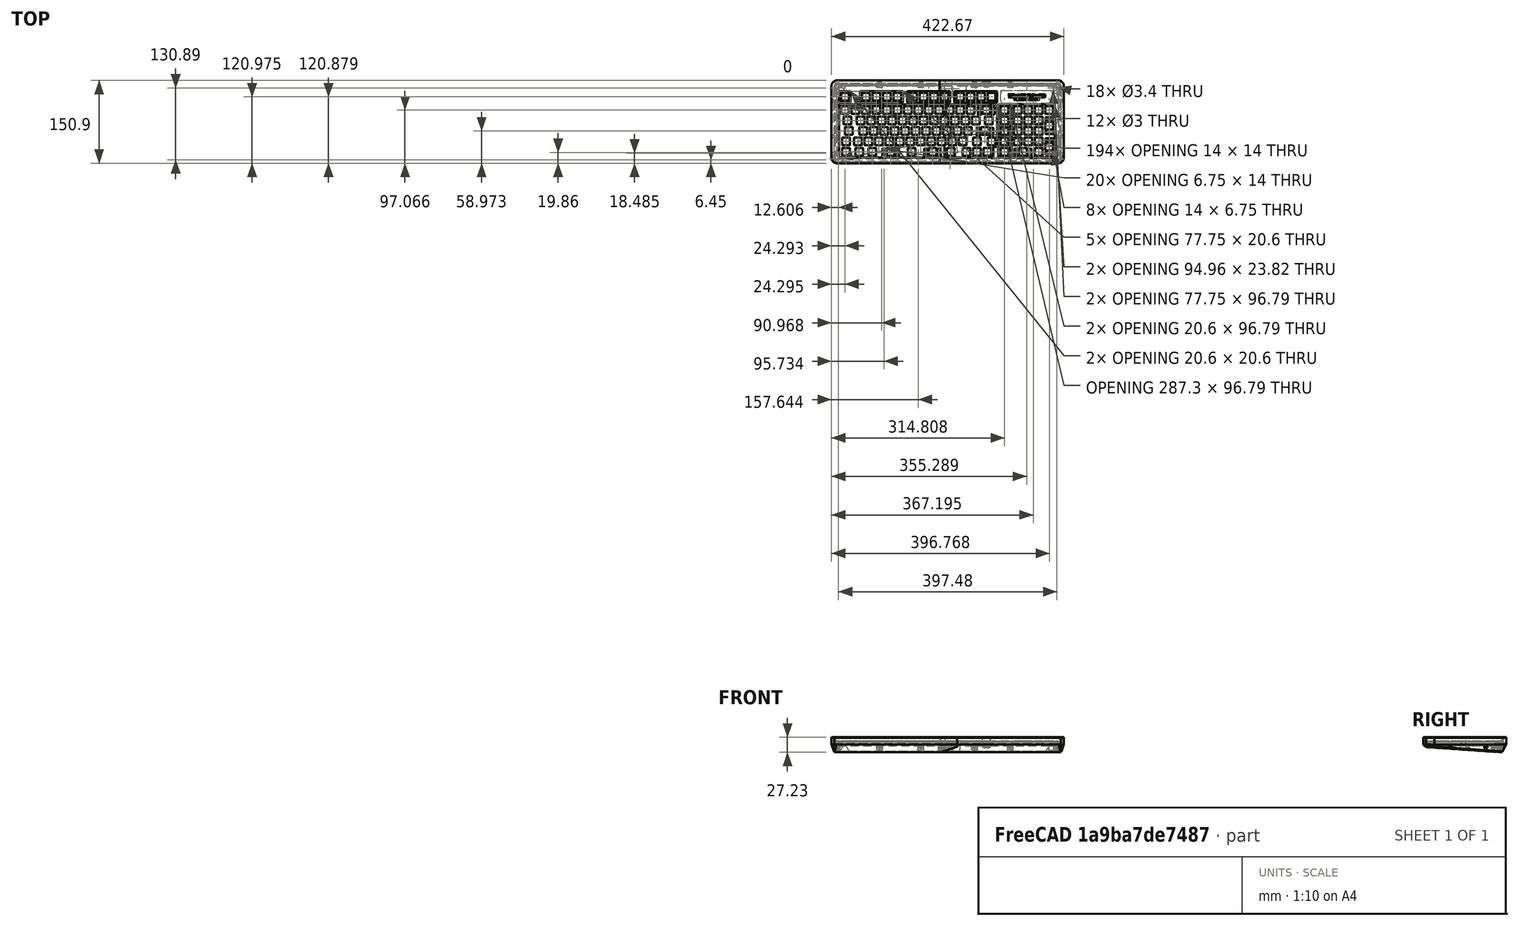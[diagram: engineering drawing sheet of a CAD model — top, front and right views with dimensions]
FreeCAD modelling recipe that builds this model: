
FCSTD DOCUMENT  (FreeCAD 0.21R33694 (Git))
Label: case
License: All rights reserved
LicenseURL: http://en.wikipedia.org/wiki/All_rights_reserved
objects: Sketcher::SketchObject×36, PartDesign::Pocket×20, PartDesign::SubShapeBinder×13, Part::FeaturePython×12, PartDesign::Pad×10, PartDesign::Plane×10, PartDesign::Body×6, Part::Part2DObjectPython×6, App::DocumentObjectGroup×4, PartDesign::AdditiveLoft×3, PartDesign::Chamfer×3, PartDesign::SubtractiveLoft×1, PartDesign::Fillet×1
note: 159 computed .brp shape members not serialized (recipe doc carries the construction recipe); baked Part::Feature solids carry a one-line shape summary decoded from their .brp

FEATURE [Sketcher::SketchObject] Sketch
  FullyConstrained = true
  sketch-geometry (922):
    g0: LineSegment StartX=400.028 StartY=-77.6274 StartZ=0 EndX=400.028 EndY=-71.8786 EndZ=0
    g1: LineSegment StartX=400.528 StartY=-71.3786 StartZ=0 EndX=413.528 EndY=-71.3774 EndZ=0
    g2: LineSegment StartX=414.028 StartY=-77.6274 StartZ=0 EndX=414.028 EndY=-71.8773 EndZ=0
    g3: LineSegment StartX=400.528 StartY=-95.1899 StartZ=0 EndX=413.528 EndY=-95.1899 EndZ=0
    g4: LineSegment StartX=400.028 StartY=-101.44 StartZ=0 EndX=400.028 EndY=-95.6899 EndZ=0
    g5: LineSegment StartX=400.528 StartY=-78.1274 StartZ=0 EndX=413.528 EndY=-78.1273 EndZ=0
    g6: LineSegment StartX=414.028 StartY=-101.44 StartZ=0 EndX=414.028 EndY=-95.6899 EndZ=0
    g7: LineSegment StartX=400.528 StartY=-101.94 StartZ=0 EndX=413.528 EndY=-101.94 EndZ=0
    g8: ArcOfCircle CenterX=413.528 CenterY=-71.8774 CenterZ=0 NormalX=0 NormalY=0 NormalZ=1 AngleXU=0 Radius=0.50005 StartAngle=9.99999e-05 EndAngle=1.57079
    g9: ArcOfCircle CenterX=413.528 CenterY=-95.6899 CenterZ=0 NormalX=0 NormalY=0 NormalZ=1 AngleXU=0 Radius=0.500001 StartAngle=1.99999e-06 EndAngle=1.57079
    g10: ArcOfCircle CenterX=400.528 CenterY=-71.8786 CenterZ=0 NormalX=0 NormalY=0 NormalZ=1 AngleXU=0 Radius=0.499999 StartAngle=1.57079 EndAngle=3.14152
    g11: ArcOfCircle CenterX=400.528 CenterY=-95.6899 CenterZ=0 NormalX=0 NormalY=0 NormalZ=1 AngleXU=0 Radius=0.500001 StartAngle=1.5708 EndAngle=3.14159
    g12: ArcOfCircle CenterX=413.528 CenterY=-101.44 CenterZ=0 NormalX=0 NormalY=0 NormalZ=1 AngleXU=0 Radius=0.500001 StartAngle=4.71239 EndAngle=6.28318
    g13: ArcOfCircle CenterX=413.528 CenterY=-77.6273 CenterZ=0 NormalX=0 NormalY=0 NormalZ=1 AngleXU=0 Radius=0.500001 StartAngle=4.71239 EndAngle=6.28309
    g14: ArcOfCircle CenterX=400.528 CenterY=-77.6274 CenterZ=0 NormalX=0 NormalY=0 NormalZ=1 AngleXU=0 Radius=0.49996 StartAngle=3.14151 EndAngle=4.71247
    g15: ArcOfCircle CenterX=400.528 CenterY=-101.44 CenterZ=0 NormalX=0 NormalY=0 NormalZ=1 AngleXU=0 Radius=0.500001 StartAngle=3.14159 EndAngle=4.71239
    g16: LineSegment StartX=179.329 StartY=-128.298 StartZ=0 EndX=185.079 EndY=-128.298 EndZ=0
    g17: LineSegment StartX=202.641 StartY=-128.798 StartZ=0 EndX=202.641 EndY=-141.798 EndZ=0
    g18: LineSegment StartX=203.141 StartY=-128.298 StartZ=0 EndX=208.89 EndY=-128.298 EndZ=0
    g19: LineSegment StartX=203.141 StartY=-142.298 StartZ=0 EndX=208.891 EndY=-142.298 EndZ=0
    g20: LineSegment StartX=185.579 StartY=-128.798 StartZ=0 EndX=185.579 EndY=-141.798 EndZ=0
    g21: LineSegment StartX=179.329 StartY=-142.298 StartZ=0 EndX=185.079 EndY=-142.298 EndZ=0
    g22: LineSegment StartX=178.829 StartY=-128.798 StartZ=0 EndX=178.829 EndY=-141.798 EndZ=0
    g23: LineSegment StartX=209.39 StartY=-128.798 StartZ=0 EndX=209.391 EndY=-141.798 EndZ=0
    g24: ArcOfCircle CenterX=179.329 CenterY=-141.798 CenterZ=0 NormalX=0 NormalY=0 NormalZ=1 AngleXU=0 Radius=0.500001 StartAngle=3.14159 EndAngle=4.71239
    g25: ArcOfCircle CenterX=185.079 CenterY=-128.798 CenterZ=0 NormalX=0 NormalY=0 NormalZ=1 AngleXU=0 Radius=0.500001 StartAngle=1.99999e-06 EndAngle=1.57079
    g26: ArcOfCircle CenterX=208.89 CenterY=-128.798 CenterZ=0 NormalX=0 NormalY=0 NormalZ=1 AngleXU=0 Radius=0.500099 StartAngle=0.000197985 EndAngle=1.57072
    g27: ArcOfCircle CenterX=203.141 CenterY=-141.798 CenterZ=0 NormalX=0 NormalY=0 NormalZ=1 AngleXU=0 Radius=0.500101 StartAngle=3.1418 EndAngle=4.71229
    g28: ArcOfCircle CenterX=203.141 CenterY=-128.798 CenterZ=0 NormalX=0 NormalY=0 NormalZ=1 AngleXU=0 Radius=0.49996 StartAngle=1.57071 EndAngle=3.14168
    g29: ArcOfCircle CenterX=179.329 CenterY=-128.798 CenterZ=0 NormalX=0 NormalY=0 NormalZ=1 AngleXU=0 Radius=0.500001 StartAngle=1.5708 EndAngle=3.14159
    g30: ArcOfCircle CenterX=185.079 CenterY=-141.798 CenterZ=0 NormalX=0 NormalY=0 NormalZ=1 AngleXU=0 Radius=0.500001 StartAngle=4.71239 EndAngle=6.28318
    g31: ArcOfCircle CenterX=208.891 CenterY=-141.798 CenterZ=0 NormalX=0 NormalY=0 NormalZ=1 AngleXU=0 Radius=0.49995 StartAngle=4.71229 EndAngle=6.28318
    g32: LineSegment StartX=276.438 StartY=-52.5898 StartZ=0 EndX=276.438 EndY=-65.5898 EndZ=0
    g33: LineSegment StartX=300.75 StartY=-52.0898 StartZ=0 EndX=306.499 EndY=-52.0898 EndZ=0
    g34: LineSegment StartX=300.25 StartY=-52.5898 StartZ=0 EndX=300.25 EndY=-65.5898 EndZ=0
    g35: LineSegment StartX=300.75 StartY=-66.0898 StartZ=0 EndX=306.5 EndY=-66.0897 EndZ=0
    g36: LineSegment StartX=283.188 StartY=-52.5898 StartZ=0 EndX=283.188 EndY=-65.5898 EndZ=0
    g37: LineSegment StartX=306.999 StartY=-52.5898 StartZ=0 EndX=307 EndY=-65.5898 EndZ=0
    g38: LineSegment StartX=276.938 StartY=-52.0898 StartZ=0 EndX=282.688 EndY=-52.0898 EndZ=0
    g39: LineSegment StartX=276.938 StartY=-66.0898 StartZ=0 EndX=282.688 EndY=-66.0898 EndZ=0
    g40: ArcOfCircle CenterX=282.688 CenterY=-52.5898 CenterZ=0 NormalX=0 NormalY=0 NormalZ=1 AngleXU=0 Radius=0.500001 StartAngle=1.99999e-06 EndAngle=1.57079
    g41: ArcOfCircle CenterX=300.75 CenterY=-65.5897 CenterZ=0 NormalX=0 NormalY=0 NormalZ=1 AngleXU=0 Radius=0.500101 StartAngle=3.1418 EndAngle=4.71229
    g42: ArcOfCircle CenterX=282.688 CenterY=-65.5898 CenterZ=0 NormalX=0 NormalY=0 NormalZ=1 AngleXU=0 Radius=0.500001 StartAngle=4.71239 EndAngle=6.28318
    g43: ArcOfCircle CenterX=300.75 CenterY=-52.5898 CenterZ=0 NormalX=0 NormalY=0 NormalZ=1 AngleXU=0 Radius=0.49996 StartAngle=1.57071 EndAngle=3.14168
    g44: ArcOfCircle CenterX=306.5 CenterY=-65.5898 CenterZ=0 NormalX=0 NormalY=0 NormalZ=1 AngleXU=0 Radius=0.49995 StartAngle=4.71229 EndAngle=6.28318
    g45: ArcOfCircle CenterX=276.938 CenterY=-52.5898 CenterZ=0 NormalX=0 NormalY=0 NormalZ=1 AngleXU=0 Radius=0.500001 StartAngle=1.5708 EndAngle=3.14159
    g46: ArcOfCircle CenterX=306.499 CenterY=-52.5899 CenterZ=0 NormalX=0 NormalY=0 NormalZ=1 AngleXU=0 Radius=0.500099 StartAngle=0.000197985 EndAngle=1.57072
    g47: ArcOfCircle CenterX=276.938 CenterY=-65.5898 CenterZ=0 NormalX=0 NormalY=0 NormalZ=1 AngleXU=0 Radius=0.500001 StartAngle=3.14159 EndAngle=4.71239
    g48: LineSegment StartX=367.435 StartY=-142.284 StartZ=0 EndX=373.185 EndY=-142.284 EndZ=0
    g49: LineSegment StartX=366.935 StartY=-128.784 StartZ=0 EndX=366.935 EndY=-141.784 EndZ=0
    g50: LineSegment StartX=367.435 StartY=-128.284 StartZ=0 EndX=373.183 EndY=-128.284 EndZ=0
    g51: LineSegment StartX=373.683 StartY=-128.784 StartZ=0 EndX=373.685 EndY=-141.784 EndZ=0
    g52: LineSegment StartX=343.622 StartY=-128.284 StartZ=0 EndX=349.372 EndY=-128.284 EndZ=0
    g53: LineSegment StartX=343.122 StartY=-128.784 StartZ=0 EndX=343.122 EndY=-141.784 EndZ=0
    g54: LineSegment StartX=349.872 StartY=-128.784 StartZ=0 EndX=349.872 EndY=-141.784 EndZ=0
    g55: LineSegment StartX=343.622 StartY=-142.284 StartZ=0 EndX=349.372 EndY=-142.284 EndZ=0
    g56: ArcOfCircle CenterX=373.185 CenterY=-141.784 CenterZ=0 NormalX=0 NormalY=0 NormalZ=1 AngleXU=0 Radius=0.50005 StartAngle=4.71249 EndAngle=6.28318
    g57: ArcOfCircle CenterX=343.622 CenterY=-141.784 CenterZ=0 NormalX=0 NormalY=0 NormalZ=1 AngleXU=0 Radius=0.500001 StartAngle=3.14159 EndAngle=4.71239
    g58: ArcOfCircle CenterX=367.435 CenterY=-128.784 CenterZ=0 NormalX=0 NormalY=0 NormalZ=1 AngleXU=0 Radius=0.49996 StartAngle=1.57071 EndAngle=3.14168
    g59: ArcOfCircle CenterX=367.435 CenterY=-141.784 CenterZ=0 NormalX=0 NormalY=0 NormalZ=1 AngleXU=0 Radius=0.500001 StartAngle=3.14159 EndAngle=4.71229
    g60: ArcOfCircle CenterX=349.372 CenterY=-141.784 CenterZ=0 NormalX=0 NormalY=0 NormalZ=1 AngleXU=0 Radius=0.500001 StartAngle=4.71239 EndAngle=6.28318
    g61: ArcOfCircle CenterX=349.372 CenterY=-128.784 CenterZ=0 NormalX=0 NormalY=0 NormalZ=1 AngleXU=0 Radius=0.500001 StartAngle=1.99999e-06 EndAngle=1.57079
    g62: ArcOfCircle CenterX=343.622 CenterY=-128.784 CenterZ=0 NormalX=0 NormalY=0 NormalZ=1 AngleXU=0 Radius=0.500001 StartAngle=1.5708 EndAngle=3.14159
    g63: ArcOfCircle CenterX=373.183 CenterY=-128.784 CenterZ=0 NormalX=0 NormalY=0 NormalZ=1 AngleXU=0 Radius=0.499999 StartAngle=6.28318 EndAngle=7.8539
    g64: LineSegment StartX=103.119 StartY=-142.29 StartZ=0 EndX=108.869 EndY=-142.29 EndZ=0
    g65: LineSegment StartX=126.431 StartY=-128.79 StartZ=0 EndX=126.431 EndY=-141.79 EndZ=0
    g66: LineSegment StartX=126.931 StartY=-128.29 StartZ=0 EndX=132.68 EndY=-128.29 EndZ=0
    g67: LineSegment StartX=126.931 StartY=-142.29 StartZ=0 EndX=132.681 EndY=-142.29 EndZ=0
    g68: LineSegment StartX=102.619 StartY=-128.79 StartZ=0 EndX=102.619 EndY=-141.79 EndZ=0
    g69: LineSegment StartX=109.369 StartY=-128.79 StartZ=0 EndX=109.369 EndY=-141.79 EndZ=0
    g70: LineSegment StartX=103.119 StartY=-128.29 StartZ=0 EndX=108.869 EndY=-128.29 EndZ=0
    g71: LineSegment StartX=133.18 StartY=-128.79 StartZ=0 EndX=133.181 EndY=-141.79 EndZ=0
    g72: ArcOfCircle CenterX=132.681 CenterY=-141.79 CenterZ=0 NormalX=0 NormalY=0 NormalZ=1 AngleXU=0 Radius=0.50005 StartAngle=4.71249 EndAngle=6.28318
    g73: ArcOfCircle CenterX=108.869 CenterY=-128.79 CenterZ=0 NormalX=0 NormalY=0 NormalZ=1 AngleXU=0 Radius=0.500001 StartAngle=1.99999e-06 EndAngle=1.57079
    g74: ArcOfCircle CenterX=126.931 CenterY=-141.79 CenterZ=0 NormalX=0 NormalY=0 NormalZ=1 AngleXU=0 Radius=0.500001 StartAngle=3.14159 EndAngle=4.71229
    g75: ArcOfCircle CenterX=132.68 CenterY=-128.79 CenterZ=0 NormalX=0 NormalY=0 NormalZ=1 AngleXU=0 Radius=0.499999 StartAngle=6.28318 EndAngle=7.8539
    g76: ArcOfCircle CenterX=108.869 CenterY=-141.79 CenterZ=0 NormalX=0 NormalY=0 NormalZ=1 AngleXU=0 Radius=0.500001 StartAngle=4.71239 EndAngle=6.28318
    g77: ArcOfCircle CenterX=103.119 CenterY=-141.79 CenterZ=0 NormalX=0 NormalY=0 NormalZ=1 AngleXU=0 Radius=0.500001 StartAngle=3.14159 EndAngle=4.71239
    g78: ArcOfCircle CenterX=126.931 CenterY=-128.79 CenterZ=0 NormalX=0 NormalY=0 NormalZ=1 AngleXU=0 Radius=0.49996 StartAngle=1.57071 EndAngle=3.14168
    g79: ArcOfCircle CenterX=103.119 CenterY=-128.79 CenterZ=0 NormalX=0 NormalY=0 NormalZ=1 AngleXU=0 Radius=0.500001 StartAngle=1.5708 EndAngle=3.14159
    g80: LineSegment StartX=400.028 StartY=-115.727 StartZ=0 EndX=400.028 EndY=-109.979 EndZ=0
    g81: LineSegment StartX=400.528 StartY=-133.29 StartZ=0 EndX=413.528 EndY=-133.29 EndZ=0
    g82: LineSegment StartX=400.528 StartY=-109.479 StartZ=0 EndX=413.528 EndY=-109.477 EndZ=0
    g83: LineSegment StartX=400.028 StartY=-139.54 StartZ=0 EndX=400.028 EndY=-133.79 EndZ=0
    g84: LineSegment StartX=414.028 StartY=-115.727 StartZ=0 EndX=414.028 EndY=-109.977 EndZ=0
    g85: LineSegment StartX=414.028 StartY=-139.54 StartZ=0 EndX=414.028 EndY=-133.79 EndZ=0
    g86: LineSegment StartX=400.528 StartY=-140.04 StartZ=0 EndX=413.528 EndY=-140.04 EndZ=0
    g87: LineSegment StartX=400.528 StartY=-116.227 StartZ=0 EndX=413.528 EndY=-116.227 EndZ=0
    g88: ArcOfCircle CenterX=413.528 CenterY=-115.727 CenterZ=0 NormalX=0 NormalY=0 NormalZ=1 AngleXU=0 Radius=0.500001 StartAngle=4.71239 EndAngle=6.28309
    g89: ArcOfCircle CenterX=400.528 CenterY=-115.727 CenterZ=0 NormalX=0 NormalY=0 NormalZ=1 AngleXU=0 Radius=0.49996 StartAngle=3.14151 EndAngle=4.71247
    g90: ArcOfCircle CenterX=400.528 CenterY=-133.79 CenterZ=0 NormalX=0 NormalY=0 NormalZ=1 AngleXU=0 Radius=0.500001 StartAngle=1.5708 EndAngle=3.14159
    g91: ArcOfCircle CenterX=413.528 CenterY=-109.977 CenterZ=0 NormalX=0 NormalY=0 NormalZ=1 AngleXU=0 Radius=0.50005 StartAngle=9.99999e-05 EndAngle=1.57079
    g92: ArcOfCircle CenterX=413.528 CenterY=-133.79 CenterZ=0 NormalX=0 NormalY=0 NormalZ=1 AngleXU=0 Radius=0.500001 StartAngle=1.99999e-06 EndAngle=1.57079
    g93: ArcOfCircle CenterX=413.528 CenterY=-139.54 CenterZ=0 NormalX=0 NormalY=0 NormalZ=1 AngleXU=0 Radius=0.500001 StartAngle=4.71239 EndAngle=6.28318
    g94: ArcOfCircle CenterX=400.528 CenterY=-139.54 CenterZ=0 NormalX=0 NormalY=0 NormalZ=1 AngleXU=0 Radius=0.500001 StartAngle=3.14159 EndAngle=4.71239
    g95: ArcOfCircle CenterX=400.528 CenterY=-109.979 CenterZ=0 NormalX=0 NormalY=0 NormalZ=1 AngleXU=0 Radius=0.499999 StartAngle=1.57079 EndAngle=3.14152
    g96: LineSegment StartX=298.363 StartY=-90.1898 StartZ=0 EndX=304.111 EndY=-90.1898 EndZ=0
    g97: LineSegment StartX=297.863 StartY=-90.6898 StartZ=0 EndX=297.863 EndY=-103.69 EndZ=0
    g98: LineSegment StartX=274.55 StartY=-90.1898 StartZ=0 EndX=280.3 EndY=-90.1898 EndZ=0
    g99: LineSegment StartX=274.05 StartY=-90.6898 StartZ=0 EndX=274.05 EndY=-103.69 EndZ=0
    g100: LineSegment StartX=274.55 StartY=-104.19 StartZ=0 EndX=280.3 EndY=-104.19 EndZ=0
    g101: LineSegment StartX=304.611 StartY=-90.6898 StartZ=0 EndX=304.613 EndY=-103.69 EndZ=0
    g102: LineSegment StartX=280.8 StartY=-90.6898 StartZ=0 EndX=280.8 EndY=-103.69 EndZ=0
    g103: LineSegment StartX=298.363 StartY=-104.19 StartZ=0 EndX=304.113 EndY=-104.19 EndZ=0
    g104: ArcOfCircle CenterX=274.55 CenterY=-103.69 CenterZ=0 NormalX=0 NormalY=0 NormalZ=1 AngleXU=0 Radius=0.500001 StartAngle=3.14159 EndAngle=4.71239
    g105: ArcOfCircle CenterX=304.111 CenterY=-90.6899 CenterZ=0 NormalX=0 NormalY=0 NormalZ=1 AngleXU=0 Radius=0.500099 StartAngle=0.000197985 EndAngle=1.57072
    g106: ArcOfCircle CenterX=274.55 CenterY=-90.6898 CenterZ=0 NormalX=0 NormalY=0 NormalZ=1 AngleXU=0 Radius=0.500001 StartAngle=1.5708 EndAngle=3.14159
    g107: ArcOfCircle CenterX=280.3 CenterY=-103.69 CenterZ=0 NormalX=0 NormalY=0 NormalZ=1 AngleXU=0 Radius=0.500001 StartAngle=4.71239 EndAngle=6.28318
    g108: ArcOfCircle CenterX=280.3 CenterY=-90.6898 CenterZ=0 NormalX=0 NormalY=0 NormalZ=1 AngleXU=0 Radius=0.500001 StartAngle=1.99999e-06 EndAngle=1.57079
    g109: ArcOfCircle CenterX=304.113 CenterY=-103.69 CenterZ=0 NormalX=0 NormalY=0 NormalZ=1 AngleXU=0 Radius=0.49995 StartAngle=4.71229 EndAngle=6.28318
    g110: ArcOfCircle CenterX=298.363 CenterY=-103.69 CenterZ=0 NormalX=0 NormalY=0 NormalZ=1 AngleXU=0 Radius=0.500101 StartAngle=3.1418 EndAngle=4.71229
    g111: ArcOfCircle CenterX=298.363 CenterY=-90.6898 CenterZ=0 NormalX=0 NormalY=0 NormalZ=1 AngleXU=0 Radius=0.49996 StartAngle=1.57071 EndAngle=3.14168
    g112: LineSegment StartX=88.6784 StartY=-84.1336 StartZ=0 EndX=75.6784 EndY=-84.1336 EndZ=0
    g113: LineSegment StartX=89.1784 StartY=-70.6336 StartZ=0 EndX=89.1784 EndY=-83.6336 EndZ=0
    g114: LineSegment StartX=75.6812 StartY=-70.1347 StartZ=0 EndX=88.6784 EndY=-70.1336 EndZ=0
    g115: LineSegment StartX=75.1784 StartY=-83.6336 StartZ=0 EndX=75.1812 EndY=-70.6347 EndZ=0
    g116: ArcOfCircle CenterX=75.6812 CenterY=-70.6347 CenterZ=0 NormalX=0 NormalY=0 NormalZ=1 AngleXU=0 Radius=0.500001 StartAngle=1.5708 EndAngle=3.14159
    g117: ArcOfCircle CenterX=88.6784 CenterY=-70.6336 CenterZ=0 NormalX=0 NormalY=0 NormalZ=1 AngleXU=0 Radius=0.5 StartAngle=0 EndAngle=1.5708
    g118: ArcOfCircle CenterX=88.6784 CenterY=-83.6336 CenterZ=0 NormalX=0 NormalY=0 NormalZ=1 AngleXU=0 Radius=0.5 StartAngle=4.71239 EndAngle=6.28319
    g119: ArcOfCircle CenterX=75.6784 CenterY=-83.6336 CenterZ=0 NormalX=0 NormalY=0 NormalZ=1 AngleXU=0 Radius=0.500001 StartAngle=3.14159 EndAngle=4.71239
    g120: LineSegment StartX=74.8909 StartY=-89.6836 StartZ=0 EndX=74.8909 EndY=-102.684 EndZ=0
    g121: LineSegment StartX=74.3909 StartY=-103.184 StartZ=0 EndX=61.3909 EndY=-103.184 EndZ=0
    g122: LineSegment StartX=60.8909 StartY=-102.684 StartZ=0 EndX=60.8937 EndY=-89.6847 EndZ=0
    g123: LineSegment StartX=61.3937 StartY=-89.1847 StartZ=0 EndX=74.3909 EndY=-89.1836 EndZ=0
    g124: ArcOfCircle CenterX=61.3909 CenterY=-102.684 CenterZ=0 NormalX=0 NormalY=0 NormalZ=1 AngleXU=0 Radius=0.500001 StartAngle=3.14159 EndAngle=4.71239
    g125: ArcOfCircle CenterX=74.3909 CenterY=-89.6836 CenterZ=0 NormalX=0 NormalY=0 NormalZ=1 AngleXU=0 Radius=0.5 StartAngle=0 EndAngle=1.5708
    g126: ArcOfCircle CenterX=74.3909 CenterY=-102.684 CenterZ=0 NormalX=0 NormalY=0 NormalZ=1 AngleXU=0 Radius=0.5 StartAngle=4.71239 EndAngle=6.28319
    g127: ArcOfCircle CenterX=61.3937 CenterY=-89.6847 CenterZ=0 NormalX=0 NormalY=0 NormalZ=1 AngleXU=0 Radius=0.500001 StartAngle=1.5708 EndAngle=3.14159
    g128: LineSegment StartX=117.753 StartY=-51.5836 StartZ=0 EndX=117.753 EndY=-64.5836 EndZ=0
    g129: LineSegment StartX=117.253 StartY=-65.0836 StartZ=0 EndX=104.253 EndY=-65.0836 EndZ=0
    g130: LineSegment StartX=103.753 StartY=-64.5836 StartZ=0 EndX=103.756 EndY=-51.5847 EndZ=0
    g131: LineSegment StartX=104.256 StartY=-51.0847 StartZ=0 EndX=117.253 EndY=-51.0836 EndZ=0
    g132: ArcOfCircle CenterX=104.256 CenterY=-51.5847 CenterZ=0 NormalX=0 NormalY=0 NormalZ=1 AngleXU=0 Radius=0.500001 StartAngle=1.5708 EndAngle=3.14159
    g133: ArcOfCircle CenterX=117.253 CenterY=-64.5836 CenterZ=0 NormalX=0 NormalY=0 NormalZ=1 AngleXU=0 Radius=0.5 StartAngle=4.71239 EndAngle=6.28319
    g134: ArcOfCircle CenterX=117.253 CenterY=-51.5836 CenterZ=0 NormalX=0 NormalY=0 NormalZ=1 AngleXU=0 Radius=0.5 StartAngle=0 EndAngle=1.5708
    g135: ArcOfCircle CenterX=104.253 CenterY=-64.5836 CenterZ=0 NormalX=0 NormalY=0 NormalZ=1 AngleXU=0 Radius=0.500001 StartAngle=3.14159 EndAngle=4.71239
    g136: LineSegment StartX=184.428 StartY=-70.6336 StartZ=0 EndX=184.428 EndY=-83.6336 EndZ=0
    g137: LineSegment StartX=183.928 StartY=-84.1336 StartZ=0 EndX=170.928 EndY=-84.1336 EndZ=0
    g138: LineSegment StartX=170.931 StartY=-70.1347 StartZ=0 EndX=183.928 EndY=-70.1336 EndZ=0
    g139: LineSegment StartX=170.428 StartY=-83.6336 StartZ=0 EndX=170.431 EndY=-70.6347 EndZ=0
    g140: ArcOfCircle CenterX=183.928 CenterY=-70.6336 CenterZ=0 NormalX=0 NormalY=0 NormalZ=1 AngleXU=0 Radius=0.5 StartAngle=0 EndAngle=1.5708
    g141: ArcOfCircle CenterX=170.928 CenterY=-83.6336 CenterZ=0 NormalX=0 NormalY=0 NormalZ=1 AngleXU=0 Radius=0.500001 StartAngle=3.14159 EndAngle=4.71239
    g142: ArcOfCircle CenterX=183.928 CenterY=-83.6336 CenterZ=0 NormalX=0 NormalY=0 NormalZ=1 AngleXU=0 Radius=0.5 StartAngle=4.71239 EndAngle=6.28319
    g143: ArcOfCircle CenterX=170.931 CenterY=-70.6347 CenterZ=0 NormalX=0 NormalY=0 NormalZ=1 AngleXU=0 Radius=0.500001 StartAngle=1.5708 EndAngle=3.14159
    g144: LineSegment StartX=35.1999 StartY=-89.1847 StartZ=0 EndX=48.1972 EndY=-89.1836 EndZ=0
    g145: LineSegment StartX=34.6972 StartY=-102.684 StartZ=0 EndX=34.6999 EndY=-89.6847 EndZ=0
    g146: LineSegment StartX=48.1972 StartY=-103.184 StartZ=0 EndX=35.1972 EndY=-103.184 EndZ=0
    g147: LineSegment StartX=48.6972 StartY=-89.6836 StartZ=0 EndX=48.6972 EndY=-102.684 EndZ=0
    g148: ArcOfCircle CenterX=35.1972 CenterY=-102.684 CenterZ=0 NormalX=0 NormalY=0 NormalZ=1 AngleXU=0 Radius=0.500001 StartAngle=3.14159 EndAngle=4.71239
    g149: ArcOfCircle CenterX=35.1999 CenterY=-89.6847 CenterZ=0 NormalX=0 NormalY=0 NormalZ=1 AngleXU=0 Radius=0.500001 StartAngle=1.5708 EndAngle=3.14159
    g150: ArcOfCircle CenterX=48.1972 CenterY=-89.6836 CenterZ=0 NormalX=0 NormalY=0 NormalZ=1 AngleXU=0 Radius=0.5 StartAngle=0 EndAngle=1.5708
    g151: ArcOfCircle CenterX=48.1972 CenterY=-102.684 CenterZ=0 NormalX=0 NormalY=0 NormalZ=1 AngleXU=0 Radius=0.5 StartAngle=4.71239 EndAngle=6.28319
    g152: LineSegment StartX=379.978 StartY=-83.6336 StartZ=0 EndX=379.981 EndY=-70.6347 EndZ=0
    g153: LineSegment StartX=393.978 StartY=-70.6336 StartZ=0 EndX=393.978 EndY=-83.6336 EndZ=0
    g154: LineSegment StartX=393.478 StartY=-84.1336 StartZ=0 EndX=380.478 EndY=-84.1336 EndZ=0
    g155: LineSegment StartX=380.481 StartY=-70.1347 StartZ=0 EndX=393.478 EndY=-70.1336 EndZ=0
    g156: ArcOfCircle CenterX=380.478 CenterY=-83.6336 CenterZ=0 NormalX=0 NormalY=0 NormalZ=1 AngleXU=0 Radius=0.500001 StartAngle=3.14159 EndAngle=4.71239
    g157: ArcOfCircle CenterX=393.478 CenterY=-70.6336 CenterZ=0 NormalX=0 NormalY=0 NormalZ=1 AngleXU=0 Radius=0.5 StartAngle=0 EndAngle=1.5708
    g158: ArcOfCircle CenterX=393.478 CenterY=-83.6336 CenterZ=0 NormalX=0 NormalY=0 NormalZ=1 AngleXU=0 Radius=0.5 StartAngle=4.71239 EndAngle=6.28319
    g159: ArcOfCircle CenterX=380.481 CenterY=-70.6347 CenterZ=0 NormalX=0 NormalY=0 NormalZ=1 AngleXU=0 Radius=0.500001 StartAngle=1.5708 EndAngle=3.14159
    g160: LineSegment StartX=289.203 StartY=-27.7711 StartZ=0 EndX=289.203 EndY=-40.7711 EndZ=0
    g161: LineSegment StartX=275.706 StartY=-27.2722 StartZ=0 EndX=288.703 EndY=-27.2711 EndZ=0
    g162: LineSegment StartX=288.703 StartY=-41.2711 StartZ=0 EndX=275.703 EndY=-41.2711 EndZ=0
    g163: LineSegment StartX=275.203 StartY=-40.7711 StartZ=0 EndX=275.206 EndY=-27.7722 EndZ=0
    g164: ArcOfCircle CenterX=275.706 CenterY=-27.7722 CenterZ=0 NormalX=0 NormalY=0 NormalZ=1 AngleXU=0 Radius=0.500001 StartAngle=1.5708 EndAngle=3.14159
    g165: ArcOfCircle CenterX=288.703 CenterY=-40.7711 CenterZ=0 NormalX=0 NormalY=0 NormalZ=1 AngleXU=0 Radius=0.5 StartAngle=4.71239 EndAngle=6.28319
    g166: ArcOfCircle CenterX=288.703 CenterY=-27.7711 CenterZ=0 NormalX=0 NormalY=0 NormalZ=1 AngleXU=0 Radius=0.5 StartAngle=0 EndAngle=1.5708
    g167: ArcOfCircle CenterX=275.703 CenterY=-40.7711 CenterZ=0 NormalX=0 NormalY=0 NormalZ=1 AngleXU=0 Radius=0.500001 StartAngle=3.14159 EndAngle=4.71239
    g168: LineSegment StartX=202.978 StartY=-84.1336 StartZ=0 EndX=189.978 EndY=-84.1336 EndZ=0
    g169: LineSegment StartX=189.981 StartY=-70.1347 StartZ=0 EndX=202.978 EndY=-70.1336 EndZ=0
    g170: LineSegment StartX=189.478 StartY=-83.6336 StartZ=0 EndX=189.481 EndY=-70.6347 EndZ=0
    g171: LineSegment StartX=203.478 StartY=-70.6336 StartZ=0 EndX=203.478 EndY=-83.6336 EndZ=0
    g172: ArcOfCircle CenterX=202.978 CenterY=-83.6336 CenterZ=0 NormalX=0 NormalY=0 NormalZ=1 AngleXU=0 Radius=0.5 StartAngle=4.71239 EndAngle=6.28319
    g173: ArcOfCircle CenterX=202.978 CenterY=-70.6336 CenterZ=0 NormalX=0 NormalY=0 NormalZ=1 AngleXU=0 Radius=0.5 StartAngle=0 EndAngle=1.5708
    g174: ArcOfCircle CenterX=189.981 CenterY=-70.6347 CenterZ=0 NormalX=0 NormalY=0 NormalZ=1 AngleXU=0 Radius=0.500001 StartAngle=1.5708 EndAngle=3.14159
    g175: ArcOfCircle CenterX=189.978 CenterY=-83.6336 CenterZ=0 NormalX=0 NormalY=0 NormalZ=1 AngleXU=0 Radius=0.500001 StartAngle=3.14159 EndAngle=4.71239
    g176: LineSegment StartX=393.478 StartY=-65.0836 StartZ=0 EndX=380.478 EndY=-65.0836 EndZ=0
    g177: LineSegment StartX=379.978 StartY=-64.5836 StartZ=0 EndX=379.981 EndY=-51.5847 EndZ=0
    g178: LineSegment StartX=380.481 StartY=-51.0847 StartZ=0 EndX=393.478 EndY=-51.0836 EndZ=0
    g179: LineSegment StartX=393.978 StartY=-51.5836 StartZ=0 EndX=393.978 EndY=-64.5836 EndZ=0
    g180: ArcOfCircle CenterX=393.478 CenterY=-51.5836 CenterZ=0 NormalX=0 NormalY=0 NormalZ=1 AngleXU=0 Radius=0.5 StartAngle=0 EndAngle=1.5708
    g181: ArcOfCircle CenterX=393.478 CenterY=-64.5836 CenterZ=0 NormalX=0 NormalY=0 NormalZ=1 AngleXU=0 Radius=0.5 StartAngle=4.71239 EndAngle=6.28319
    g182: ArcOfCircle CenterX=380.481 CenterY=-51.5847 CenterZ=0 NormalX=0 NormalY=0 NormalZ=1 AngleXU=0 Radius=0.500001 StartAngle=1.5708 EndAngle=3.14159
    g183: ArcOfCircle CenterX=380.478 CenterY=-64.5836 CenterZ=0 NormalX=0 NormalY=0 NormalZ=1 AngleXU=0 Radius=0.500001 StartAngle=3.14159 EndAngle=4.71239
    g184: LineSegment StartX=251.391 StartY=-102.684 StartZ=0 EndX=251.394 EndY=-89.6847 EndZ=0
    g185: LineSegment StartX=264.891 StartY=-103.184 StartZ=0 EndX=251.891 EndY=-103.184 EndZ=0
    g186: LineSegment StartX=251.894 StartY=-89.1847 StartZ=0 EndX=264.891 EndY=-89.1836 EndZ=0
    g187: LineSegment StartX=265.391 StartY=-89.6836 StartZ=0 EndX=265.391 EndY=-102.684 EndZ=0
    g188: ArcOfCircle CenterX=251.894 CenterY=-89.6847 CenterZ=0 NormalX=0 NormalY=0 NormalZ=1 AngleXU=0 Radius=0.500001 StartAngle=1.5708 EndAngle=3.14159
    g189: ArcOfCircle CenterX=264.891 CenterY=-89.6836 CenterZ=0 NormalX=0 NormalY=0 NormalZ=1 AngleXU=0 Radius=0.5 StartAngle=0 EndAngle=1.5708
    g190: ArcOfCircle CenterX=264.891 CenterY=-102.684 CenterZ=0 NormalX=0 NormalY=0 NormalZ=1 AngleXU=0 Radius=0.5 StartAngle=4.71239 EndAngle=6.28319
    g191: ArcOfCircle CenterX=251.891 CenterY=-102.684 CenterZ=0 NormalX=0 NormalY=0 NormalZ=1 AngleXU=0 Radius=0.500001 StartAngle=3.14159 EndAngle=4.71239
    g192: LineSegment StartX=41.5534 StartY=-27.7711 StartZ=0 EndX=41.5534 EndY=-40.7711 EndZ=0
    g193: LineSegment StartX=28.0562 StartY=-27.2722 StartZ=0 EndX=41.0534 EndY=-27.2711 EndZ=0
    g194: LineSegment StartX=41.0534 StartY=-41.2711 StartZ=0 EndX=28.0534 EndY=-41.2711 EndZ=0
    g195: LineSegment StartX=27.5534 StartY=-40.7711 StartZ=0 EndX=27.5562 EndY=-27.7722 EndZ=0
    g196: ArcOfCircle CenterX=28.0534 CenterY=-40.7711 CenterZ=0 NormalX=0 NormalY=0 NormalZ=1 AngleXU=0 Radius=0.500001 StartAngle=3.14159 EndAngle=4.71239
    g197: ArcOfCircle CenterX=41.0534 CenterY=-27.7711 CenterZ=0 NormalX=0 NormalY=0 NormalZ=1 AngleXU=0 Radius=0.5 StartAngle=0 EndAngle=1.5708
    g198: ArcOfCircle CenterX=28.0562 CenterY=-27.7722 CenterZ=0 NormalX=0 NormalY=0 NormalZ=1 AngleXU=0 Radius=0.500001 StartAngle=1.5708 EndAngle=3.14159
    g199: ArcOfCircle CenterX=41.0534 CenterY=-40.7711 CenterZ=0 NormalX=0 NormalY=0 NormalZ=1 AngleXU=0 Radius=0.5 StartAngle=4.71239 EndAngle=6.28319
    g200: LineSegment StartX=241.078 StartY=-84.1336 StartZ=0 EndX=228.078 EndY=-84.1336 EndZ=0
    g201: LineSegment StartX=228.081 StartY=-70.1347 StartZ=0 EndX=241.078 EndY=-70.1336 EndZ=0
    g202: LineSegment StartX=241.578 StartY=-70.6336 StartZ=0 EndX=241.578 EndY=-83.6336 EndZ=0
    g203: LineSegment StartX=227.578 StartY=-83.6336 StartZ=0 EndX=227.581 EndY=-70.6347 EndZ=0
    g204: ArcOfCircle CenterX=228.081 CenterY=-70.6347 CenterZ=0 NormalX=0 NormalY=0 NormalZ=1 AngleXU=0 Radius=0.500001 StartAngle=1.5708 EndAngle=3.14159
    g205: ArcOfCircle CenterX=228.078 CenterY=-83.6336 CenterZ=0 NormalX=0 NormalY=0 NormalZ=1 AngleXU=0 Radius=0.500001 StartAngle=3.14159 EndAngle=4.71239
    g206: ArcOfCircle CenterX=241.078 CenterY=-70.6336 CenterZ=0 NormalX=0 NormalY=0 NormalZ=1 AngleXU=0 Radius=0.5 StartAngle=0 EndAngle=1.5708
    g207: ArcOfCircle CenterX=241.078 CenterY=-83.6336 CenterZ=0 NormalX=0 NormalY=0 NormalZ=1 AngleXU=0 Radius=0.5 StartAngle=4.71239 EndAngle=6.28319
    g208: LineSegment StartX=189.191 StartY=-89.6836 StartZ=0 EndX=189.191 EndY=-102.684 EndZ=0
    g209: LineSegment StartX=188.691 StartY=-103.184 StartZ=0 EndX=175.691 EndY=-103.184 EndZ=0
    g210: LineSegment StartX=175.191 StartY=-102.684 StartZ=0 EndX=175.194 EndY=-89.6847 EndZ=0
    g211: LineSegment StartX=175.694 StartY=-89.1847 StartZ=0 EndX=188.691 EndY=-89.1836 EndZ=0
    g212: ArcOfCircle CenterX=175.694 CenterY=-89.6847 CenterZ=0 NormalX=0 NormalY=0 NormalZ=1 AngleXU=0 Radius=0.500001 StartAngle=1.5708 EndAngle=3.14159
    g213: ArcOfCircle CenterX=175.691 CenterY=-102.684 CenterZ=0 NormalX=0 NormalY=0 NormalZ=1 AngleXU=0 Radius=0.500001 StartAngle=3.14159 EndAngle=4.71239
    g214: ArcOfCircle CenterX=188.691 CenterY=-102.684 CenterZ=0 NormalX=0 NormalY=0 NormalZ=1 AngleXU=0 Radius=0.5 StartAngle=4.71239 EndAngle=6.28319
    g215: ArcOfCircle CenterX=188.691 CenterY=-89.6836 CenterZ=0 NormalX=0 NormalY=0 NormalZ=1 AngleXU=0 Radius=0.5 StartAngle=0 EndAngle=1.5708
    g216: LineSegment StartX=184.716 StartY=-121.734 StartZ=0 EndX=184.719 EndY=-108.735 EndZ=0
    g217: LineSegment StartX=198.216 StartY=-122.234 StartZ=0 EndX=185.216 EndY=-122.234 EndZ=0
    g218: LineSegment StartX=198.716 StartY=-108.734 StartZ=0 EndX=198.716 EndY=-121.734 EndZ=0
    g219: LineSegment StartX=185.219 StartY=-108.235 StartZ=0 EndX=198.216 EndY=-108.234 EndZ=0
    g220: ArcOfCircle CenterX=198.216 CenterY=-108.734 CenterZ=0 NormalX=0 NormalY=0 NormalZ=1 AngleXU=0 Radius=0.5 StartAngle=0 EndAngle=1.5708
    g221: ArcOfCircle CenterX=198.216 CenterY=-121.734 CenterZ=0 NormalX=0 NormalY=0 NormalZ=1 AngleXU=0 Radius=0.5 StartAngle=4.71239 EndAngle=6.28319
    g222: ArcOfCircle CenterX=185.216 CenterY=-121.734 CenterZ=0 NormalX=0 NormalY=0 NormalZ=1 AngleXU=0 Radius=0.500001 StartAngle=3.14159 EndAngle=4.71239
    g223: ArcOfCircle CenterX=185.219 CenterY=-108.735 CenterZ=0 NormalX=0 NormalY=0 NormalZ=1 AngleXU=0 Radius=0.500001 StartAngle=1.5708 EndAngle=3.14159
    g224: LineSegment StartX=220.42 StartY=-140.79 StartZ=0 EndX=220.423 EndY=-127.791 EndZ=0
    g225: LineSegment StartX=220.923 StartY=-127.291 StartZ=0 EndX=233.92 EndY=-127.29 EndZ=0
    g226: LineSegment StartX=234.42 StartY=-127.79 StartZ=0 EndX=234.42 EndY=-140.79 EndZ=0
    g227: LineSegment StartX=233.92 StartY=-141.29 StartZ=0 EndX=220.92 EndY=-141.29 EndZ=0
    g228: ArcOfCircle CenterX=233.92 CenterY=-140.79 CenterZ=0 NormalX=0 NormalY=0 NormalZ=1 AngleXU=0 Radius=0.5 StartAngle=4.71239 EndAngle=6.28319
    g229: ArcOfCircle CenterX=233.92 CenterY=-127.79 CenterZ=0 NormalX=0 NormalY=0 NormalZ=1 AngleXU=0 Radius=0.5 StartAngle=0 EndAngle=1.5708
    g230: ArcOfCircle CenterX=220.923 CenterY=-127.791 CenterZ=0 NormalX=0 NormalY=0 NormalZ=1 AngleXU=0 Radius=0.500001 StartAngle=1.5708 EndAngle=3.14159
    g231: ArcOfCircle CenterX=220.92 CenterY=-140.79 CenterZ=0 NormalX=0 NormalY=0 NormalZ=1 AngleXU=0 Radius=0.500001 StartAngle=3.14159 EndAngle=4.71239
    g232: LineSegment StartX=151.091 StartY=-89.6836 StartZ=0 EndX=151.091 EndY=-102.684 EndZ=0
    g233: LineSegment StartX=150.591 StartY=-103.184 StartZ=0 EndX=137.591 EndY=-103.184 EndZ=0
    g234: LineSegment StartX=137.091 StartY=-102.684 StartZ=0 EndX=137.094 EndY=-89.6847 EndZ=0
    g235: LineSegment StartX=137.594 StartY=-89.1847 StartZ=0 EndX=150.591 EndY=-89.1836 EndZ=0
    g236: ArcOfCircle CenterX=150.591 CenterY=-89.6836 CenterZ=0 NormalX=0 NormalY=0 NormalZ=1 AngleXU=0 Radius=0.5 StartAngle=0 EndAngle=1.5708
    g237: ArcOfCircle CenterX=150.591 CenterY=-102.684 CenterZ=0 NormalX=0 NormalY=0 NormalZ=1 AngleXU=0 Radius=0.5 StartAngle=4.71239 EndAngle=6.28319
    g238: ArcOfCircle CenterX=137.594 CenterY=-89.6847 CenterZ=0 NormalX=0 NormalY=0 NormalZ=1 AngleXU=0 Radius=0.500001 StartAngle=1.5708 EndAngle=3.14159
    g239: ArcOfCircle CenterX=137.591 CenterY=-102.684 CenterZ=0 NormalX=0 NormalY=0 NormalZ=1 AngleXU=0 Radius=0.500001 StartAngle=3.14159 EndAngle=4.71239
    g240: LineSegment StartX=412.528 StartY=-93.6586 StartZ=0 EndX=399.528 EndY=-93.6586 EndZ=0
    g241: LineSegment StartX=399.531 StartY=-79.6597 StartZ=0 EndX=412.528 EndY=-79.6586 EndZ=0
    g242: LineSegment StartX=413.028 StartY=-80.1586 StartZ=0 EndX=413.028 EndY=-93.1586 EndZ=0
    g243: LineSegment StartX=399.028 StartY=-93.1586 StartZ=0 EndX=399.031 EndY=-80.1597 EndZ=0
    g244: ArcOfCircle CenterX=399.531 CenterY=-80.1597 CenterZ=0 NormalX=0 NormalY=0 NormalZ=1 AngleXU=0 Radius=0.500001 StartAngle=1.5708 EndAngle=3.14159
    g245: ArcOfCircle CenterX=412.528 CenterY=-80.1586 CenterZ=0 NormalX=0 NormalY=0 NormalZ=1 AngleXU=0 Radius=0.5 StartAngle=0 EndAngle=1.5708
    g246: ArcOfCircle CenterX=412.528 CenterY=-93.1586 CenterZ=0 NormalX=0 NormalY=0 NormalZ=1 AngleXU=0 Radius=0.5 StartAngle=4.71239 EndAngle=6.28319
    g247: ArcOfCircle CenterX=399.528 CenterY=-93.1586 CenterZ=0 NormalX=0 NormalY=0 NormalZ=1 AngleXU=0 Radius=0.500001 StartAngle=3.14159 EndAngle=4.71239
    g248: LineSegment StartX=218.053 StartY=-64.5836 StartZ=0 EndX=218.056 EndY=-51.5847 EndZ=0
    g249: LineSegment StartX=232.053 StartY=-51.5836 StartZ=0 EndX=232.053 EndY=-64.5836 EndZ=0
    g250: LineSegment StartX=231.553 StartY=-65.0836 StartZ=0 EndX=218.553 EndY=-65.0836 EndZ=0
    g251: LineSegment StartX=218.556 StartY=-51.0847 StartZ=0 EndX=231.553 EndY=-51.0836 EndZ=0
    g252: ArcOfCircle CenterX=218.556 CenterY=-51.5847 CenterZ=0 NormalX=0 NormalY=0 NormalZ=1 AngleXU=0 Radius=0.500001 StartAngle=1.5708 EndAngle=3.14159
    g253: ArcOfCircle CenterX=231.553 CenterY=-51.5836 CenterZ=0 NormalX=0 NormalY=0 NormalZ=1 AngleXU=0 Radius=0.5 StartAngle=0 EndAngle=1.5708
    g254: ArcOfCircle CenterX=231.553 CenterY=-64.5836 CenterZ=0 NormalX=0 NormalY=0 NormalZ=1 AngleXU=0 Radius=0.5 StartAngle=4.71239 EndAngle=6.28319
    g255: ArcOfCircle CenterX=218.553 CenterY=-64.5836 CenterZ=0 NormalX=0 NormalY=0 NormalZ=1 AngleXU=0 Radius=0.500001 StartAngle=3.14159 EndAngle=4.71239
    g256: LineSegment StartX=208.528 StartY=-40.7711 StartZ=0 EndX=208.531 EndY=-27.7722 EndZ=0
    g257: LineSegment StartX=222.028 StartY=-41.2711 StartZ=0 EndX=209.028 EndY=-41.2711 EndZ=0
    g258: LineSegment StartX=209.031 StartY=-27.2722 StartZ=0 EndX=222.028 EndY=-27.2711 EndZ=0
    g259: LineSegment StartX=222.528 StartY=-27.7711 StartZ=0 EndX=222.528 EndY=-40.7711 EndZ=0
    g260: ArcOfCircle CenterX=209.028 CenterY=-40.7711 CenterZ=0 NormalX=0 NormalY=0 NormalZ=1 AngleXU=0 Radius=0.500001 StartAngle=3.14159 EndAngle=4.71239
    g261: ArcOfCircle CenterX=222.028 CenterY=-27.7711 CenterZ=0 NormalX=0 NormalY=0 NormalZ=1 AngleXU=0 Radius=0.5 StartAngle=0 EndAngle=1.5708
    g262: ArcOfCircle CenterX=209.031 CenterY=-27.7722 CenterZ=0 NormalX=0 NormalY=0 NormalZ=1 AngleXU=0 Radius=0.500001 StartAngle=1.5708 EndAngle=3.14159
    g263: ArcOfCircle CenterX=222.028 CenterY=-40.7711 CenterZ=0 NormalX=0 NormalY=0 NormalZ=1 AngleXU=0 Radius=0.5 StartAngle=4.71239 EndAngle=6.28319
    g264: LineSegment StartX=302.991 StartY=-84.1336 StartZ=0 EndX=289.991 EndY=-84.1336 EndZ=0
    g265: LineSegment StartX=289.491 StartY=-83.6336 StartZ=0 EndX=289.494 EndY=-70.6347 EndZ=0
    g266: LineSegment StartX=289.994 StartY=-70.1347 StartZ=0 EndX=302.991 EndY=-70.1336 EndZ=0
    g267: LineSegment StartX=303.491 StartY=-70.6336 StartZ=0 EndX=303.491 EndY=-83.6336 EndZ=0
    g268: ArcOfCircle CenterX=302.991 CenterY=-70.6336 CenterZ=0 NormalX=0 NormalY=0 NormalZ=1 AngleXU=0 Radius=0.5 StartAngle=0 EndAngle=1.5708
    g269: ArcOfCircle CenterX=289.994 CenterY=-70.6347 CenterZ=0 NormalX=0 NormalY=0 NormalZ=1 AngleXU=0 Radius=0.500001 StartAngle=1.5708 EndAngle=3.14159
    g270: ArcOfCircle CenterX=289.991 CenterY=-83.6336 CenterZ=0 NormalX=0 NormalY=0 NormalZ=1 AngleXU=0 Radius=0.500001 StartAngle=3.14159 EndAngle=4.71239
    g271: ArcOfCircle CenterX=302.991 CenterY=-83.6336 CenterZ=0 NormalX=0 NormalY=0 NormalZ=1 AngleXU=0 Radius=0.5 StartAngle=4.71239 EndAngle=6.28319
    g272: LineSegment StartX=318.569 StartY=-89.1847 StartZ=0 EndX=331.566 EndY=-89.1836 EndZ=0
    g273: LineSegment StartX=332.066 StartY=-89.6836 StartZ=0 EndX=332.066 EndY=-102.684 EndZ=0
    g274: LineSegment StartX=318.066 StartY=-102.684 StartZ=0 EndX=318.069 EndY=-89.6847 EndZ=0
    g275: LineSegment StartX=331.566 StartY=-103.184 StartZ=0 EndX=318.566 EndY=-103.184 EndZ=0
    g276: ArcOfCircle CenterX=331.566 CenterY=-102.684 CenterZ=0 NormalX=0 NormalY=0 NormalZ=1 AngleXU=0 Radius=0.5 StartAngle=4.71239 EndAngle=6.28319
    g277: ArcOfCircle CenterX=331.566 CenterY=-89.6836 CenterZ=0 NormalX=0 NormalY=0 NormalZ=1 AngleXU=0 Radius=0.5 StartAngle=0 EndAngle=1.5708
    g278: ArcOfCircle CenterX=318.566 CenterY=-102.684 CenterZ=0 NormalX=0 NormalY=0 NormalZ=1 AngleXU=0 Radius=0.500001 StartAngle=3.14159 EndAngle=4.71239
    g279: ArcOfCircle CenterX=318.569 CenterY=-89.6847 CenterZ=0 NormalX=0 NormalY=0 NormalZ=1 AngleXU=0 Radius=0.500001 StartAngle=1.5708 EndAngle=3.14159
    g280: LineSegment StartX=282.06 StartY=-108.734 StartZ=0 EndX=282.06 EndY=-121.734 EndZ=0
    g281: LineSegment StartX=268.06 StartY=-121.734 StartZ=0 EndX=268.062 EndY=-108.735 EndZ=0
    g282: LineSegment StartX=268.562 StartY=-108.235 StartZ=0 EndX=281.56 EndY=-108.234 EndZ=0
    g283: LineSegment StartX=281.56 StartY=-122.234 StartZ=0 EndX=268.56 EndY=-122.234 EndZ=0
    g284: ArcOfCircle CenterX=281.56 CenterY=-121.734 CenterZ=0 NormalX=0 NormalY=0 NormalZ=1 AngleXU=0 Radius=0.5 StartAngle=4.71239 EndAngle=6.28319
    g285: ArcOfCircle CenterX=268.562 CenterY=-108.735 CenterZ=0 NormalX=0 NormalY=0 NormalZ=1 AngleXU=0 Radius=0.500001 StartAngle=1.5708 EndAngle=3.14159
    g286: ArcOfCircle CenterX=268.56 CenterY=-121.734 CenterZ=0 NormalX=0 NormalY=0 NormalZ=1 AngleXU=0 Radius=0.500001 StartAngle=3.14159 EndAngle=4.71239
    g287: ArcOfCircle CenterX=281.56 CenterY=-108.734 CenterZ=0 NormalX=0 NormalY=0 NormalZ=1 AngleXU=0 Radius=0.5 StartAngle=0 EndAngle=1.5708
    g288: LineSegment StartX=393.978 StartY=-127.784 StartZ=0 EndX=393.978 EndY=-140.784 EndZ=0
    g289: LineSegment StartX=393.478 StartY=-141.284 StartZ=0 EndX=380.478 EndY=-141.284 EndZ=0
    g290: LineSegment StartX=380.481 StartY=-127.285 StartZ=0 EndX=393.478 EndY=-127.284 EndZ=0
    g291: LineSegment StartX=379.978 StartY=-140.784 StartZ=0 EndX=379.981 EndY=-127.785 EndZ=0
    g292: ArcOfCircle CenterX=380.478 CenterY=-140.784 CenterZ=0 NormalX=0 NormalY=0 NormalZ=1 AngleXU=0 Radius=0.500001 StartAngle=3.14159 EndAngle=4.71239
    g293: ArcOfCircle CenterX=393.478 CenterY=-140.784 CenterZ=0 NormalX=0 NormalY=0 NormalZ=1 AngleXU=0 Radius=0.5 StartAngle=4.71239 EndAngle=6.28319
    g294: ArcOfCircle CenterX=393.478 CenterY=-127.784 CenterZ=0 NormalX=0 NormalY=0 NormalZ=1 AngleXU=0 Radius=0.5 StartAngle=0 EndAngle=1.5708
    g295: ArcOfCircle CenterX=380.481 CenterY=-127.785 CenterZ=0 NormalX=0 NormalY=0 NormalZ=1 AngleXU=0 Radius=0.500001 StartAngle=1.5708 EndAngle=3.14159
    g296: LineSegment StartX=242.369 StartY=-108.235 StartZ=0 EndX=255.366 EndY=-108.234 EndZ=0
    g297: LineSegment StartX=255.866 StartY=-108.734 StartZ=0 EndX=255.866 EndY=-121.734 EndZ=0
    g298: LineSegment StartX=255.366 StartY=-122.234 StartZ=0 EndX=242.366 EndY=-122.234 EndZ=0
    g299: LineSegment StartX=241.866 StartY=-121.734 StartZ=0 EndX=241.869 EndY=-108.735 EndZ=0
    g300: ArcOfCircle CenterX=255.366 CenterY=-108.734 CenterZ=0 NormalX=0 NormalY=0 NormalZ=1 AngleXU=0 Radius=0.5 StartAngle=0 EndAngle=1.5708
    g301: ArcOfCircle CenterX=242.366 CenterY=-121.734 CenterZ=0 NormalX=0 NormalY=0 NormalZ=1 AngleXU=0 Radius=0.500001 StartAngle=3.14159 EndAngle=4.71239
    g302: ArcOfCircle CenterX=255.366 CenterY=-121.734 CenterZ=0 NormalX=0 NormalY=0 NormalZ=1 AngleXU=0 Radius=0.5 StartAngle=4.71239 EndAngle=6.28319
    g303: ArcOfCircle CenterX=242.369 CenterY=-108.735 CenterZ=0 NormalX=0 NormalY=0 NormalZ=1 AngleXU=0 Radius=0.500001 StartAngle=1.5708 EndAngle=3.14159
    g304: LineSegment StartX=98.2034 StartY=-65.0836 StartZ=0 EndX=85.2034 EndY=-65.0836 EndZ=0
    g305: LineSegment StartX=84.7034 StartY=-64.5836 StartZ=0 EndX=84.7062 EndY=-51.5847 EndZ=0
    g306: LineSegment StartX=85.2062 StartY=-51.0847 StartZ=0 EndX=98.2034 EndY=-51.0836 EndZ=0
    g307: LineSegment StartX=98.7034 StartY=-51.5836 StartZ=0 EndX=98.7034 EndY=-64.5836 EndZ=0
    g308: ArcOfCircle CenterX=85.2034 CenterY=-64.5836 CenterZ=0 NormalX=0 NormalY=0 NormalZ=1 AngleXU=0 Radius=0.500001 StartAngle=3.14159 EndAngle=4.71239
    g309: ArcOfCircle CenterX=85.2062 CenterY=-51.5847 CenterZ=0 NormalX=0 NormalY=0 NormalZ=1 AngleXU=0 Radius=0.500001 StartAngle=1.5708 EndAngle=3.14159
    g310: ArcOfCircle CenterX=98.2034 CenterY=-51.5836 CenterZ=0 NormalX=0 NormalY=0 NormalZ=1 AngleXU=0 Radius=0.5 StartAngle=0 EndAngle=1.5708
    g311: ArcOfCircle CenterX=98.2034 CenterY=-64.5836 CenterZ=0 NormalX=0 NormalY=0 NormalZ=1 AngleXU=0 Radius=0.5 StartAngle=4.71239 EndAngle=6.28319
    g312: LineSegment StartX=318.066 StartY=-121.734 StartZ=0 EndX=318.069 EndY=-108.735 EndZ=0
    g313: LineSegment StartX=318.569 StartY=-108.235 StartZ=0 EndX=331.566 EndY=-108.234 EndZ=0
    g314: LineSegment StartX=331.566 StartY=-122.234 StartZ=0 EndX=318.566 EndY=-122.234 EndZ=0
    g315: LineSegment StartX=332.066 StartY=-108.734 StartZ=0 EndX=332.066 EndY=-121.734 EndZ=0
    g316: ArcOfCircle CenterX=318.566 CenterY=-121.734 CenterZ=0 NormalX=0 NormalY=0 NormalZ=1 AngleXU=0 Radius=0.500001 StartAngle=3.14159 EndAngle=4.71239
    g317: ArcOfCircle CenterX=331.566 CenterY=-108.734 CenterZ=0 NormalX=0 NormalY=0 NormalZ=1 AngleXU=0 Radius=0.5 StartAngle=0 EndAngle=1.5708
    g318: ArcOfCircle CenterX=318.569 CenterY=-108.735 CenterZ=0 NormalX=0 NormalY=0 NormalZ=1 AngleXU=0 Radius=0.500001 StartAngle=1.5708 EndAngle=3.14159
    g319: ArcOfCircle CenterX=331.566 CenterY=-121.734 CenterZ=0 NormalX=0 NormalY=0 NormalZ=1 AngleXU=0 Radius=0.5 StartAngle=4.71239 EndAngle=6.28319
    g320: LineSegment StartX=70.1284 StartY=-70.6336 StartZ=0 EndX=70.1284 EndY=-83.6336 EndZ=0
    g321: LineSegment StartX=69.6284 StartY=-84.1336 StartZ=0 EndX=56.6284 EndY=-84.1336 EndZ=0
    g322: LineSegment StartX=56.1284 StartY=-83.6336 StartZ=0 EndX=56.1312 EndY=-70.6347 EndZ=0
    g323: LineSegment StartX=56.6312 StartY=-70.1347 StartZ=0 EndX=69.6284 EndY=-70.1336 EndZ=0
    g324: ArcOfCircle CenterX=69.6284 CenterY=-83.6336 CenterZ=0 NormalX=0 NormalY=0 NormalZ=1 AngleXU=0 Radius=0.5 StartAngle=4.71239 EndAngle=6.28319
    g325: ArcOfCircle CenterX=69.6284 CenterY=-70.6336 CenterZ=0 NormalX=0 NormalY=0 NormalZ=1 AngleXU=0 Radius=0.5 StartAngle=0 EndAngle=1.5708
    g326: ArcOfCircle CenterX=56.6284 CenterY=-83.6336 CenterZ=0 NormalX=0 NormalY=0 NormalZ=1 AngleXU=0 Radius=0.500001 StartAngle=3.14159 EndAngle=4.71239
    g327: ArcOfCircle CenterX=56.6312 CenterY=-70.6347 CenterZ=0 NormalX=0 NormalY=0 NormalZ=1 AngleXU=0 Radius=0.500001 StartAngle=1.5708 EndAngle=3.14159
    g328: LineSegment StartX=300.607 StartY=-141.282 StartZ=0 EndX=287.607 EndY=-141.282 EndZ=0
    g329: LineSegment StartX=287.107 StartY=-140.782 StartZ=0 EndX=287.109 EndY=-127.783 EndZ=0
    g330: LineSegment StartX=301.107 StartY=-127.782 StartZ=0 EndX=301.107 EndY=-140.782 EndZ=0
    g331: LineSegment StartX=287.609 StartY=-127.283 StartZ=0 EndX=300.607 EndY=-127.282 EndZ=0
    g332: ArcOfCircle CenterX=300.607 CenterY=-127.782 CenterZ=0 NormalX=0 NormalY=0 NormalZ=1 AngleXU=0 Radius=0.5 StartAngle=0 EndAngle=1.5708
    g333: ArcOfCircle CenterX=287.607 CenterY=-140.782 CenterZ=0 NormalX=0 NormalY=0 NormalZ=1 AngleXU=0 Radius=0.500001 StartAngle=3.14159 EndAngle=4.71239
    g334: ArcOfCircle CenterX=287.609 CenterY=-127.783 CenterZ=0 NormalX=0 NormalY=0 NormalZ=1 AngleXU=0 Radius=0.500001 StartAngle=1.5708 EndAngle=3.14159
    g335: ArcOfCircle CenterX=300.607 CenterY=-140.782 CenterZ=0 NormalX=0 NormalY=0 NormalZ=1 AngleXU=0 Radius=0.5 StartAngle=4.71239 EndAngle=6.28319
    g336: LineSegment StartX=103.466 StartY=-108.734 StartZ=0 EndX=103.466 EndY=-121.734 EndZ=0
    g337: LineSegment StartX=89.9687 StartY=-108.235 StartZ=0 EndX=102.966 EndY=-108.234 EndZ=0
    g338: LineSegment StartX=89.4659 StartY=-121.734 StartZ=0 EndX=89.4687 EndY=-108.735 EndZ=0
    g339: LineSegment StartX=102.966 StartY=-122.234 StartZ=0 EndX=89.9659 EndY=-122.234 EndZ=0
    g340: ArcOfCircle CenterX=89.9659 CenterY=-121.734 CenterZ=0 NormalX=0 NormalY=0 NormalZ=1 AngleXU=0 Radius=0.500001 StartAngle=3.14159 EndAngle=4.71239
    g341: ArcOfCircle CenterX=89.9687 CenterY=-108.735 CenterZ=0 NormalX=0 NormalY=0 NormalZ=1 AngleXU=0 Radius=0.500001 StartAngle=1.5708 EndAngle=3.14159
    g342: ArcOfCircle CenterX=102.966 CenterY=-108.734 CenterZ=0 NormalX=0 NormalY=0 NormalZ=1 AngleXU=0 Radius=0.5 StartAngle=0 EndAngle=1.5708
    g343: ArcOfCircle CenterX=102.966 CenterY=-121.734 CenterZ=0 NormalX=0 NormalY=0 NormalZ=1 AngleXU=0 Radius=0.5 StartAngle=4.71239 EndAngle=6.28319
    g344: LineSegment StartX=179.953 StartY=-64.5836 StartZ=0 EndX=179.956 EndY=-51.5847 EndZ=0
    g345: LineSegment StartX=180.456 StartY=-51.0847 StartZ=0 EndX=193.453 EndY=-51.0836 EndZ=0
    g346: LineSegment StartX=193.953 StartY=-51.5836 StartZ=0 EndX=193.953 EndY=-64.5836 EndZ=0
    g347: LineSegment StartX=193.453 StartY=-65.0836 StartZ=0 EndX=180.453 EndY=-65.0836 EndZ=0
    g348: ArcOfCircle CenterX=193.453 CenterY=-51.5836 CenterZ=0 NormalX=0 NormalY=0 NormalZ=1 AngleXU=0 Radius=0.5 StartAngle=0 EndAngle=1.5708
    g349: ArcOfCircle CenterX=180.453 CenterY=-64.5836 CenterZ=0 NormalX=0 NormalY=0 NormalZ=1 AngleXU=0 Radius=0.500001 StartAngle=3.14159 EndAngle=4.71239
    g350: ArcOfCircle CenterX=180.456 CenterY=-51.5847 CenterZ=0 NormalX=0 NormalY=0 NormalZ=1 AngleXU=0 Radius=0.500001 StartAngle=1.5708 EndAngle=3.14159
    g351: ArcOfCircle CenterX=193.453 CenterY=-64.5836 CenterZ=0 NormalX=0 NormalY=0 NormalZ=1 AngleXU=0 Radius=0.5 StartAngle=4.71239 EndAngle=6.28319
    g352: LineSegment StartX=355.878 StartY=-108.734 StartZ=0 EndX=355.878 EndY=-121.734 EndZ=0
    g353: LineSegment StartX=341.878 StartY=-121.734 StartZ=0 EndX=341.881 EndY=-108.735 EndZ=0
    g354: LineSegment StartX=342.381 StartY=-108.235 StartZ=0 EndX=355.378 EndY=-108.234 EndZ=0
    g355: LineSegment StartX=355.378 StartY=-122.234 StartZ=0 EndX=342.378 EndY=-122.234 EndZ=0
    g356: ArcOfCircle CenterX=342.381 CenterY=-108.735 CenterZ=0 NormalX=0 NormalY=0 NormalZ=1 AngleXU=0 Radius=0.500001 StartAngle=1.5708 EndAngle=3.14159
    g357: ArcOfCircle CenterX=342.378 CenterY=-121.734 CenterZ=0 NormalX=0 NormalY=0 NormalZ=1 AngleXU=0 Radius=0.500001 StartAngle=3.14159 EndAngle=4.71239
    g358: ArcOfCircle CenterX=355.378 CenterY=-121.734 CenterZ=0 NormalX=0 NormalY=0 NormalZ=1 AngleXU=0 Radius=0.5 StartAngle=4.71239 EndAngle=6.28319
    g359: ArcOfCircle CenterX=355.378 CenterY=-108.734 CenterZ=0 NormalX=0 NormalY=0 NormalZ=1 AngleXU=0 Radius=0.5 StartAngle=0 EndAngle=1.5708
    g360: LineSegment StartX=98.2034 StartY=-41.2711 StartZ=0 EndX=85.2034 EndY=-41.2711 EndZ=0
    g361: LineSegment StartX=84.7034 StartY=-40.7711 StartZ=0 EndX=84.7062 EndY=-27.7722 EndZ=0
    g362: LineSegment StartX=98.7034 StartY=-27.7711 StartZ=0 EndX=98.7034 EndY=-40.7711 EndZ=0
    g363: LineSegment StartX=85.2062 StartY=-27.2722 StartZ=0 EndX=98.2034 EndY=-27.2711 EndZ=0
    g364: ArcOfCircle CenterX=85.2062 CenterY=-27.7722 CenterZ=0 NormalX=0 NormalY=0 NormalZ=1 AngleXU=0 Radius=0.500001 StartAngle=1.5708 EndAngle=3.14159
    g365: ArcOfCircle CenterX=98.2034 CenterY=-27.7711 CenterZ=0 NormalX=0 NormalY=0 NormalZ=1 AngleXU=0 Radius=0.5 StartAngle=0 EndAngle=1.5708
    g366: ArcOfCircle CenterX=98.2034 CenterY=-40.7711 CenterZ=0 NormalX=0 NormalY=0 NormalZ=1 AngleXU=0 Radius=0.5 StartAngle=4.71239 EndAngle=6.28319
    g367: ArcOfCircle CenterX=85.2034 CenterY=-40.7711 CenterZ=0 NormalX=0 NormalY=0 NormalZ=1 AngleXU=0 Radius=0.500001 StartAngle=3.14159 EndAngle=4.71239
    g368: LineSegment StartX=355.878 StartY=-89.6836 StartZ=0 EndX=355.878 EndY=-102.684 EndZ=0
    g369: LineSegment StartX=342.381 StartY=-89.1847 StartZ=0 EndX=355.378 EndY=-89.1836 EndZ=0
    g370: LineSegment StartX=355.378 StartY=-103.184 StartZ=0 EndX=342.378 EndY=-103.184 EndZ=0
    g371: LineSegment StartX=341.878 StartY=-102.684 StartZ=0 EndX=341.881 EndY=-89.6847 EndZ=0
    g372: ArcOfCircle CenterX=355.378 CenterY=-89.6836 CenterZ=0 NormalX=0 NormalY=0 NormalZ=1 AngleXU=0 Radius=0.5 StartAngle=0 EndAngle=1.5708
    g373: ArcOfCircle CenterX=342.378 CenterY=-102.684 CenterZ=0 NormalX=0 NormalY=0 NormalZ=1 AngleXU=0 Radius=0.500001 StartAngle=3.14159 EndAngle=4.71239
    g374: ArcOfCircle CenterX=355.378 CenterY=-102.684 CenterZ=0 NormalX=0 NormalY=0 NormalZ=1 AngleXU=0 Radius=0.5 StartAngle=4.71239 EndAngle=6.28319
    g375: ArcOfCircle CenterX=342.381 CenterY=-89.6847 CenterZ=0 NormalX=0 NormalY=0 NormalZ=1 AngleXU=0 Radius=0.500001 StartAngle=1.5708 EndAngle=3.14159
    g376: LineSegment StartX=165.378 StartY=-27.7711 StartZ=0 EndX=165.378 EndY=-40.7711 EndZ=0
    g377: LineSegment StartX=164.878 StartY=-41.2711 StartZ=0 EndX=151.878 EndY=-41.2711 EndZ=0
    g378: LineSegment StartX=151.378 StartY=-40.7711 StartZ=0 EndX=151.381 EndY=-27.7722 EndZ=0
    g379: LineSegment StartX=151.881 StartY=-27.2722 StartZ=0 EndX=164.878 EndY=-27.2711 EndZ=0
    g380: ArcOfCircle CenterX=151.878 CenterY=-40.7711 CenterZ=0 NormalX=0 NormalY=0 NormalZ=1 AngleXU=0 Radius=0.500001 StartAngle=3.14159 EndAngle=4.71239
    g381: ArcOfCircle CenterX=151.881 CenterY=-27.7722 CenterZ=0 NormalX=0 NormalY=0 NormalZ=1 AngleXU=0 Radius=0.500001 StartAngle=1.5708 EndAngle=3.14159
    g382: ArcOfCircle CenterX=164.878 CenterY=-27.7711 CenterZ=0 NormalX=0 NormalY=0 NormalZ=1 AngleXU=0 Radius=0.5 StartAngle=0 EndAngle=1.5708
    g383: ArcOfCircle CenterX=164.878 CenterY=-40.7711 CenterZ=0 NormalX=0 NormalY=0 NormalZ=1 AngleXU=0 Radius=0.5 StartAngle=4.71239 EndAngle=6.28319
    g384: LineSegment StartX=222.816 StartY=-121.734 StartZ=0 EndX=222.819 EndY=-108.735 EndZ=0
    g385: LineSegment StartX=236.816 StartY=-108.734 StartZ=0 EndX=236.816 EndY=-121.734 EndZ=0
    g386: LineSegment StartX=223.319 StartY=-108.235 StartZ=0 EndX=236.316 EndY=-108.234 EndZ=0
    g387: LineSegment StartX=236.316 StartY=-122.234 StartZ=0 EndX=223.316 EndY=-122.234 EndZ=0
    g388: ArcOfCircle CenterX=223.319 CenterY=-108.735 CenterZ=0 NormalX=0 NormalY=0 NormalZ=1 AngleXU=0 Radius=0.500001 StartAngle=1.5708 EndAngle=3.14159
    g389: ArcOfCircle CenterX=223.316 CenterY=-121.734 CenterZ=0 NormalX=0 NormalY=0 NormalZ=1 AngleXU=0 Radius=0.500001 StartAngle=3.14159 EndAngle=4.71239
    g390: ArcOfCircle CenterX=236.316 CenterY=-108.734 CenterZ=0 NormalX=0 NormalY=0 NormalZ=1 AngleXU=0 Radius=0.5 StartAngle=0 EndAngle=1.5708
    g391: ArcOfCircle CenterX=236.316 CenterY=-121.734 CenterZ=0 NormalX=0 NormalY=0 NormalZ=1 AngleXU=0 Radius=0.5 StartAngle=4.71239 EndAngle=6.28319
    g392: LineSegment StartX=194.744 StartY=-89.1847 StartZ=0 EndX=207.741 EndY=-89.1836 EndZ=0
    g393: LineSegment StartX=208.241 StartY=-89.6836 StartZ=0 EndX=208.241 EndY=-102.684 EndZ=0
    g394: LineSegment StartX=194.241 StartY=-102.684 StartZ=0 EndX=194.244 EndY=-89.6847 EndZ=0
    g395: LineSegment StartX=207.741 StartY=-103.184 StartZ=0 EndX=194.741 EndY=-103.184 EndZ=0
    g396: ArcOfCircle CenterX=194.741 CenterY=-102.684 CenterZ=0 NormalX=0 NormalY=0 NormalZ=1 AngleXU=0 Radius=0.500001 StartAngle=3.14159 EndAngle=4.71239
    g397: ArcOfCircle CenterX=207.741 CenterY=-102.684 CenterZ=0 NormalX=0 NormalY=0 NormalZ=1 AngleXU=0 Radius=0.5 StartAngle=4.71239 EndAngle=6.28319
    g398: ArcOfCircle CenterX=207.741 CenterY=-89.6836 CenterZ=0 NormalX=0 NormalY=0 NormalZ=1 AngleXU=0 Radius=0.5 StartAngle=0 EndAngle=1.5708
    g399: ArcOfCircle CenterX=194.744 CenterY=-89.6847 CenterZ=0 NormalX=0 NormalY=0 NormalZ=1 AngleXU=0 Radius=0.500001 StartAngle=1.5708 EndAngle=3.14159
    ... +522 more geometry lines
  constraints (1850):
    c: Block(g0)
    c: Block(g1)
    c: Block(g2)
    c: Block(g3)
    c: Block(g4)
    c: Block(g5)
    c: Block(g6)
    c: Block(g7)
    c: Block(g8)
    c: Block(g9)
    c: Block(g10)
    c: Block(g11)
    c: Block(g12)
    c: Block(g13)
    c: Block(g14)
    c: Block(g15)
    c: Block(g16)
    c: Block(g17)
    c: Block(g18)
    c: Block(g19)
    c: Block(g20)
    c: Block(g21)
    c: Block(g22)
    c: Block(g23)
    c: Block(g24)
    c: Block(g25)
    c: Block(g26)
    c: Block(g27)
    c: Block(g28)
    c: Block(g29)
    c: Block(g30)
    c: Block(g31)
    c: Block(g32)
    c: Block(g33)
    c: Block(g34)
    c: Block(g35)
    c: Block(g36)
    c: Block(g37)
    c: Block(g38)
    c: Block(g39)
    c: Block(g40)
    c: Block(g41)
    c: Block(g42)
    c: Block(g43)
    c: Block(g44)
    c: Block(g45)
    c: Block(g46)
    c: Block(g47)
    c: Block(g48)
    c: Block(g49)
    c: Block(g50)
    c: Block(g51)
    c: Block(g52)
    c: Block(g53)
    c: Block(g54)
    c: Block(g55)
    c: Block(g56)
    c: Block(g57)
    c: Block(g58)
    c: Block(g59)
    c: Block(g60)
    c: Block(g61)
    c: Block(g62)
    c: Block(g63)
    c: Block(g64)
    c: Block(g65)
    c: Block(g66)
    c: Block(g67)
    c: Block(g68)
    c: Block(g69)
    c: Block(g70)
    c: Block(g71)
    c: Block(g72)
    c: Block(g73)
    c: Block(g74)
    c: Block(g75)
    c: Block(g76)
    c: Block(g77)
    c: Block(g78)
    c: Block(g79)
    c: Block(g80)
    c: Block(g81)
    c: Block(g82)
    c: Block(g83)
    c: Block(g84)
    c: Block(g85)
    c: Block(g86)
    c: Block(g87)
    c: Block(g88)
    c: Block(g89)
    c: Block(g90)
    c: Block(g91)
    c: Block(g92)
    c: Block(g93)
    c: Block(g94)
    c: Block(g95)
    c: Block(g96)
    c: Block(g97)
    c: Block(g98)
    c: Block(g99)
    c: Block(g100)
    c: Block(g101)
    c: Block(g102)
    c: Block(g103)
    c: Block(g104)
    c: Block(g105)
    c: Block(g106)
    c: Block(g107)
    c: Block(g108)
    c: Block(g109)
    c: Block(g110)
    c: Block(g111)
    c: Block(g112)
    c: Block(g113)
    c: Block(g114)
    c: Block(g115)
    c: Block(g116)
    c: Block(g117)
    c: Block(g118)
    c: Block(g119)
    c: Block(g120)
    c: Block(g121)
    c: Block(g122)
    c: Block(g123)
    c: Block(g124)
    c: Block(g125)
    c: Block(g126)
    c: Block(g127)
    c: Block(g128)
    c: Block(g129)
    c: Block(g130)
    c: Block(g131)
    c: Block(g132)
    c: Block(g133)
    c: Block(g134)
    c: Block(g135)
    c: Block(g136)
    c: Block(g137)
    c: Block(g138)
    c: Block(g139)
    c: Block(g140)
    c: Block(g141)
    c: Block(g142)
    c: Block(g143)
    c: Block(g144)
    c: Block(g145)
    c: Block(g146)
    c: Block(g147)
    c: Block(g148)
    c: Block(g149)
    c: Block(g150)
    c: Block(g151)
    c: Block(g152)
    c: Block(g153)
    c: Block(g154)
    c: Block(g155)
    c: Block(g156)
    c: Block(g157)
    c: Block(g158)
    c: Block(g159)
    c: Block(g160)
    c: Block(g161)
    c: Block(g162)
    c: Block(g163)
    c: Block(g164)
    c: Block(g165)
    c: Block(g166)
    c: Block(g167)
    c: Block(g168)
    c: Block(g169)
    c: Block(g170)
    c: Block(g171)
    c: Block(g172)
    c: Block(g173)
    c: Block(g174)
    c: Block(g175)
    c: Block(g176)
    c: Block(g177)
    c: Block(g178)
    c: Block(g179)
    c: Block(g180)
    c: Block(g181)
    c: Block(g182)
    c: Block(g183)
    c: Block(g184)
    c: Block(g185)
    c: Block(g186)
    c: Block(g187)
    c: Block(g188)
    c: Block(g189)
    c: Block(g190)
    c: Block(g191)
    c: Block(g192)
    c: Block(g193)
    c: Block(g194)
    c: Block(g195)
    c: Block(g196)
    c: Block(g197)
    c: Block(g198)
    c: Block(g199)
    c: Block(g200)
    c: Block(g201)
    c: Block(g202)
    c: Block(g203)
    c: Block(g204)
    c: Block(g205)
    c: Block(g206)
    c: Block(g207)
    c: Block(g208)
    c: Block(g209)
    c: Block(g210)
    c: Block(g211)
    c: Block(g212)
    c: Block(g213)
    c: Block(g214)
    c: Block(g215)
    c: Block(g216)
    c: Block(g217)
    c: Block(g218)
    c: Block(g219)
    c: Block(g220)
    c: Block(g221)
    c: Block(g222)
    c: Block(g223)
    c: Block(g224)
    c: Block(g225)
    c: Block(g226)
    c: Block(g227)
    c: Block(g228)
    c: Block(g229)
    c: Block(g230)
    c: Block(g231)
    c: Block(g232)
    c: Block(g233)
    c: Block(g234)
    c: Block(g235)
    c: Block(g236)
    c: Block(g237)
    c: Block(g238)
    c: Block(g239)
    c: Block(g240)
    c: Block(g241)
    c: Block(g242)
    c: Block(g243)
    c: Block(g244)
    c: Block(g245)
    c: Block(g246)
    c: Block(g247)
    c: Block(g248)
    c: Block(g249)
    c: Block(g250)
    c: Block(g251)
    c: Block(g252)
    c: Block(g253)
    c: Block(g254)
    c: Block(g255)
    c: Block(g256)
    c: Block(g257)
    c: Block(g258)
    c: Block(g259)
    c: Block(g260)
    c: Block(g261)
    c: Block(g262)
    c: Block(g263)
    c: Block(g264)
    c: Block(g265)
    c: Block(g266)
    c: Block(g267)
    c: Block(g268)
    c: Block(g269)
    c: Block(g270)
    c: Block(g271)
    c: Block(g272)
    c: Block(g273)
    c: Block(g274)
    c: Block(g275)
    c: Block(g276)
    c: Block(g277)
    c: Block(g278)
    c: Block(g279)
    c: Block(g280)
    c: Block(g281)
    c: Block(g282)
    c: Block(g283)
    c: Block(g284)
    c: Block(g285)
    c: Block(g286)
    c: Block(g287)
    c: Block(g288)
    c: Block(g289)
    c: Block(g290)
    c: Block(g291)
    c: Block(g292)
    c: Block(g293)
    c: Block(g294)
    c: Block(g295)
    c: Block(g296)
    c: Block(g297)
    c: Block(g298)
    c: Block(g299)
    c: Block(g300)
    c: Block(g301)
    c: Block(g302)
    c: Block(g303)
    c: Block(g304)
    c: Block(g305)
    c: Block(g306)
    c: Block(g307)
    c: Block(g308)
    c: Block(g309)
    c: Block(g310)
    c: Block(g311)
    c: Block(g312)
    c: Block(g313)
    c: Block(g314)
    c: Block(g315)
    c: Block(g316)
    c: Block(g317)
    c: Block(g318)
    c: Block(g319)
    c: Block(g320)
    c: Block(g321)
    c: Block(g322)
    c: Block(g323)
    c: Block(g324)
    c: Block(g325)
    c: Block(g326)
    c: Block(g327)
    c: Block(g328)
    c: Block(g329)
    c: Block(g330)
    c: Block(g331)
    c: Block(g332)
    c: Block(g333)
    c: Block(g334)
    c: Block(g335)
    c: Block(g336)
    c: Block(g337)
    c: Block(g338)
    c: Block(g339)
    c: Block(g340)
    c: Block(g341)
    c: Block(g342)
    c: Block(g343)
    c: Block(g344)
    c: Block(g345)
    c: Block(g346)
    c: Block(g347)
    c: Block(g348)
    c: Block(g349)
    c: Block(g350)
    c: Block(g351)
    c: Block(g352)
    c: Block(g353)
    c: Block(g354)
    c: Block(g355)
    c: Block(g356)
    c: Block(g357)
    c: Block(g358)
    c: Block(g359)
    c: Block(g360)
    c: Block(g361)
    c: Block(g362)
    c: Block(g363)
    c: Block(g364)
    c: Block(g365)
    c: Block(g366)
    c: Block(g367)
    c: Block(g368)
    c: Block(g369)
    c: Block(g370)
    c: Block(g371)
    c: Block(g372)
    c: Block(g373)
    c: Block(g374)
    c: Block(g375)
    c: Block(g376)
    c: Block(g377)
    c: Block(g378)
    c: Block(g379)
    c: Block(g380)
    c: Block(g381)
    c: Block(g382)
    c: Block(g383)
    c: Block(g384)
    c: Block(g385)
    c: Block(g386)
    c: Block(g387)
    c: Block(g388)
    c: Block(g389)
    c: Block(g390)
    c: Block(g391)
    c: Block(g392)
    c: Block(g393)
    c: Block(g394)
    c: Block(g395)
    c: Block(g396)
    c: Block(g397)
    c: Block(g398)
    c: Block(g399)
    c: Block(g400)
    c: Block(g401)
    c: Block(g402)
    c: Block(g403)
    c: Block(g404)
    c: Block(g405)
    c: Block(g406)
    c: Block(g407)
    c: Block(g408)
    c: Block(g409)
    c: Block(g410)
    c: Block(g411)
    c: Block(g412)
    c: Block(g413)
    c: Block(g414)
    c: Block(g415)
    c: Block(g416)
    c: Block(g417)
    c: Block(g418)
    c: Block(g419)
    c: Block(g420)
    c: Block(g421)
    c: Block(g422)
    c: Block(g423)
    c: Block(g424)
    c: Block(g425)
    c: Block(g426)
    c: Block(g427)
    c: Block(g428)
    c: Block(g429)
    c: Block(g430)
    c: Block(g431)
    c: Block(g432)
    c: Block(g433)
    c: Block(g434)
    c: Block(g435)
    c: Block(g436)
    c: Block(g437)
    c: Block(g438)
    c: Block(g439)
    c: Block(g440)
    c: Block(g441)
    c: Block(g442)
    c: Block(g443)
    c: Block(g444)
    c: Block(g445)
    c: Block(g446)
    c: Block(g447)
    c: Block(g448)
    c: Block(g449)
    c: Block(g450)
    c: Block(g451)
    c: Block(g452)
    c: Block(g453)
    c: Block(g454)
    c: Block(g455)
    c: Block(g456)
    c: Block(g457)
    c: Block(g458)
    c: Block(g459)
    c: Block(g460)
    c: Block(g461)
    c: Block(g462)
    c: Block(g463)
    c: Block(g464)
    c: Block(g465)
    c: Block(g466)
    c: Block(g467)
    c: Block(g468)
    c: Block(g469)
    c: Block(g470)
    c: Block(g471)
    c: Block(g472)
    c: Block(g473)
    c: Block(g474)
    c: Block(g475)
    c: Block(g476)
    c: Block(g477)
    c: Block(g478)
    c: Block(g479)
    c: Block(g480)
    c: Block(g481)
    c: Block(g482)
    c: Block(g483)
    c: Block(g484)
    c: Block(g485)
    c: Block(g486)
    c: Block(g487)
    c: Block(g488)
    c: Block(g489)
    c: Block(g490)
    c: Block(g491)
    c: Block(g492)
    c: Block(g493)
    c: Block(g494)
    c: Block(g495)
    c: Block(g496)
    c: Block(g497)
    c: Block(g498)
    c: Block(g499)
    c: Block(g500)
    c: Block(g501)
    c: Block(g502)
    c: Block(g503)
    c: Block(g504)
    c: Block(g505)
    c: Block(g506)
    c: Block(g507)
    c: Block(g508)
    c: Block(g509)
    c: Block(g510)
    c: Block(g511)
    c: Block(g512)
    c: Block(g513)
    c: Block(g514)
    c: Block(g515)
    c: Block(g516)
    c: Block(g517)
    c: Block(g518)
    c: Block(g519)
    c: Block(g520)
    c: Block(g521)
    c: Block(g522)
    c: Block(g523)
    c: Block(g524)
    c: Block(g525)
    c: Block(g526)
    c: Block(g527)
    c: Block(g528)
    c: Block(g529)
    c: Block(g530)
    c: Block(g531)
    c: Block(g532)
    c: Block(g533)
    c: Block(g534)
    c: Block(g535)
    c: Block(g536)
    c: Block(g537)
    c: Block(g538)
    c: Block(g539)
    c: Block(g540)
    c: Block(g541)
    c: Block(g542)
    c: Block(g543)
    c: Block(g544)
    c: Block(g545)
    c: Block(g546)
    c: Block(g547)
    c: Block(g548)
    c: Block(g549)
    c: Block(g550)
    c: Block(g551)
    c: Block(g552)
    c: Block(g553)
    c: Block(g554)
    c: Block(g555)
    c: Block(g556)
    c: Block(g557)
    c: Block(g558)
    c: Block(g559)
    c: Block(g560)
    c: Block(g561)
    c: Block(g562)
    c: Block(g563)
    c: Block(g564)
    c: Block(g565)
    c: Block(g566)
    c: Block(g567)
    c: Block(g568)
    c: Block(g569)
    c: Block(g570)
    c: Block(g571)
    c: Block(g572)
    c: Block(g573)
    c: Block(g574)
    c: Block(g575)
    c: Block(g576)
    c: Block(g577)
    c: Block(g578)
    c: Block(g579)
    c: Block(g580)
    c: Block(g581)
    c: Block(g582)
    c: Block(g583)
    c: Block(g584)
    c: Block(g585)
    c: Block(g586)
    c: Block(g587)
    c: Block(g588)
    c: Block(g589)
    c: Block(g590)
    c: Block(g591)
    c: Block(g592)
    c: Block(g593)
    c: Block(g594)
    c: Block(g595)
    c: Block(g596)
    c: Block(g597)
    c: Block(g598)
    c: Block(g599)
    c: Block(g600)
    c: Block(g601)
    c: Block(g602)
    c: Block(g603)
    c: Block(g604)
    c: Block(g605)
    c: Block(g606)
    c: Block(g607)
    c: Block(g608)
    c: Block(g609)
    c: Block(g610)
    c: Block(g611)
    c: Block(g612)
    c: Block(g613)
    c: Block(g614)
    c: Block(g615)
    c: Block(g616)
    c: Block(g617)
    c: Block(g618)
    c: Block(g619)
    c: Block(g620)
    c: Block(g621)
    c: Block(g622)
    c: Block(g623)
    c: Block(g624)
    c: Block(g625)
    c: Block(g626)
    c: Block(g627)
    c: Block(g628)
    c: Block(g629)
    c: Block(g630)
    c: Block(g631)
    c: Block(g632)
    c: Block(g633)
    c: Block(g634)
    c: Block(g635)
    c: Block(g636)
    c: Block(g637)
    c: Block(g638)
    c: Block(g639)
    c: Block(g640)
    c: Block(g641)
    c: Block(g642)
    c: Block(g643)
    c: Block(g644)
    c: Block(g645)
    c: Block(g646)
    c: Block(g647)
    c: Block(g648)
    c: Block(g649)
    c: Block(g650)
    c: Block(g651)
    c: Block(g652)
    c: Block(g653)
    c: Block(g654)
    c: Block(g655)
    c: Block(g656)
    c: Block(g657)
    c: Block(g658)
    c: Block(g659)
    c: Block(g660)
    c: Block(g661)
    c: Block(g662)
    c: Block(g663)
    c: Block(g664)
    c: Block(g665)
    c: Block(g666)
    c: Block(g667)
    c: Block(g668)
    c: Block(g669)
    c: Block(g670)
    c: Block(g671)
    c: Block(g672)
    c: Block(g673)
    c: Block(g674)
    c: Block(g675)
    c: Block(g676)
    c: Block(g677)
    c: Block(g678)
    c: Block(g679)
    c: Block(g680)
    c: Block(g681)
    c: Block(g682)
    c: Block(g683)
    c: Block(g684)
    c: Block(g685)
    c: Block(g686)
    c: Block(g687)
    c: Block(g688)
    c: Block(g689)
    c: Block(g690)
    c: Block(g691)
    c: Block(g692)
    c: Block(g693)
    c: Block(g694)
    c: Block(g695)
    c: Block(g696)
    c: Block(g697)
    c: Block(g698)
    c: Block(g699)
    c: Block(g700)
    c: Block(g701)
    c: Block(g702)
    c: Block(g703)
    c: Block(g704)
    c: Block(g705)
    c: Block(g706)
    c: Block(g707)
    c: Block(g708)
    c: Block(g709)
    c: Block(g710)
    c: Block(g711)
    c: Block(g712)
    c: Block(g713)
    c: Block(g714)
    c: Block(g715)
    c: Block(g716)
    c: Block(g717)
    c: Block(g718)
    c: Block(g719)
    c: Block(g720)
    c: Block(g721)
    c: Block(g722)
    c: Block(g723)
    c: Block(g724)
    c: Block(g725)
    c: Block(g726)
    c: Block(g727)
    c: Block(g728)
    c: Block(g729)
    c: Block(g730)
    c: Block(g731)
    c: Block(g732)
    c: Block(g733)
    c: Block(g734)
    c: Block(g735)
    c: Block(g736)
    c: Block(g737)
    c: Block(g738)
    c: Block(g739)
    c: Block(g740)
    c: Block(g741)
    c: Block(g742)
    c: Block(g743)
    c: Block(g744)
    c: Block(g745)
    c: Block(g746)
    c: Block(g747)
    c: Block(g748)
    c: Block(g749)
    c: Block(g750)
    c: Block(g751)
    c: Block(g752)
    c: Block(g753)
    c: Block(g754)
    c: Block(g755)
    c: Block(g756)
    c: Block(g757)
    c: Block(g758)
    c: Block(g759)
    c: Block(g761)
    c: Block(g762)
    c: Block(g763)
    c: Block(g764)
    c: Block(g765)
    c: Block(g766)
    c: Block(g767)
    c: Block(g768)
    c: Block(g769)
    c: Block(g770)
    c: Block(g771)
    c: Block(g772)
    c: Block(g773)
    c: Block(g774)
    c: Block(g775)
    c: Block(g776)
    c: Block(g777)
    c: Block(g778)
    c: Block(g779)
    c: Block(g780)
    c: Block(g781)
    c: Block(g782)
    c: Block(g783)
    c: Block(g784)
    c: Block(g785)
    c: Block(g786)
    c: Block(g787)
    c: Block(g788)
    c: Block(g789)
    c: Block(g790)
    c: Block(g791)
    c: Block(g792)
    c: Block(g793)
    c: Block(g794)
    c: Block(g795)
    c: Block(g796)
    c: Block(g797)
    c: Block(g798)
    c: Block(g799)
    c: Block(g800)
    c: Block(g801)
    c: Block(g802)
    c: Block(g803)
    c: Block(g804)
    c: Block(g805)
    c: Block(g806)
    c: Block(g807)
    c: Block(g808)
    c: Block(g809)
    c: Block(g810)
    c: Block(g811)
    c: Block(g812)
    c: Block(g813)
    c: Block(g814)
    c: Block(g815)
    c: Block(g816)
    c: Block(g817)
    c: Block(g818)
    c: Block(g819)
    c: Block(g820)
    c: Block(g821)
    c: Block(g822)
    c: Block(g823)
    c: Block(g824)
    c: Block(g825)
    c: Block(g826)
    c: Block(g827)
    c: Block(g828)
    c: Block(g829)
    c: Block(g830)
    c: Block(g831)
    c: Block(g832)
    c: Block(g833)
    c: Block(g834)
    c: Block(g835)
    c: Block(g836)
    c: Block(g837)
    c: Block(g838)
    c: Block(g839)
    c: Block(g840)
    c: Block(g841)
    c: Block(g842)
    c: Block(g843)
    c: Block(g844)
    c: Block(g845)
    c: Block(g846)
    c: Block(g847)
    c: Block(g848)
    c: Block(g849)
    c: Block(g850)
    c: Block(g851)
    c: Block(g852)
    c: Block(g853)
    c: Block(g854)
    c: Block(g855)
    c: Block(g856)
    c: Block(g857)
    c: Block(g858)
    c: Block(g859)
    c: Block(g860)
    c: Block(g861)
    c: Block(g862)
    c: Block(g863)
    c: Block(g864)
    c: Block(g865)
    c: Block(g866)
    c: Block(g867)
    c: Block(g868)
    c: Block(g869)
    c: Block(g870)
    c: Block(g871)
    c: Block(g872)
    c: Block(g873)
    c: Block(g874)
    c: Block(g875)
    c: Block(g876)
    c: Block(g877)
    c: Block(g878)
    c: Block(g879)
    c: Block(g880)
    c: Block(g881)
    c: Block(g882)
    c: Block(g883)
    c: Block(g884)
    c: Block(g885)
    c: Block(g886)
    c: Block(g887)
    c: Block(g888)
    c: Block(g889)
    c: Block(g890)
    c: Block(g891)
    c: Block(g892)
    c: Block(g893)
    c: Block(g894)
    c: Block(g895)
    c: Block(g896)
    c: Block(g897)
    c: Block(g898)
    c: Block(g899)
    c: Block(g900)
    c: Block(g901)
    c: Block(g902)
    c: Block(g903)
    c: Block(g904)
    c: Block(g905)
    c: Block(g906)
    c: Block(g907)
    c: Block(g908)
    c: Block(g909)
    c: Block(g910)
    c: Block(g911)
    c: Coincident(g689,g693)
    c: Coincident(g195,g196)
    c: Coincident(g688,g693)
    c: Coincident(g194,g196)
    c: Coincident(g658,g662)
    c: Coincident(g674,g679)
    c: Coincident(g657,g662)
    c: Coincident(g675,g679)
    c: Coincident(g824,g829)
    c: Coincident(g827,g829)
    c: Coincident(g145,g148)
    c: Coincident(g146,g148)
    c: Coincident(g688,g694)
    c: Coincident(g690,g692)
    c: Coincident(g194,g199)
    c: Coincident(g193,g197)
    c: Coincident(g691,g694)
    c: Coincident(g691,g692)
    c: Coincident(g192,g199)
    c: Coincident(g192,g197)
    c: Coincident(g657,g660)
    c: Coincident(g656,g663)
    c: Coincident(g675,g677)
    c: Coincident(g673,g678)
    c: Coincident(g659,g660)
    c: Coincident(g659,g663)
    c: Coincident(g672,g677)
    c: Coincident(g672,g678)
    c: Coincident(g827,g828)
    c: Coincident(g825,g831)
    c: Coincident(g826,g828)
    c: Coincident(g826,g831)
    c: Coincident(g624,g630)
    c: Coincident(g626,g630)
    c: Coincident(g146,g151)
    c: Coincident(g144,g150)
    c: Coincident(g147,g151)
    c: Coincident(g147,g150)
    c: Coincident(g840,g847)
    c: Coincident(g842,g847)
    c: Coincident(g874,g878)
    c: Coincident(g873,g878)
    c: Coincident(g322,g326)
    c: Coincident(g321,g326)
    c: Coincident(g626,g629)
    c: Coincident(g627,g628)
    c: Coincident(g625,g629)
    c: Coincident(g625,g628)
    c: Coincident(g122,g124)
    c: Coincident(g121,g124)
    c: Coincident(g842,g844)
    c: Coincident(g843,g845)
    c: Coincident(g841,g844)
    c: Coincident(g841,g845)
    c: Coincident(g417,g420)
    c: Coincident(g577,g583)
    c: Coincident(g418,g420)
    c: Coincident(g578,g583)
    c: Coincident(g873,g876)
    c: Coincident(g875,g877)
    c: Coincident(g872,g876)
    c: Coincident(g872,g877)
    c: Coincident(g321,g324)
    c: Coincident(g323,g325)
    c: Coincident(g320,g324)
    c: Coincident(g320,g325)
    c: Coincident(g499,g502)
    c: Coincident(g497,g502)
    c: Coincident(g121,g126)
    c: Coincident(g123,g125)
    c: Coincident(g120,g126)
    c: Coincident(g120,g125)
    c: Coincident(g115,g119)
    c: Coincident(g112,g119)
    c: Coincident(g450,g452)
    c: Coincident(g448,g452)
    c: Coincident(g418,g423)
    c: Coincident(g416,g422)
    c: Coincident(g578,g582)
    c: Coincident(g579,g580)
    c: Coincident(g419,g423)
    c: Coincident(g419,g422)
    c: Coincident(g576,g582)
    c: Coincident(g576,g580)
    c: Coincident(g435,g438)
    c: Coincident(g434,g438)
    c: Coincident(g497,g500)
    c: Coincident(g496,g503)
    c: Coincident(g498,g500)
    c: Coincident(g498,g503)
    c: Coincident(g305,g308)
    c: Coincident(g361,g367)
    c: Coincident(g304,g308)
    c: Coincident(g360,g367)
    c: Coincident(g112,g118)
    c: Coincident(g114,g117)
    c: Coincident(g113,g118)
    c: Coincident(g113,g117)
    c: Coincident(g338,g340)
    c: Coincident(g339,g340)
    c: Coincident(g448,g454)
    c: Coincident(g449,g453)
    c: Coincident(g451,g454)
    c: Coincident(g451,g453)
    c: Coincident(g434,g436)
    c: Coincident(g432,g439)
    c: Coincident(g433,g436)
    c: Coincident(g433,g439)
    c: Coincident(g898,g902)
    c: Coincident(g899,g902)
    c: Coincident(g304,g311)
    c: Coincident(g306,g310)
    c: Coincident(g360,g366)
    c: Coincident(g363,g365)
    c: Coincident(g307,g311)
    c: Coincident(g307,g310)
    c: Coincident(g362,g366)
    c: Coincident(g362,g365)
    c: Coincident(g633,g638)
    c: Coincident(g635,g638)
    c: Coincident(g68,g77)
    c: Coincident(g68,g79)
    c: Coincident(g339,g343)
    c: Coincident(g337,g342)
    c: Coincident(g64,g77)
    c: Coincident(g70,g79)
    c: Coincident(g336,g343)
    c: Coincident(g336,g342)
    c: Coincident(g130,g135)
    c: Coincident(g680,g686)
    c: Coincident(g129,g135)
    c: Coincident(g682,g686)
    c: Coincident(g899,g903)
    c: Coincident(g896,g901)
    c: Coincident(g897,g903)
    c: Coincident(g897,g901)
    c: Coincident(g531,g533)
    c: Coincident(g64,g76)
    c: Coincident(g70,g73)
    c: Coincident(g530,g533)
    c: Coincident(g69,g76)
    c: Coincident(g69,g73)
    c: Coincident(g402,g405)
    c: Coincident(g401,g405)
    c: Coincident(g635,g639)
    c: Coincident(g632,g636)
    c: Coincident(g634,g639)
    c: Coincident(g634,g636)
    c: Coincident(g571,g574)
    c: Coincident(g568,g574)
    c: Coincident(g129,g133)
    c: Coincident(g131,g134)
    c: Coincident(g682,g685)
    c: Coincident(g683,g687)
    c: Coincident(g128,g133)
    c: Coincident(g128,g134)
    c: Coincident(g681,g685)
    c: Coincident(g681,g687)
    c: Coincident(g755,g758)
    c: Coincident(g753,g758)
    c: Coincident(g530,g534)
    c: Coincident(g528,g535)
    c: Coincident(g529,g534)
    c: Coincident(g529,g535)
    c: Coincident(g546,g548)
    c: Coincident(g849,g853)
    c: Coincident(g547,g548)
    c: Coincident(g850,g853)
    c: Coincident(g401,g407)
    c: Coincident(g400,g404)
    c: Coincident(g403,g407)
    c: Coincident(g403,g404)
    c: Coincident(g65,g74)
    c: Coincident(g65,g78)
    c: Coincident(g568,g573)
    c: Coincident(g569,g575)
    c: Coincident(g67,g74)
    c: Coincident(g66,g78)
    c: Coincident(g570,g573)
    c: Coincident(g570,g575)
    c: Coincident(g537,g543)
    c: Coincident(g538,g543)
    c: Coincident(g753,g757)
    c: Coincident(g752,g756)
    c: Coincident(g754,g757)
    c: Coincident(g754,g756)
    c: Coincident(g411,g415)
    c: Coincident(g66,g75)
    c: Coincident(g67,g72)
    c: Coincident(g408,g415)
    c: Coincident(g71,g75)
    c: Coincident(g71,g72)
    c: Coincident(g547,g549)
    c: Coincident(g545,g550)
    c: Coincident(g850,g852)
    c: Coincident(g851,g854)
    c: Coincident(g544,g549)
    c: Coincident(g544,g550)
    c: Coincident(g848,g852)
    c: Coincident(g848,g854)
    c: Coincident(g234,g239)
    c: Coincident(g233,g239)
    c: Coincident(g538,g541)
    c: Coincident(g539,g540)
    c: Coincident(g536,g541)
    c: Coincident(g536,g540)
    c: Coincident(g736,g740)
    c: Coincident(g737,g740)
    c: Coincident(g408,g413)
    c: Coincident(g410,g412)
    c: Coincident(g409,g413)
    c: Coincident(g409,g412)
    c: Coincident(g808,g815)
    c: Coincident(g809,g815)
    c: Coincident(g730,g732)
    c: Coincident(g729,g732)
    c: Coincident(g233,g237)
    c: Coincident(g235,g236)
    c: Coincident(g232,g237)
    c: Coincident(g232,g236)
    c: Coincident(g425,g429)
    c: Coincident(g378,g380)
    c: Coincident(g427,g429)
    c: Coincident(g377,g380)
    c: Coincident(g737,g742)
    c: Coincident(g738,g741)
    c: Coincident(g739,g742)
    c: Coincident(g739,g741)
    c: Coincident(g619,g621)
    c: Coincident(g617,g621)
    c: Coincident(g809,g813)
    c: Coincident(g810,g814)
    c: Coincident(g811,g813)
    c: Coincident(g811,g814)
    c: Coincident(g801,g807)
    c: Coincident(g802,g807)
    c: Coincident(g729,g735)
    c: Coincident(g731,g734)
    c: Coincident(g728,g735)
    c: Coincident(g728,g734)
    c: Coincident(g427,g431)
    c: Coincident(g424,g428)
    c: Coincident(g377,g383)
    c: Coincident(g379,g382)
    c: Coincident(g426,g431)
    c: Coincident(g426,g428)
    c: Coincident(g376,g383)
    c: Coincident(g376,g382)
    c: Coincident(g611,g615)
    c: Coincident(g609,g615)
    c: Coincident(g617,g620)
    c: Coincident(g616,g623)
    c: Coincident(g618,g620)
    c: Coincident(g618,g623)
    c: Coincident(g139,g141)
    c: Coincident(g904,g910)
    c: Coincident(g137,g141)
    c: Coincident(g907,g910)
    c: Coincident(g802,g806)
    c: Coincident(g800,g804)
    c: Coincident(g803,g806)
    c: Coincident(g803,g804)
    c: Coincident(g210,g213)
    c: Coincident(g209,g213)
    c: Coincident(g22,g24)
    c: Coincident(g22,g29)
    c: Coincident(g609,g613)
    c: Coincident(g610,g612)
    c: Coincident(g21,g24)
    c: Coincident(g16,g29)
    c: Coincident(g608,g613)
    c: Coincident(g608,g612)
    c: Coincident(g344,g349)
    c: Coincident(g347,g349)
    c: Coincident(g137,g142)
    c: Coincident(g138,g140)
    c: Coincident(g907,g911)
    c: Coincident(g905,g908)
    c: Coincident(g136,g142)
    c: Coincident(g136,g140)
    c: Coincident(g906,g911)
    c: Coincident(g906,g908)
    c: Coincident(g216,g222)
    c: Coincident(g21,g30)
    c: Coincident(g16,g25)
    c: Coincident(g217,g222)
    c: Coincident(g20,g30)
    c: Coincident(g20,g25)
    c: Coincident(g650,g652)
    c: Coincident(g649,g652)
    c: Coincident(g209,g214)
    c: Coincident(g211,g215)
    c: Coincident(g208,g214)
    c: Coincident(g208,g215)
    c: Coincident(g170,g175)
    c: Coincident(g522,g525)
    c: Coincident(g168,g175)
    c: Coincident(g521,g525)
    c: Coincident(g347,g351)
    c: Coincident(g345,g348)
    c: Coincident(g346,g351)
    c: Coincident(g346,g348)
    c: Coincident(g394,g396)
    c: Coincident(g395,g396)
    c: Coincident(g217,g221)
    c: Coincident(g219,g220)
    c: Coincident(g218,g221)
    c: Coincident(g218,g220)
    c: Coincident(g442,g447)
    c: Coincident(g440,g447)
    c: Coincident(g649,g654)
    c: Coincident(g651,g653)
    c: Coincident(g648,g654)
    c: Coincident(g648,g653)
    c: Coincident(g17,g28)
    c: Coincident(g168,g172)
    c: Coincident(g169,g173)
    c: Coincident(g521,g526)
    c: Coincident(g523,g527)
    c: Coincident(g18,g28)
    c: Coincident(g171,g172)
    c: Coincident(g171,g173)
    c: Coincident(g520,g526)
    c: Coincident(g520,g527)
    c: Coincident(g715,g718)
    c: Coincident(g713,g718)
    c: Coincident(g395,g397)
    c: Coincident(g392,g398)
    c: Coincident(g393,g397)
    c: Coincident(g393,g398)
    c: Coincident(g457,g463)
    c: Coincident(g256,g260)
    c: Coincident(g18,g26)
    c: Coincident(g19,g31)
    c: Coincident(g459,g463)
    c: Coincident(g257,g260)
    c: Coincident(g23,g26)
    c: Coincident(g23,g31)
    c: Coincident(g440,g445)
    c: Coincident(g441,g446)
    c: Coincident(g443,g445)
    c: Coincident(g443,g446)
    c: Coincident(g777,g780)
    c: Coincident(g779,g780)
    c: Coincident(g713,g719)
    c: Coincident(g712,g716)
    c: Coincident(g714,g719)
    c: Coincident(g714,g716)
    c: Coincident(g248,g255)
    c: Coincident(g250,g255)
    c: Coincident(g224,g231)
    c: Coincident(g227,g231)
    c: Coincident(g459,g461)
    c: Coincident(g458,g460)
    c: Coincident(g257,g263)
    c: Coincident(g258,g261)
    c: Coincident(g456,g461)
    c: Coincident(g456,g460)
    c: Coincident(g259,g263)
    c: Coincident(g259,g261)
    c: Coincident(g384,g389)
    c: Coincident(g387,g389)
    c: Coincident(g779,g781)
    c: Coincident(g776,g782)
    c: Coincident(g778,g781)
    c: Coincident(g778,g782)
    c: Coincident(g203,g205)
    c: Coincident(g200,g205)
    c: Coincident(g250,g254)
    c: Coincident(g251,g253)
    c: Coincident(g249,g254)
    c: Coincident(g249,g253)
    c: Coincident(g792,g799)
    c: Coincident(g795,g799)
    c: Coincident(g227,g228)
    c: Coincident(g225,g229)
    c: Coincident(g226,g228)
    c: Coincident(g226,g229)
    c: Coincident(g387,g391)
    c: Coincident(g386,g390)
    c: Coincident(g385,g391)
    c: Coincident(g385,g390)
    c: Coincident(g512,g517)
    c: Coincident(g464,g469)
    c: Coincident(g514,g517)
    c: Coincident(g465,g469)
    c: Coincident(g200,g207)
    c: Coincident(g201,g206)
    c: Coincident(g202,g207)
    c: Coincident(g202,g206)
    c: Coincident(g299,g301)
    c: Coincident(g298,g301)
    c: Coincident(g795,g798)
    c: Coincident(g794,g797)
    c: Coincident(g793,g798)
    c: Coincident(g793,g797)
    c: Coincident(g858,g862)
    c: Coincident(g856,g862)
    c: Coincident(g819,g821)
    c: Coincident(g816,g821)
    c: Coincident(g514,g519)
    c: Coincident(g515,g516)
    c: Coincident(g465,g470)
    c: Coincident(g466,g468)
    c: Coincident(g513,g519)
    c: Coincident(g513,g516)
    c: Coincident(g467,g470)
    c: Coincident(g467,g468)
    c: Coincident(g184,g191)
    c: Coincident(g185,g191)
    c: Coincident(g298,g302)
    c: Coincident(g296,g300)
    c: Coincident(g297,g302)
    c: Coincident(g297,g300)
    c: Coincident(g704,g710)
    c: Coincident(g697,g703)
    c: Coincident(g706,g710)
    c: Coincident(g699,g703)
    c: Coincident(g856,g863)
    c: Coincident(g859,g861)
    c: Coincident(g857,g863)
    c: Coincident(g857,g861)
    c: Coincident(g816,g823)
    c: Coincident(g818,g820)
    c: Coincident(g817,g823)
    c: Coincident(g817,g820)
    c: Coincident(g185,g190)
    c: Coincident(g186,g189)
    c: Coincident(g187,g190)
    c: Coincident(g187,g189)
    c: Coincident(g835,g839)
    c: Coincident(g834,g839)
    c: Coincident(g491,g495)
    c: Coincident(g281,g286)
    c: Coincident(g488,g495)
    c: Coincident(g283,g286)
    c: Coincident(g706,g711)
    c: Coincident(g705,g708)
    c: Coincident(g699,g700)
    c: Coincident(g698,g701)
    c: Coincident(g707,g711)
    c: Coincident(g707,g708)
    c: Coincident(g696,g700)
    c: Coincident(g696,g701)
    c: Coincident(g99,g104)
    c: Coincident(g99,g106)
    c: Coincident(g100,g104)
    c: Coincident(g98,g106)
    c: Coincident(g163,g167)
    c: Coincident(g162,g167)
    c: Coincident(g32,g47)
    c: Coincident(g32,g45)
    c: Coincident(g39,g47)
    c: Coincident(g38,g45)
    c: Coincident(g834,g837)
    c: Coincident(g833,g836)
    c: Coincident(g832,g837)
    c: Coincident(g832,g836)
    c: Coincident(g100,g107)
    c: Coincident(g98,g108)
    c: Coincident(g102,g107)
    c: Coincident(g102,g108)
    c: Coincident(g488,g492)
    c: Coincident(g490,g493)
    c: Coincident(g283,g284)
    c: Coincident(g282,g287)
    c: Coincident(g489,g492)
    c: Coincident(g489,g493)
    c: Coincident(g280,g284)
    c: Coincident(g280,g287)
    c: Coincident(g666,g669)
    c: Coincident(g39,g42)
    c: Coincident(g38,g40)
    c: Coincident(g664,g669)
    c: Coincident(g36,g42)
    c: Coincident(g36,g40)
    c: Coincident(g889,g893)
    c: Coincident(g891,g893)
    c: Coincident(g329,g333)
    c: Coincident(g328,g333)
    c: Coincident(g162,g165)
    c: Coincident(g161,g166)
    c: Coincident(g160,g165)
    c: Coincident(g160,g166)
    c: Coincident(g265,g270)
    c: Coincident(g264,g270)
    c: Coincident(g586,g591)
    c: Coincident(g762,g765)
    c: Coincident(g587,g591)
    c: Coincident(g763,g765)
    c: Coincident(g664,g668)
    c: Coincident(g665,g671)
    c: Coincident(g667,g668)
    c: Coincident(g667,g671)
    c: Coincident(g97,g111)
    c: Coincident(g891,g894)
    c: Coincident(g888,g892)
    c: Coincident(g96,g111)
    c: Coincident(g890,g894)
    c: Coincident(g890,g892)
    c: Coincident(g34,g43)
    c: Coincident(g328,g335)
    c: Coincident(g331,g332)
    c: Coincident(g35,g41)
    c: Coincident(g33,g43)
    c: Coincident(g330,g335)
    c: Coincident(g330,g332)
    c: Coincident(g264,g271)
    c: Coincident(g266,g268)
    c: Coincident(g267,g271)
    c: Coincident(g267,g268)
    c: Coincident(g96,g105)
    c: Coincident(g103,g109)
    c: Coincident(g101,g105)
    c: Coincident(g101,g109)
    c: Coincident(g33,g46)
    c: Coincident(g35,g44)
    c: Coincident(g37,g46)
    c: Coincident(g37,g44)
    c: Coincident(g587,g588)
    c: Coincident(g585,g589)
    c: Coincident(g763,g766)
    c: Coincident(g761,g767)
    c: Coincident(g584,g588)
    c: Coincident(g584,g589)
    c: Coincident(g760,g766)
    c: Coincident(g760,g767)
    c: Coincident(g480,g487)
    c: Coincident(g312,g316)
    c: Coincident(g274,g278)
    c: Coincident(g867,g868)
    c: Coincident(g475,g477)
    c: Coincident(g482,g487)
    c: Coincident(g314,g316)
    c: Coincident(g275,g278)
    c: Coincident(g866,g868)
    c: Coincident(g474,g477)
    c: Coincident(g482,g486)
    c: Coincident(g483,g485)
    c: Coincident(g314,g319)
    c: Coincident(g313,g317)
    c: Coincident(g275,g276)
    c: Coincident(g272,g277)
    c: Coincident(g866,g871)
    c: Coincident(g864,g869)
    c: Coincident(g474,g478)
    c: Coincident(g472,g479)
    c: Coincident(g481,g486)
    c: Coincident(g481,g485)
    c: Coincident(g315,g319)
    c: Coincident(g315,g317)
    c: Coincident(g273,g276)
    c: Coincident(g273,g277)
    c: Coincident(g865,g871)
    c: Coincident(g865,g869)
    c: Coincident(g473,g478)
    c: Coincident(g473,g479)
    c: Coincident(g353,g357)
    c: Coincident(g371,g373)
    c: Coincident(g880,g886)
    c: Coincident(g506,g509)
    c: Coincident(g355,g357)
    c: Coincident(g370,g373)
    c: Coincident(g883,g886)
    c: Coincident(g505,g509)
    c: Coincident(g53,g57)
    c: Coincident(g53,g62)
    c: Coincident(g55,g57)
    c: Coincident(g52,g62)
    c: Coincident(g55,g60)
    c: Coincident(g52,g61)
    c: Coincident(g54,g60)
    c: Coincident(g54,g61)
    c: Coincident(g553,g559)
    c: Coincident(g552,g559)
    c: Coincident(g355,g358)
    c: Coincident(g354,g359)
    c: Coincident(g370,g374)
    c: Coincident(g369,g372)
    c: Coincident(g883,g885)
    c: Coincident(g882,g884)
    c: Coincident(g505,g511)
    c: Coincident(g507,g508)
    c: Coincident(g352,g358)
    c: Coincident(g352,g359)
    c: Coincident(g368,g374)
    c: Coincident(g368,g372)
    c: Coincident(g881,g885)
    c: Coincident(g881,g884)
    c: Coincident(g504,g511)
    c: Coincident(g504,g508)
    c: Coincident(g595,g599)
    c: Coincident(g722,g727)
    c: Coincident(g561,g565)
    c: Coincident(g640,g647)
    c: Coincident(g592,g599)
    c: Coincident(g723,g727)
    c: Coincident(g563,g565)
    c: Coincident(g641,g647)
    c: Coincident(g552,g558)
    c: Coincident(g554,g557)
    c: Coincident(g555,g558)
    c: Coincident(g555,g557)
    c: Coincident(g49,g59)
    c: Coincident(g49,g58)
    c: Coincident(g48,g59)
    c: Coincident(g50,g58)
    c: Coincident(g50,g63)
    c: Coincident(g48,g56)
    c: Coincident(g51,g63)
    c: Coincident(g51,g56)
    c: Coincident(g592,g596)
    c: Coincident(g594,g597)
    c: Coincident(g723,g725)
    c: Coincident(g720,g726)
    c: Coincident(g563,g566)
    c: Coincident(g560,g567)
    c: Coincident(g641,g645)
    c: Coincident(g642,g644)
    c: Coincident(g593,g596)
    c: Coincident(g593,g597)
    c: Coincident(g721,g725)
    c: Coincident(g721,g726)
    c: Coincident(g562,g566)
    c: Coincident(g562,g567)
    c: Coincident(g643,g645)
    c: Coincident(g643,g644)
    c: Coincident(g291,g292)
    c: Coincident(g601,g604)
    c: Coincident(g770,g774)
    c: Coincident(g152,g156)
    c: Coincident(g177,g183)
    c: Coincident(g289,g292)
    c: Coincident(g600,g604)
    c: Coincident(g771,g774)
    c: Coincident(g154,g156)
    c: Coincident(g176,g183)
    c: Coincident(g289,g293)
    c: Coincident(g290,g294)
    c: Coincident(g600,g605)
    c: Coincident(g603,g606)
    c: Coincident(g771,g772)
    c: Coincident(g769,g773)
    c: Coincident(g154,g158)
    c: Coincident(g155,g157)
    c: Coincident(g176,g181)
    c: Coincident(g178,g180)
    c: Coincident(g288,g293)
    c: Coincident(g288,g294)
    c: Coincident(g602,g605)
    c: Coincident(g602,g606)
    c: Coincident(g768,g772)
    c: Coincident(g768,g773)
    c: Coincident(g153,g158)
    c: Coincident(g153,g157)
    c: Coincident(g179,g181)
    c: Coincident(g179,g180)
    c: Coincident(g744,g749)
    c: Coincident(g243,g247)
    c: Coincident(g785,g791)
    c: Coincident(g747,g749)
    c: Coincident(g240,g247)
    c: Coincident(g786,g791)
    c: Coincident(g83,g94)
    c: Coincident(g83,g90)
    c: Coincident(g80,g89)
    c: Coincident(g80,g95)
    c: Coincident(g4,g15)
    c: Coincident(g4,g11)
    c: Coincident(g0,g14)
    c: Coincident(g0,g10)
    c: Coincident(g86,g94)
    c: Coincident(g81,g90)
    c: Coincident(g87,g89)
    c: Coincident(g82,g95)
    c: Coincident(g7,g15)
    c: Coincident(g3,g11)
    c: Coincident(g5,g14)
    c: Coincident(g1,g10)
    c: Coincident(g747,g751)
    c: Coincident(g746,g750)
    c: Coincident(g240,g246)
    c: Coincident(g241,g245)
    c: Coincident(g786,g789)
    c: Coincident(g787,g788)
    c: Coincident(g745,g751)
    c: Coincident(g745,g750)
    c: Coincident(g242,g246)
    c: Coincident(g242,g245)
    c: Coincident(g784,g789)
    c: Coincident(g784,g788)
    c: Coincident(g86,g93)
    c: Coincident(g81,g92)
    c: Coincident(g87,g88)
    c: Coincident(g82,g91)
    c: Coincident(g7,g12)
    c: Coincident(g3,g9)
    c: Coincident(g5,g13)
    c: Coincident(g1,g8)
    c: Coincident(g85,g93)
    c: Coincident(g85,g92)
    c: Coincident(g84,g88)
    c: Coincident(g84,g91)
    c: Coincident(g6,g12)
    c: Coincident(g6,g9)
    c: Coincident(g2,g13)
    c: Coincident(g2,g8)
    c: Coincident(g689,g695)
    c: Coincident(g195,g198)
    c: Coincident(g690,g695)
    c: Coincident(g193,g198)
    c: Coincident(g674,g676)
    c: Coincident(g658,g661)
    c: Coincident(g673,g676)
    c: Coincident(g656,g661)
    c: Coincident(g824,g830)
    c: Coincident(g825,g830)
    c: Coincident(g145,g149)
    c: Coincident(g144,g149)
    c: Coincident(g624,g631)
    c: Coincident(g627,g631)
    c: Coincident(g840,g846)
    c: Coincident(g843,g846)
    c: Coincident(g874,g879)
    c: Coincident(g875,g879)
    c: Coincident(g322,g327)
    c: Coincident(g323,g327)
    c: Coincident(g122,g127)
    c: Coincident(g123,g127)
    c: Coincident(g417,g421)
    c: Coincident(g577,g581)
    c: Coincident(g416,g421)
    c: Coincident(g579,g581)
    c: Coincident(g499,g501)
    c: Coincident(g496,g501)
    c: Coincident(g115,g116)
    c: Coincident(g114,g116)
    c: Coincident(g450,g455)
    c: Coincident(g449,g455)
    c: Coincident(g435,g437)
    c: Coincident(g432,g437)
    c: Coincident(g305,g309)
    c: Coincident(g361,g364)
    c: Coincident(g306,g309)
    c: Coincident(g363,g364)
    c: Coincident(g338,g341)
    c: Coincident(g337,g341)
    c: Coincident(g898,g900)
    c: Coincident(g896,g900)
    c: Coincident(g633,g637)
    c: Coincident(g632,g637)
    c: Coincident(g130,g132)
    c: Coincident(g680,g684)
    c: Coincident(g131,g132)
    c: Coincident(g683,g684)
    c: Coincident(g531,g532)
    c: Coincident(g528,g532)
    c: Coincident(g402,g406)
    c: Coincident(g400,g406)
    c: Coincident(g571,g572)
    c: Coincident(g569,g572)
    c: Coincident(g755,g759)
    c: Coincident(g752,g759)
    c: Coincident(g546,g551)
    c: Coincident(g849,g855)
    c: Coincident(g545,g551)
    c: Coincident(g851,g855)
    c: Coincident(g537,g542)
    c: Coincident(g539,g542)
    c: Coincident(g411,g414)
    c: Coincident(g410,g414)
    c: Coincident(g234,g238)
    c: Coincident(g235,g238)
    c: Coincident(g736,g743)
    c: Coincident(g738,g743)
    c: Coincident(g808,g812)
    c: Coincident(g810,g812)
    c: Coincident(g730,g733)
    c: Coincident(g731,g733)
    c: Coincident(g425,g430)
    c: Coincident(g378,g381)
    c: Coincident(g424,g430)
    c: Coincident(g379,g381)
    c: Coincident(g619,g622)
    c: Coincident(g616,g622)
    c: Coincident(g801,g805)
    c: Coincident(g800,g805)
    c: Coincident(g611,g614)
    c: Coincident(g610,g614)
    c: Coincident(g139,g143)
    c: Coincident(g904,g909)
    c: Coincident(g138,g143)
    c: Coincident(g905,g909)
    c: Coincident(g210,g212)
    c: Coincident(g211,g212)
    c: Coincident(g344,g350)
    c: Coincident(g345,g350)
    c: Coincident(g216,g223)
    c: Coincident(g219,g223)
    c: Coincident(g650,g655)
    c: Coincident(g651,g655)
    c: Coincident(g170,g174)
    c: Coincident(g522,g524)
    c: Coincident(g169,g174)
    c: Coincident(g523,g524)
    c: Coincident(g394,g399)
    c: Coincident(g392,g399)
    c: Coincident(g442,g444)
    c: Coincident(g441,g444)
    c: Coincident(g17,g27)
    c: Coincident(g19,g27)
    c: Coincident(g715,g717)
    c: Coincident(g712,g717)
    c: Coincident(g457,g462)
    c: Coincident(g256,g262)
    c: Coincident(g458,g462)
    c: Coincident(g258,g262)
    c: Coincident(g777,g783)
    c: Coincident(g776,g783)
    c: Coincident(g248,g252)
    c: Coincident(g251,g252)
    c: Coincident(g224,g230)
    c: Coincident(g225,g230)
    c: Coincident(g384,g388)
    c: Coincident(g386,g388)
    c: Coincident(g203,g204)
    c: Coincident(g201,g204)
    c: Coincident(g792,g796)
    c: Coincident(g794,g796)
    c: Coincident(g512,g518)
    c: Coincident(g464,g471)
    c: Coincident(g515,g518)
    c: Coincident(g466,g471)
    c: Coincident(g299,g303)
    c: Coincident(g296,g303)
    c: Coincident(g858,g860)
    c: Coincident(g859,g860)
    c: Coincident(g819,g822)
    c: Coincident(g818,g822)
    c: Coincident(g184,g188)
    c: Coincident(g186,g188)
    c: Coincident(g704,g709)
    c: Coincident(g697,g702)
    c: Coincident(g705,g709)
    c: Coincident(g698,g702)
    c: Coincident(g835,g838)
    c: Coincident(g833,g838)
    c: Coincident(g491,g494)
    c: Coincident(g281,g285)
    c: Coincident(g490,g494)
    c: Coincident(g282,g285)
    c: Coincident(g163,g164)
    c: Coincident(g161,g164)
    c: Coincident(g666,g670)
    c: Coincident(g665,g670)
    c: Coincident(g889,g895)
    c: Coincident(g888,g895)
    c: Coincident(g329,g334)
    c: Coincident(g331,g334)
    c: Coincident(g265,g269)
    c: Coincident(g266,g269)
    c: Coincident(g586,g590)
    c: Coincident(g762,g764)
    c: Coincident(g585,g590)
    c: Coincident(g761,g764)
    c: Coincident(g97,g110)
    c: Coincident(g103,g110)
    c: Coincident(g34,g41)
    c: Coincident(g480,g484)
    c: Coincident(g312,g318)
    c: Coincident(g274,g279)
    c: Coincident(g867,g870)
    c: Coincident(g475,g476)
    c: Coincident(g483,g484)
    c: Coincident(g313,g318)
    c: Coincident(g272,g279)
    c: Coincident(g864,g870)
    c: Coincident(g472,g476)
    c: Coincident(g353,g356)
    c: Coincident(g371,g375)
    c: Coincident(g880,g887)
    c: Coincident(g506,g510)
    c: Coincident(g354,g356)
    c: Coincident(g369,g375)
    c: Coincident(g882,g887)
    c: Coincident(g507,g510)
    c: Coincident(g553,g556)
    c: Coincident(g554,g556)
    c: Coincident(g595,g598)
    c: Coincident(g722,g724)
    c: Coincident(g561,g564)
    c: Coincident(g640,g646)
    c: Coincident(g594,g598)
    c: Coincident(g720,g724)
    c: Coincident(g560,g564)
    c: Coincident(g642,g646)
    c: Coincident(g291,g295)
    c: Coincident(g601,g607)
    c: Coincident(g770,g775)
    c: Coincident(g152,g159)
    c: Coincident(g177,g182)
    c: Coincident(g290,g295)
    c: Coincident(g603,g607)
    c: Coincident(g769,g775)
    c: Coincident(g155,g159)
    c: Coincident(g178,g182)
    c: Coincident(g744,g748)
    c: Coincident(g243,g244)
    c: Coincident(g785,g790)
    c: Coincident(g746,g748)
    c: Coincident(g241,g244)
    c: Coincident(g787,g790)
    c: Tangent(g912,g913) = 1.5708
    c: Tangent(g913,g914) = 1.5708
    c: Tangent(g914,g915) = 1.5708
    c: Tangent(g915,g916) = 1.5708
    c: Tangent(g916,g917) = 1.5708
    c: Tangent(g917,g918) = 1.5708
    c: Tangent(g918,g919) = 1.5708
    c: Tangent(g919,g912) = 1.5708
    c: Horizontal(g913)
    c: Horizontal(g917)
    c: Vertical(g915)
    c: Vertical(g919)
    c: Equal(g912,g914)
    c: Equal(g914,g916)
    c: Equal(g916,g918)
    c: PointOnObject(g920,g913)
    c: PointOnObject(g920,g919)
    c: PointOnObject(g921,g915)
    c: PointOnObject(g921,g917)
    c: Vertical(g918,g475)
    c: DistanceY(g472,g917) = 5
    c: DistanceY(g761,g912) = 5
    c: Vertical(g915,g784)
    c: Block(g760)
    c: DistanceY(g915,g915) = 10.94
    c: Radius(g914) = 6.44
    c: DistanceX(g913,g913) = 82.08
FEATURE [Sketcher::SketchObject] Sketch001  label="Plate outline"
  ExternalGeometry = -> [Sketch]
  FullyConstrained = true
  MapMode = 5
  Support = -> [XY_Plane]
  sketch-geometry (16):
    g0: ArcOfCircle CenterX=22.7562 CenterY=-16.7502 CenterZ=0 NormalX=0 NormalY=0 NormalZ=1 AngleXU=0 Radius=5 StartAngle=1.5708 EndAngle=3.14159
    g1: LineSegment StartX=22.7562 StartY=-11.7502 StartZ=0 EndX=420.426 EndY=-11.7502 EndZ=0
    g2: ArcOfCircle CenterX=420.426 CenterY=-16.7502 CenterZ=0 NormalX=0 NormalY=0 NormalZ=1 AngleXU=0 Radius=5 StartAngle=0 EndAngle=1.5708
    g3: LineSegment StartX=425.426 StartY=-16.7502 StartZ=0 EndX=425.426 EndY=-147.648 EndZ=0
    g4: ArcOfCircle CenterX=420.426 CenterY=-147.648 CenterZ=0 NormalX=0 NormalY=0 NormalZ=1 AngleXU=0 Radius=5 StartAngle=4.71239 EndAngle=6.28319
    g5: LineSegment StartX=420.426 StartY=-152.648 StartZ=0 EndX=22.7562 EndY=-152.648 EndZ=0
    g6: ArcOfCircle CenterX=22.7562 CenterY=-147.648 CenterZ=0 NormalX=0 NormalY=0 NormalZ=1 AngleXU=0 Radius=5 StartAngle=3.14159 EndAngle=4.71239
    g7: LineSegment StartX=17.7562 StartY=-147.648 StartZ=0 EndX=17.7562 EndY=-16.7502 EndZ=0
    g8: GeomPoint X=17.7562 Y=-11.7502 Z=0
    g9: GeomPoint X=425.426 Y=-152.648 Z=0
    g10: Circle CenterX=22.8662 CenterY=-17.8102 CenterZ=0 NormalX=0 NormalY=0 NormalZ=1 AngleXU=0 Radius=1.5
    g11: Circle CenterX=229.876 CenterY=-19.0802 CenterZ=0 NormalX=0 NormalY=0 NormalZ=1 AngleXU=0 Radius=1.5
    g12: Circle CenterX=420.296 CenterY=-17.8102 CenterZ=0 NormalX=0 NormalY=0 NormalZ=1 AngleXU=0 Radius=1.5
    g13: Circle CenterX=420.346 CenterY=-147.568 CenterZ=0 NormalX=0 NormalY=0 NormalZ=1 AngleXU=0 Radius=1.5
    g14: Circle CenterX=226.116 CenterY=-148.7 CenterZ=0 NormalX=0 NormalY=0 NormalZ=1 AngleXU=0 Radius=1.5
    g15: Circle CenterX=22.8662 CenterY=-147.31 CenterZ=0 NormalX=0 NormalY=0 NormalZ=1 AngleXU=0 Radius=1.5
  constraints (42):
    c: Tangent(g0,g1) = 1.5708
    c: Tangent(g1,g2) = 1.5708
    c: Tangent(g2,g3) = 1.5708
    c: Tangent(g3,g4) = 1.5708
    c: Tangent(g4,g5) = 1.5708
    c: Tangent(g5,g6) = 1.5708
    c: Tangent(g6,g7) = 1.5708
    c: Tangent(g7,g0) = 1.5708
    c: Horizontal(g1)
    c: Horizontal(g5)
    c: Vertical(g3)
    c: Vertical(g7)
    c: Equal(g0,g2)
    c: Equal(g2,g4)
    c: Equal(g4,g6)
    c: PointOnObject(g8,g1)
    c: PointOnObject(g8,g7)
    c: PointOnObject(g9,g3)
    c: PointOnObject(g9,g5)
    c: Radius(g4) = 5
    c: DistanceY(g5,g0) = 140.898
    c: DistanceX(g0,g2) = 407.67
    c: DistanceY(g-3,g0) = 15.522
    c: DistanceX(g0,g-3) = 9.8
    c: Equal(g11,g10)
    c: Equal(g11,g15)
    c: Equal(g11,g14)
    c: Equal(g11,g13)
    c: Equal(g11,g12)
    c: Diameter(g11) = 3
    c: DistanceX(g6,g15) = 5.11
    c: DistanceY(g5,g15) = 5.338
    c: DistanceY(g10,g0) = 6.06
    c: DistanceX(g0,g10) = 5.11
    c: DistanceX(g10,g11) = 207.01
    c: DistanceY(g10,g11) = -1.27
    c: DistanceY(g12,g1) = 6.06
    c: DistanceX(g12,g2) = 5.13
    c: DistanceX(g13,g3) = 5.08
    c: DistanceY(g4,g13) = 5.08
    c: DistanceY(g14,g4) = 1.052
    c: DistanceX(g14,g4) = 194.31
FEATURE [PartDesign::Pad] Pad
  Direction = (0,0,1)
  Length = 2
  Length2 = 10
  Profile = -> Sketch001
  ReferenceAxis = -> Sketch001 [N_Axis]
  Reversed = true
  Type = 0
FEATURE [PartDesign::Pocket] Pocket
  BaseFeature = -> Pad
  Direction = (0,0,-1)
  Length = 3
  Length2 = 5
  Profile = -> Sketch
  ReferenceAxis = -> Sketch [N_Axis]
  TaperAngle = -1
  Type = 0
FEATURE [PartDesign::Body] Body  label="Main Plate"
  Group = -> [Sketch,Sketch001,Pad,Pocket]
  Origin = -> Origin
  Tip = -> Pocket
FEATURE [Sketcher::SketchObject] Sketch003  label="PCB outline"
  FullyConstrained = true
  MapMode = 5
  Placement = pos=(0,0,-6.4) rot=(0,0,1;0rad)
  sketch-geometry (21):
    g0: ArcOfCircle CenterX=22.7562 CenterY=-16.7502 CenterZ=0 NormalX=0 NormalY=0 NormalZ=1 AngleXU=0 Radius=5 StartAngle=1.5708 EndAngle=3.14159
    g1: ArcOfCircle CenterX=420.426 CenterY=-16.7502 CenterZ=0 NormalX=0 NormalY=0 NormalZ=1 AngleXU=0 Radius=5 StartAngle=0 EndAngle=1.5708
    g2: LineSegment StartX=425.426 StartY=-16.7502 StartZ=0 EndX=425.426 EndY=-147.648 EndZ=0
    g3: ArcOfCircle CenterX=420.426 CenterY=-147.648 CenterZ=0 NormalX=0 NormalY=0 NormalZ=1 AngleXU=0 Radius=5 StartAngle=4.71239 EndAngle=6.28319
    g4: LineSegment StartX=420.426 StartY=-152.648 StartZ=0 EndX=22.7562 EndY=-152.648 EndZ=0
    g5: ArcOfCircle CenterX=22.7562 CenterY=-147.648 CenterZ=0 NormalX=0 NormalY=0 NormalZ=1 AngleXU=0 Radius=5 StartAngle=3.14159 EndAngle=4.71239
    g6: LineSegment StartX=17.7562 StartY=-147.648 StartZ=0 EndX=17.7562 EndY=-16.7502 EndZ=0
    g7: GeomPoint X=425.426 Y=-152.648 Z=0
    g8: Circle CenterX=22.8662 CenterY=-17.8102 CenterZ=0 NormalX=0 NormalY=0 NormalZ=1 AngleXU=0 Radius=1.75
    g9: Circle CenterX=229.876 CenterY=-19.0802 CenterZ=0 NormalX=0 NormalY=0 NormalZ=1 AngleXU=0 Radius=1.75
    g10: Circle CenterX=420.296 CenterY=-17.8102 CenterZ=0 NormalX=0 NormalY=0 NormalZ=1 AngleXU=0 Radius=1.75
    g11: Circle CenterX=420.346 CenterY=-147.568 CenterZ=0 NormalX=0 NormalY=0 NormalZ=1 AngleXU=0 Radius=1.75
    g12: Circle CenterX=226.116 CenterY=-148.7 CenterZ=0 NormalX=0 NormalY=0 NormalZ=1 AngleXU=0 Radius=1.75
    g13: Circle CenterX=22.8662 CenterY=-147.31 CenterZ=0 NormalX=0 NormalY=0 NormalZ=1 AngleXU=0 Radius=1.75
    g14: LineSegment StartX=420.426 StartY=-11.7502 StartZ=0 EndX=299.014 EndY=-11.7502 EndZ=0
    g15: LineSegment StartX=287.448 StartY=-9.2102 StartZ=0 EndX=296.474 EndY=-9.2102 EndZ=0
    g16: LineSegment StartX=22.7562 StartY=-11.7502 StartZ=0 EndX=284.908 EndY=-11.7502 EndZ=0
    g17: ArcOfCircle CenterX=284.908 CenterY=-10.4802 CenterZ=0 NormalX=0 NormalY=0 NormalZ=1 AngleXU=0 Radius=1.27 StartAngle=4.71239 EndAngle=6.28319
    g18: ArcOfCircle CenterX=287.448 CenterY=-10.4802 CenterZ=0 NormalX=0 NormalY=0 NormalZ=1 AngleXU=0 Radius=1.27 StartAngle=1.5708 EndAngle=3.14159
    g19: ArcOfCircle CenterX=296.474 CenterY=-10.4802 CenterZ=0 NormalX=0 NormalY=0 NormalZ=1 AngleXU=0 Radius=1.27 StartAngle=0 EndAngle=1.5708
    g20: ArcOfCircle CenterX=299.014 CenterY=-10.4802 CenterZ=0 NormalX=0 NormalY=0 NormalZ=1 AngleXU=0 Radius=1.27 StartAngle=3.14159 EndAngle=4.71239
  constraints (62):
    c: Tangent(g1,g2) = 1.5708
    c: Tangent(g2,g3) = 1.5708
    c: Tangent(g3,g4) = 1.5708
    c: Tangent(g4,g5) = 1.5708
    c: Tangent(g5,g6) = 1.5708
    c: Tangent(g6,g0) = 1.5708
    c: Horizontal(g4)
    c: Vertical(g2)
    c: Vertical(g6)
    c: Equal(g0,g1)
    c: Equal(g1,g3)
    c: Equal(g3,g5)
    c: PointOnObject(g7,g2)
    c: PointOnObject(g7,g4)
    c: Radius(g3) = 5
    c: DistanceY(g4,g0) = 140.898
    c: DistanceX(g0,g1) = 407.67
    c: Equal(g9,g8)
    c: Equal(g9,g13)
    c: Equal(g9,g12)
    c: Equal(g9,g11)
    c: Equal(g9,g10)
    c: Diameter(g9) = 3.5
    c: DistanceX(g5,g13) = 5.11
    c: DistanceY(g4,g13) = 5.338
    c: DistanceY(g8,g0) = 6.06
    c: DistanceX(g0,g8) = 5.11
    c: DistanceX(g8,g9) = 207.01
    c: DistanceY(g8,g9) = -1.27
    c: DistanceX(g10,g1) = 5.13
    c: DistanceX(g11,g2) = 5.08
    c: DistanceY(g3,g11) = 5.08
    c: DistanceY(g12,g3) = 1.052
    c: DistanceX(g12,g3) = 194.31
    c: Block(g0)
    c: Coincident(g14,g1)
    c: Horizontal(g14)
    c: Horizontal(g15)
    c: Coincident(g16,g0)
    c: Horizontal(g16)
    c: Coincident(g17,g16)
    c: Coincident(g18,g17)
    c: Coincident(g18,g15)
    c: Coincident(g19,g15)
    c: Coincident(g20,g19)
    c: Coincident(g20,g14)
    c: Vertical(g18,g15)
    c: Vertical(g19,g15)
    c: Horizontal(g19,g19)
    c: DistanceX(g19,g14) = 1.27
    c: Horizontal(g20,g19)
    c: Vertical(g20,g14)
    c: Equal(g20,g17)
    c: Equal(g19,g18)
    c: Horizontal(g14,g16)
    c: Equal(g20,g19)
    c: Horizontal(g17,g19)
    c: Vertical(g17,g16)
    c: Vertical(g1,g1)
    c: DistanceX(g14,g1) = 121.412
    c: DistanceX(g15,g15) = 9.026
    c: DistanceY(g10,g1) = 6.06
FEATURE [PartDesign::Pad] Pad001
  Direction = (0,0,1)
  Length = 1.6
  Length2 = 10
  Placement = pos=(0,0,-6.4) rot=(0,0,1;0rad)
  Profile = -> Sketch003
  ReferenceAxis = -> Sketch003 [N_Axis]
  Type = 0
FEATURE [PartDesign::SubShapeBinder] Binder  label="PCB Binder"
  BindCopyOnChange = 0
  BindMode = 0
  ClaimChildren = false
  Context = -> Body002 [Binder.]
  Fuse = false
  MakeFace = true
  OffsetFill = false
  OffsetIntersection = false
  OffsetJoinType = 0
  OffsetOpenResult = false
  PartialLoad = false
  Relative = true
  Support = -> [Body001[Pad001.Sketch003.]]
  _Version = 2
FEATURE [Sketcher::SketchObject] Sketch004  label="Outer wall top"
  ExternalGeometry = -> [Binder]
  FullyConstrained = true
  MapMode = 5
  Placement = pos=(0,0,-6.4) rot=(0,0,1;0rad)
  Support = -> [Binder]
  sketch-geometry (10):
    g0: ArcOfCircle CenterX=20.2562 CenterY=-14.2502 CenterZ=0 NormalX=0 NormalY=0 NormalZ=1 AngleXU=0 Radius=5 StartAngle=1.5708 EndAngle=3.14159
    g1: LineSegment StartX=20.2562 StartY=-9.2502 StartZ=0 EndX=422.926 EndY=-9.2502 EndZ=0
    g2: ArcOfCircle CenterX=422.926 CenterY=-14.2502 CenterZ=0 NormalX=0 NormalY=0 NormalZ=1 AngleXU=0 Radius=5 StartAngle=2e-16 EndAngle=1.5708
    g3: LineSegment StartX=427.926 StartY=-14.2502 StartZ=0 EndX=427.926 EndY=-150.148 EndZ=0
    g4: ArcOfCircle CenterX=422.926 CenterY=-150.148 CenterZ=0 NormalX=0 NormalY=0 NormalZ=1 AngleXU=0 Radius=5 StartAngle=4.71239 EndAngle=6.28319
    g5: LineSegment StartX=422.926 StartY=-155.148 StartZ=0 EndX=20.2562 EndY=-155.148 EndZ=0
    g6: ArcOfCircle CenterX=20.2562 CenterY=-150.148 CenterZ=0 NormalX=0 NormalY=0 NormalZ=1 AngleXU=0 Radius=5 StartAngle=3.14159 EndAngle=4.71239
    g7: LineSegment StartX=15.2562 StartY=-150.148 StartZ=0 EndX=15.2562 EndY=-14.2502 EndZ=0
    g8: GeomPoint X=15.2562 Y=-9.2502 Z=0
    g9: GeomPoint X=427.926 Y=-155.148 Z=0
  constraints (24):
    c: Tangent(g0,g1) = 1.5708
    c: Tangent(g1,g2) = 1.5708
    c: Tangent(g2,g3) = 1.5708
    c: Tangent(g3,g4) = 1.5708
    c: Tangent(g4,g5) = 1.5708
    c: Tangent(g5,g6) = 1.5708
    c: Tangent(g6,g7) = 1.5708
    c: Tangent(g7,g0) = 1.5708
    c: Horizontal(g1)
    c: Horizontal(g5)
    c: Vertical(g3)
    c: Vertical(g7)
    c: Equal(g0,g2)
    c: Equal(g2,g4)
    c: Equal(g4,g6)
    c: PointOnObject(g8,g1)
    c: PointOnObject(g8,g7)
    c: PointOnObject(g9,g3)
    c: PointOnObject(g9,g5)
    c: Equal(g0,g-9)
    c: DistanceY(g-9,g0) = 2.5
    c: DistanceX(g0,g-9) = 2.5
    c: DistanceX(g-8,g3) = 2.5
    c: DistanceY(g4,g-10) = 2.5
FEATURE [PartDesign::Plane] DatumPlane  label="Outer floor plane"
  AttachmentOffset = pos=(0,0,-15) rot=(-1,0,0;0.069813rad)
  Length = 505.043
  MapMode = 2
  Placement = pos=(0,0,-21.4) rot=(-1,0,0;0.069813rad)
  ResizeMode = 0
  Support = -> [Sketch004]
  Width = 235.325
FEATURE [Sketcher::SketchObject] Sketch005  label="Outer wall floor"
  ExternalGeometry = -> [Sketch004,Binder]
  FullyConstrained = true
  MapMode = 5
  Placement = pos=(0,2e-16,-21.4) rot=(-1,0,0;0.069813rad)
  Support = -> [DatumPlane]
  sketch-geometry (10):
    g0: ArcOfCircle CenterX=20.2562 CenterY=-17.274 CenterZ=0 NormalX=0 NormalY=0 NormalZ=1 AngleXU=0 Radius=5 StartAngle=1.5708 EndAngle=3.14159
    g1: LineSegment StartX=20.2562 StartY=-12.274 StartZ=0 EndX=422.926 EndY=-12.274 EndZ=0
    g2: ArcOfCircle CenterX=422.926 CenterY=-17.274 CenterZ=0 NormalX=0 NormalY=0 NormalZ=1 AngleXU=0 Radius=5 StartAngle=2e-16 EndAngle=1.5708
    g3: LineSegment StartX=427.926 StartY=-17.274 StartZ=0 EndX=427.926 EndY=-145.817 EndZ=0
    g4: ArcOfCircle CenterX=422.926 CenterY=-145.817 CenterZ=0 NormalX=0 NormalY=0 NormalZ=1 AngleXU=0 Radius=5 StartAngle=4.71239 EndAngle=6.28319
    g5: LineSegment StartX=422.926 StartY=-150.817 StartZ=0 EndX=20.2562 EndY=-150.817 EndZ=0
    g6: ArcOfCircle CenterX=20.2562 CenterY=-145.817 CenterZ=0 NormalX=0 NormalY=0 NormalZ=1 AngleXU=0 Radius=5 StartAngle=3.14159 EndAngle=4.71239
    g7: LineSegment StartX=15.2562 StartY=-145.817 StartZ=0 EndX=15.2562 EndY=-17.274 EndZ=0
    g8: GeomPoint X=15.2562 Y=-12.274 Z=0
    g9: GeomPoint X=427.926 Y=-150.817 Z=0
  constraints (24):
    c: Tangent(g0,g1) = 1.5708
    c: Tangent(g1,g2) = 1.5708
    c: Tangent(g2,g3) = 1.5708
    c: Tangent(g3,g4) = 1.5708
    c: Tangent(g4,g5) = 1.5708
    c: Tangent(g5,g6) = 1.5708
    c: Tangent(g6,g7) = 1.5708
    c: Tangent(g7,g0) = 1.5708
    c: Horizontal(g1)
    c: Horizontal(g5)
    c: Vertical(g3)
    c: Vertical(g7)
    c: Equal(g0,g2)
    c: Equal(g2,g4)
    c: Equal(g4,g6)
    c: PointOnObject(g8,g1)
    c: PointOnObject(g8,g7)
    c: PointOnObject(g9,g3)
    c: PointOnObject(g9,g5)
    c: DistanceY(g-10,g4) = 5
    c: DistanceY(g0,g-4) = 2
    c: Radius(g0) = 5
    c: Vertical(g3,g-8)
    c: Vertical(g0,g-5)
FEATURE [PartDesign::Plane] DatumPlane001  label="Inner floor plane"
  AttachmentOffset = pos=(0,0,2) rot=(0,0,1;0rad)
  Length = 505.043
  MapMode = 2
  Placement = pos=(0,0.139513,-19.4049) rot=(-1,0,0;0.069813rad)
  ResizeMode = 0
  Support = -> [Sketch005]
  Width = 235.325
FEATURE [Sketcher::SketchObject] Sketch006  label="Inner floor"
  ExternalGeometry = -> [Sketch005]
  FullyConstrained = true
  MapMode = 5
  Placement = pos=(0,0.139513,-19.4049) rot=(-1,0,0;0.069813rad)
  Support = -> [DatumPlane001]
  sketch-geometry (10):
    g0: ArcOfCircle CenterX=25.2562 CenterY=-19.774 CenterZ=0 NormalX=0 NormalY=0 NormalZ=1 AngleXU=0 Radius=5 StartAngle=1.5708 EndAngle=3.14159
    g1: LineSegment StartX=25.2562 StartY=-14.774 StartZ=0 EndX=417.926 EndY=-14.774 EndZ=0
    g2: ArcOfCircle CenterX=417.926 CenterY=-19.774 CenterZ=0 NormalX=0 NormalY=0 NormalZ=1 AngleXU=0 Radius=5 StartAngle=0 EndAngle=1.5708
    g3: LineSegment StartX=422.926 StartY=-19.774 StartZ=0 EndX=422.926 EndY=-140.817 EndZ=0
    g4: ArcOfCircle CenterX=417.926 CenterY=-140.817 CenterZ=0 NormalX=0 NormalY=0 NormalZ=1 AngleXU=0 Radius=5 StartAngle=4.71239 EndAngle=6.28319
    g5: LineSegment StartX=417.926 StartY=-145.817 StartZ=0 EndX=25.2562 EndY=-145.817 EndZ=0
    g6: ArcOfCircle CenterX=25.2562 CenterY=-140.817 CenterZ=0 NormalX=0 NormalY=0 NormalZ=1 AngleXU=0 Radius=5 StartAngle=3.14159 EndAngle=4.71239
    g7: LineSegment StartX=20.2562 StartY=-140.817 StartZ=0 EndX=20.2562 EndY=-19.774 EndZ=0
    g8: GeomPoint X=20.2562 Y=-14.774 Z=0
    g9: GeomPoint X=422.926 Y=-145.817 Z=0
  constraints (24):
    c: Tangent(g0,g1) = 1.5708
    c: Tangent(g1,g2) = 1.5708
    c: Tangent(g2,g3) = 1.5708
    c: Tangent(g3,g4) = 1.5708
    c: Tangent(g4,g5) = 1.5708
    c: Tangent(g5,g6) = 1.5708
    c: Tangent(g6,g7) = 1.5708
    c: Tangent(g7,g0) = 1.5708
    c: Horizontal(g1)
    c: Horizontal(g5)
    c: Vertical(g3)
    c: Vertical(g7)
    c: Equal(g0,g2)
    c: Equal(g2,g4)
    c: Equal(g4,g6)
    c: PointOnObject(g8,g1)
    c: PointOnObject(g8,g7)
    c: PointOnObject(g9,g3)
    c: PointOnObject(g9,g5)
    c: DistanceX(g-3,g0) = 5
    c: DistanceY(g0,g-3) = 2.5
    c: DistanceX(g3,g-4) = 5
    c: DistanceY(g-4,g4) = 5
    c: Equal(g-3,g0)
FEATURE [PartDesign::AdditiveLoft] AdditiveLoft
  Closed = false
  Profile = -> Sketch004
  Ruled = false
  Sections = -> [Sketch005]
FEATURE [Sketcher::SketchObject] Sketch007  label="Inner top"
  ExternalGeometry = -> [Sketch004,Binder]
  FullyConstrained = true
  MapMode = 5
  Placement = pos=(0,0,-6.4) rot=(0,0,1;0rad)
  Support = -> [Binder]
  sketch-geometry (13):
    g0: LineSegment StartX=423.426 StartY=-28.7502 StartZ=0 EndX=423.426 EndY=-141.738 EndZ=0
    g1: LineSegment StartX=414.516 StartY=-150.648 StartZ=0 EndX=231.116 EndY=-150.648 EndZ=0
    g2: LineSegment StartX=19.7562 StartY=-141.738 StartZ=0 EndX=19.7562 EndY=-28.7502 EndZ=0
    g3: GeomPoint X=423.426 Y=-150.648 Z=0
    g4: LineSegment StartX=28.6662 StartY=-150.648 StartZ=0 EndX=221.116 EndY=-150.648 EndZ=0
    g5: LineSegment StartX=34.7562 StartY=-13.7502 StartZ=0 EndX=214.876 EndY=-13.7502 EndZ=0
    g6: LineSegment StartX=244.876 StartY=-13.7502 StartZ=0 EndX=408.426 EndY=-13.7502 EndZ=0
    g7: ArcOfCircle CenterX=19.7562 CenterY=-13.7502 CenterZ=0 NormalX=0 NormalY=0 NormalZ=1 AngleXU=0 Radius=15 StartAngle=4.71239 EndAngle=6.28319
    g8: ArcOfCircle CenterX=19.7562 CenterY=-150.648 CenterZ=0 NormalX=0 NormalY=0 NormalZ=1 AngleXU=0 Radius=8.91 StartAngle=0 EndAngle=1.5708
    g9: ArcOfCircle CenterX=226.116 CenterY=-150.648 CenterZ=0 NormalX=0 NormalY=0 NormalZ=1 AngleXU=0 Radius=5 StartAngle=0 EndAngle=3.14159
    g10: ArcOfCircle CenterX=229.876 CenterY=-13.7502 CenterZ=0 NormalX=0 NormalY=0 NormalZ=1 AngleXU=0 Radius=15 StartAngle=3.14159 EndAngle=6.28319
    g11: ArcOfCircle CenterX=423.426 CenterY=-13.7502 CenterZ=0 NormalX=0 NormalY=0 NormalZ=1 AngleXU=0 Radius=15 StartAngle=3.14159 EndAngle=4.71239
    g12: ArcOfCircle CenterX=423.426 CenterY=-150.648 CenterZ=0 NormalX=0 NormalY=0 NormalZ=1 AngleXU=0 Radius=8.91 StartAngle=1.5708 EndAngle=3.14159
  constraints (44):
    c: Horizontal(g1)
    c: Vertical(g0)
    c: Vertical(g2)
    c: PointOnObject(g3,g0)
    c: PointOnObject(g3,g1)
    c: Horizontal(g4)
    c: Horizontal(g5)
    c: Horizontal(g6)
    c: Coincident(g7,g5)
    c: Coincident(g7,g2)
    c: Vertical(g7,g2)
    c: Horizontal(g7,g5)
    c: Coincident(g8,g2)
    c: Coincident(g8,g4)
    c: Vertical(g2,g8)
    c: Horizontal(g8,g4)
    c: Horizontal(g1,g4)
    c: Coincident(g9,g4)
    c: Coincident(g9,g1)
    c: Horizontal(g9,g4)
    c: Vertical(g-9,g9)
    c: Horizontal(g6,g5)
    c: Coincident(g10,g6)
    c: Coincident(g10,g5)
    c: Vertical(g-5,g10)
    c: Coincident(g11,g6)
    c: Coincident(g11,g0)
    c: Horizontal(g11,g6)
    c: Vertical(g11,g0)
    c: Coincident(g12,g1)
    c: Horizontal(g12,g1)
    c: Vertical(g0,g12)
    c: DistanceY(g5,g-12) = 2
    c: DistanceX(g-12,g2) = 2
    c: Horizontal(g10,g5)
    c: Coincident(g12,g0)
    c: DistanceX(g0,g-13) = 2
    c: DistanceY(g-13,g1) = 2
    c: Radius(g7) = 15
    c: Radius(g10) = 15
    c: Radius(g9) = 5
    c: Equal(g8,g12)
    c: Radius(g11) = 15
    c: Radius(g8) = 8.91
FEATURE [PartDesign::SubtractiveLoft] SubtractiveLoft
  BaseFeature = -> AdditiveLoft
  Closed = false
  Profile = -> Sketch006
  Ruled = false
  Sections = -> [Sketch007]
FEATURE [Sketcher::SketchObject] Sketch008  label="Pins bottom"
  ExternalGeometry = -> [Binder]
  FullyConstrained = true
  MapMode = 5
  Placement = pos=(0,0,-6.4) rot=(0,0,1;0rad)
  Support = -> [Binder]
  sketch-geometry (6):
    g0: Circle CenterX=22.8662 CenterY=-17.8102 CenterZ=0 NormalX=0 NormalY=0 NormalZ=1 AngleXU=0 Radius=1.7
    g1: Circle CenterX=229.876 CenterY=-19.0802 CenterZ=0 NormalX=0 NormalY=0 NormalZ=1 AngleXU=0 Radius=1.7
    g2: Circle CenterX=420.296 CenterY=-17.8102 CenterZ=0 NormalX=0 NormalY=0 NormalZ=1 AngleXU=0 Radius=1.7
    g3: Circle CenterX=420.346 CenterY=-147.568 CenterZ=0 NormalX=0 NormalY=0 NormalZ=1 AngleXU=0 Radius=1.7
    g4: Circle CenterX=226.116 CenterY=-148.7 CenterZ=0 NormalX=0 NormalY=0 NormalZ=1 AngleXU=0 Radius=1.7
    g5: Circle CenterX=22.8662 CenterY=-147.31 CenterZ=0 NormalX=0 NormalY=0 NormalZ=1 AngleXU=0 Radius=1.7
  constraints (12):
    c: Coincident(g0,g-3)
    c: Coincident(g1,g-4)
    c: Coincident(g2,g-5)
    c: Coincident(g3,g-6)
    c: Coincident(g4,g-7)
    c: Coincident(g5,g-8)
    c: Diameter(g0) = 3.4
    c: Equal(g1,g2)
    c: Equal(g2,g3)
    c: Equal(g3,g4)
    c: Equal(g4,g5)
    c: Equal(g5,g0)
FEATURE [PartDesign::SubShapeBinder] Binder001  label="PCB Top binder"
  BindCopyOnChange = 0
  BindMode = 0
  ClaimChildren = false
  Context = -> Body003 [Binder001.]
  Fuse = false
  MakeFace = true
  OffsetFill = false
  OffsetIntersection = false
  OffsetJoinType = 0
  OffsetOpenResult = false
  PartialLoad = false
  Relative = true
  Support = -> [Body001[Pad001.Face22]]
  _Version = 2
FEATURE [Sketcher::SketchObject] Sketch010  label="Support"
  ExternalGeometry = -> [Binder001]
  FullyConstrained = true
  MapMode = 5
  Placement = pos=(0,0,-4.8) rot=(0,0,1;0rad)
  Support = -> [Binder001]
  sketch-geometry (27):
    g0: LineSegment StartX=26.3662 StartY=-147.31 StartZ=0 EndX=220.795 EndY=-147.31 EndZ=0
    g1: ArcOfCircle CenterX=22.8662 CenterY=-147.31 CenterZ=0 NormalX=0 NormalY=0 NormalZ=1 AngleXU=0 Radius=3.5 StartAngle=-1.8e-15 EndAngle=1.5708
    g2: LineSegment StartX=22.8662 StartY=-143.81 StartZ=0 EndX=22.8662 EndY=-24.0802 EndZ=0
    g3: LineSegment StartX=231.438 StartY=-147.31 StartZ=0 EndX=411.438 EndY=-147.31 EndZ=0
    g4: ArcOfCircle CenterX=226.116 CenterY=-148.7 CenterZ=0 NormalX=0 NormalY=0 NormalZ=1 AngleXU=0 Radius=5.5 StartAngle=0.255498 EndAngle=2.88609
    g5: LineSegment StartX=422.926 StartY=-77.6482 StartZ=0 EndX=422.926 EndY=-24.2973 EndZ=0
    g6: LineSegment StartX=417.346 StartY=-143.648 StartZ=0 EndX=417.346 EndY=-85.6482 EndZ=0
    g7: LineSegment StartX=417.346 StartY=-85.6482 StartZ=0 EndX=422.926 EndY=-77.6482 EndZ=0
    g8: LineSegment StartX=417.346 StartY=-143.648 StartZ=0 EndX=411.438 EndY=-147.31 EndZ=0
    g9: ArcOfCircle CenterX=420.296 CenterY=-17.8102 CenterZ=0 NormalX=0 NormalY=0 NormalZ=1 AngleXU=0 Radius=7 StartAngle=2.09502 EndAngle=5.09756
    g10: LineSegment StartX=416.792 StartY=-11.7502 StartZ=0 EndX=420.426 EndY=-11.7502 EndZ=0
    g11: LineSegment StartX=425.426 StartY=-16.7502 StartZ=0 EndX=425.426 EndY=-147.648 EndZ=0
    g12: LineSegment StartX=420.426 StartY=-152.648 StartZ=0 EndX=22.7562 EndY=-152.648 EndZ=0
    g13: LineSegment StartX=17.7562 StartY=-147.648 StartZ=0 EndX=17.7562 EndY=-16.7502 EndZ=0
    g14: ArcOfCircle CenterX=22.7562 CenterY=-147.648 CenterZ=0 NormalX=0 NormalY=0 NormalZ=1 AngleXU=0 Radius=5 StartAngle=3.14159 EndAngle=4.71239
    g15: ArcOfCircle CenterX=420.426 CenterY=-147.648 CenterZ=0 NormalX=0 NormalY=0 NormalZ=1 AngleXU=0 Radius=5 StartAngle=4.71239 EndAngle=6.28319
    g16: ArcOfCircle CenterX=420.426 CenterY=-16.7502 CenterZ=0 NormalX=0 NormalY=0 NormalZ=1 AngleXU=0 Radius=5 StartAngle=0 EndAngle=1.5708
    g17: LineSegment StartX=22.7562 StartY=-11.7502 StartZ=0 EndX=249.876 EndY=-11.7502 EndZ=0
    g18: LineSegment StartX=22.8662 StartY=-24.0802 StartZ=0 EndX=249.876 EndY=-24.0802 EndZ=0
    g19: ArcOfCircle CenterX=22.7562 CenterY=-16.7502 CenterZ=0 NormalX=0 NormalY=0 NormalZ=1 AngleXU=0 Radius=5 StartAngle=1.5708 EndAngle=3.14159
    g20: ArcOfCircle CenterX=249.876 CenterY=-17.9152 CenterZ=0 NormalX=0 NormalY=0 NormalZ=1 AngleXU=0 Radius=6.165 StartAngle=4.71239 EndAngle=7.85398
    g21: Circle CenterX=229.876 CenterY=-19.0802 CenterZ=0 NormalX=0 NormalY=0 NormalZ=1 AngleXU=0 Radius=2
    g22: Circle CenterX=22.8662 CenterY=-17.8102 CenterZ=0 NormalX=0 NormalY=0 NormalZ=1 AngleXU=0 Radius=2
    g23: Circle CenterX=22.8662 CenterY=-147.31 CenterZ=0 NormalX=0 NormalY=0 NormalZ=1 AngleXU=0 Radius=2
    g24: Circle CenterX=226.116 CenterY=-148.7 CenterZ=0 NormalX=0 NormalY=0 NormalZ=1 AngleXU=0 Radius=2
    g25: Circle CenterX=420.346 CenterY=-147.568 CenterZ=0 NormalX=0 NormalY=0 NormalZ=1 AngleXU=0 Radius=2
    g26: Circle CenterX=420.296 CenterY=-17.8102 CenterZ=0 NormalX=0 NormalY=0 NormalZ=1 AngleXU=0 Radius=2
  constraints (78):
    c: Horizontal(g0)
    c: Coincident(g1,g-8)
    c: Coincident(g1,g0)
    c: Radius(g1) = 3.5
    c: Coincident(g2,g1)
    c: Vertical(g2)
    c: Horizontal(g0,g1)
    c: Horizontal(g3)
    c: Coincident(g4,g3)
    c: Coincident(g4,g0)
    c: Coincident(g4,g-7)
    c: Radius(g4) = 5.5
    c: Horizontal(g0,g3)
    c: Vertical(g5)
    c: DistanceX(g5,g-12) = 2.5
    c: DistanceY(g-12,g5) = 70
    c: Vertical(g6)
    c: Coincident(g7,g6)
    c: Coincident(g7,g5)
    c: DistanceX(g6,g-6) = 3
    c: Coincident(g8,g6)
    c: Coincident(g8,g3)
    c: DistanceY(g-12,g6) = 4
    c: DistanceX(g3,g3) = 180
    c: Coincident(g9,g5)
    c: Coincident(g9,g-5)
    c: Radius(g9) = 7
    c: Coincident(g10,g9)
    c: Horizontal(g10)
    c: Vertical(g11)
    c: Horizontal(g12)
    c: Vertical(g13)
    c: Coincident(g14,g13)
    c: Coincident(g14,g12)
    c: Coincident(g15,g12)
    c: Coincident(g15,g11)
    c: Coincident(g16,g10)
    c: Coincident(g16,g11)
    c: Vertical(g16,g10)
    c: Horizontal(g16,g11)
    c: Equal(g16,g-11)
    c: Vertical(g15,g12)
    c: Horizontal(g15,g11)
    c: Equal(g15,g-12)
    c: Vertical(g12,g14)
    c: Horizontal(g14,g13)
    c: Equal(g-9,g14)
    c: Coincident(g13,g-9)
    c: Coincident(g-11,g11)
    c: DistanceY(g6,g6) = 58
    c: Horizontal(g17)
    c: Horizontal(g18)
    c: DistanceY(g18,g-4) = 5
    c: Vertical(g-3,g2)
    c: Coincident(g2,g18)
    c: Coincident(g19,g13)
    c: Coincident(g19,g17)
    c: Equal(g19,g-10)
    c: Horizontal(g19,g13)
    c: Vertical(g17,g19)
    c: Horizontal(g17,g-10)
    c: Vertical(g17,g18)
    c: Coincident(g20,g17)
    c: Coincident(g20,g18)
    c: Vertical(g20,g17)
    c: DistanceX(g-4,g20) = 20
    c: Coincident(g21,g-4)
    c: Coincident(g22,g-3)
    c: Coincident(g23,g1)
    c: Coincident(g24,g4)
    c: Coincident(g25,g-6)
    c: Coincident(g26,g9)
    c: Equal(g21,g26)
    c: Equal(g26,g25)
    c: Equal(g25,g24)
    c: Equal(g24,g23)
    c: Equal(g23,g22)
    c: Diameter(g22) = 4
FEATURE [PartDesign::Pad] Pad003
  Direction = (0,0,1)
  Length = 2.8
  Length2 = 10
  Profile = -> Sketch010
  ReferenceAxis = -> Sketch010 [N_Axis]
  Type = 0
FEATURE [PartDesign::Body] Body003  label="Main plate sandwich support"
  Group = -> [Binder001,Sketch010,Pad003]
  Origin = -> Origin003
  Tip = -> Pad003
FEATURE [PartDesign::SubShapeBinder] Binder003  label="Main plate top binder"
  BindCopyOnChange = 0
  BindMode = 0
  ClaimChildren = false
  Context = -> Body002 [Binder003.]
  Fuse = false
  MakeFace = true
  OffsetFill = false
  OffsetIntersection = false
  OffsetJoinType = 0
  OffsetOpenResult = false
  PartialLoad = false
  Relative = true
  Support = -> [Body[Pad.Sketch001.]]
  _Version = 2
FEATURE [PartDesign::SubShapeBinder] Binder004  label="Case wall binder"
  BindCopyOnChange = 0
  BindMode = 0
  ClaimChildren = false
  Context = -> Body004 [Binder004.]
  Fuse = false
  MakeFace = true
  OffsetFill = false
  OffsetIntersection = false
  OffsetJoinType = 0
  OffsetOpenResult = false
  PartialLoad = false
  Relative = true
  Support = -> [Body002[Pocket003.Face11]]
  _Version = 2
FEATURE [PartDesign::SubShapeBinder] Binder005  label="Switch holes binder"
  BindCopyOnChange = 0
  BindMode = 0
  ClaimChildren = false
  Context = -> Body004 [Binder005.]
  Fuse = false
  MakeFace = true
  OffsetFill = false
  OffsetIntersection = false
  OffsetJoinType = 0
  OffsetOpenResult = false
  PartialLoad = false
  Relative = true
  Support = -> [Body[Pocket.Sketch.]]
  _Version = 2
FEATURE [Sketcher::SketchObject] Sketch013  label="Outer plate"
  ExternalGeometry = -> [Binder005,Binder004]
  FullyConstrained = true
  MapMode = 5
  Placement = pos=(0,0,5.8) rot=(0,0,1;0rad)
  Support = -> [Binder004]
  sketch-geometry (83):
    g0: ArcOfCircle CenterX=20.2562 CenterY=-14.2502 CenterZ=0 NormalX=0 NormalY=0 NormalZ=1 AngleXU=0 Radius=10 StartAngle=1.5708 EndAngle=3.14159
    g1: LineSegment StartX=20.2562 StartY=-4.2502 StartZ=0 EndX=422.926 EndY=-4.2502 EndZ=0
    g2: ArcOfCircle CenterX=422.926 CenterY=-14.2502 CenterZ=0 NormalX=0 NormalY=0 NormalZ=1 AngleXU=0 Radius=10 StartAngle=8e-16 EndAngle=1.5708
    g3: LineSegment StartX=432.926 StartY=-14.2502 StartZ=0 EndX=432.926 EndY=-145.148 EndZ=0
    g4: ArcOfCircle CenterX=422.926 CenterY=-145.148 CenterZ=0 NormalX=0 NormalY=0 NormalZ=1 AngleXU=0 Radius=10 StartAngle=4.71239 EndAngle=6.28319
    g5: LineSegment StartX=422.926 StartY=-155.148 StartZ=0 EndX=20.2562 EndY=-155.148 EndZ=0
    g6: ArcOfCircle CenterX=20.2562 CenterY=-145.148 CenterZ=0 NormalX=0 NormalY=0 NormalZ=1 AngleXU=0 Radius=10 StartAngle=3.14159 EndAngle=4.71239
    g7: LineSegment StartX=10.2562 StartY=-145.148 StartZ=0 EndX=10.2562 EndY=-14.2502 EndZ=0
    g8: GeomPoint X=10.2562 Y=-4.2502 Z=0
    g9: GeomPoint X=432.926 Y=-155.148 Z=0
    g10: ArcOfCircle CenterX=25.2562 CenterY=-24.9722 CenterZ=0 NormalX=0 NormalY=0 NormalZ=1 AngleXU=0 Radius=1 StartAngle=1.5708 EndAngle=3.14159
    g11: LineSegment StartX=25.2562 StartY=-23.9722 StartZ=0 EndX=43.8534 EndY=-23.9722 EndZ=0
    g12: ArcOfCircle CenterX=43.8534 CenterY=-24.9722 CenterZ=0 NormalX=0 NormalY=0 NormalZ=1 AngleXU=0 Radius=1 StartAngle=5e-16 EndAngle=1.5708
    g13: LineSegment StartX=44.8534 StartY=-24.9722 StartZ=0 EndX=44.8534 EndY=-43.5694 EndZ=0
    g14: ArcOfCircle CenterX=43.8534 CenterY=-43.5694 CenterZ=0 NormalX=0 NormalY=0 NormalZ=1 AngleXU=0 Radius=1 StartAngle=4.71239 EndAngle=6.28319
    g15: LineSegment StartX=43.8534 StartY=-44.5694 StartZ=0 EndX=25.2562 EndY=-44.5694 EndZ=0
    g16: ArcOfCircle CenterX=25.2562 CenterY=-43.5694 CenterZ=0 NormalX=0 NormalY=0 NormalZ=1 AngleXU=0 Radius=1 StartAngle=3.14159 EndAngle=4.71239
    g17: LineSegment StartX=24.2562 StartY=-43.5694 StartZ=0 EndX=24.2562 EndY=-24.9722 EndZ=0
    g18: GeomPoint X=24.2562 Y=-23.9722 Z=0
    g19: GeomPoint X=44.8534 Y=-44.5694 Z=0
    g20: ArcOfCircle CenterX=63.3534 CenterY=-24.9722 CenterZ=0 NormalX=0 NormalY=0 NormalZ=1 AngleXU=0 Radius=1 StartAngle=1.5708 EndAngle=3.14159
    g21: LineSegment StartX=63.3534 StartY=-23.9722 StartZ=0 EndX=139.103 EndY=-23.9722 EndZ=0
    g22: ArcOfCircle CenterX=139.103 CenterY=-24.9722 CenterZ=0 NormalX=0 NormalY=0 NormalZ=1 AngleXU=0 Radius=1 StartAngle=5e-16 EndAngle=1.5708
    g23: LineSegment StartX=140.103 StartY=-24.9722 StartZ=0 EndX=140.103 EndY=-43.5694 EndZ=0
    g24: ArcOfCircle CenterX=139.103 CenterY=-43.5694 CenterZ=0 NormalX=0 NormalY=0 NormalZ=1 AngleXU=0 Radius=1 StartAngle=4.71239 EndAngle=6.28319
    g25: LineSegment StartX=139.103 StartY=-44.5694 StartZ=0 EndX=63.3534 EndY=-44.5694 EndZ=0
    g26: ArcOfCircle CenterX=63.3534 CenterY=-43.5694 CenterZ=0 NormalX=0 NormalY=0 NormalZ=1 AngleXU=0 Radius=1 StartAngle=3.14159 EndAngle=4.71239
    g27: LineSegment StartX=62.3534 StartY=-43.5694 StartZ=0 EndX=62.3534 EndY=-24.9722 EndZ=0
    g28: GeomPoint X=62.3534 Y=-23.9722 Z=0
    g29: GeomPoint X=140.103 Y=-44.5694 Z=0
    g30: ArcOfCircle CenterX=149.078 CenterY=-24.9722 CenterZ=0 NormalX=0 NormalY=0 NormalZ=1 AngleXU=0 Radius=1 StartAngle=1.5708 EndAngle=3.14159
    g31: LineSegment StartX=149.078 StartY=-23.9722 StartZ=0 EndX=224.828 EndY=-23.9722 EndZ=0
    g32: ArcOfCircle CenterX=224.828 CenterY=-24.9722 CenterZ=0 NormalX=0 NormalY=0 NormalZ=1 AngleXU=0 Radius=1 StartAngle=5e-16 EndAngle=1.5708
    g33: LineSegment StartX=225.828 StartY=-24.9722 StartZ=0 EndX=225.828 EndY=-43.5694 EndZ=0
    g34: ArcOfCircle CenterX=224.828 CenterY=-43.5694 CenterZ=0 NormalX=0 NormalY=0 NormalZ=1 AngleXU=0 Radius=1 StartAngle=4.71239 EndAngle=6.28319
    g35: LineSegment StartX=224.828 StartY=-44.5694 StartZ=0 EndX=149.078 EndY=-44.5694 EndZ=0
    g36: ArcOfCircle CenterX=149.078 CenterY=-43.5694 CenterZ=0 NormalX=0 NormalY=0 NormalZ=1 AngleXU=0 Radius=1 StartAngle=3.14159 EndAngle=4.71239
    g37: LineSegment StartX=148.078 StartY=-43.5694 StartZ=0 EndX=148.078 EndY=-24.9722 EndZ=0
    g38: GeomPoint X=148.078 Y=-23.9722 Z=0
    g39: GeomPoint X=225.828 Y=-44.5694 Z=0
    g40: ArcOfCircle CenterX=234.803 CenterY=-24.9722 CenterZ=0 NormalX=0 NormalY=0 NormalZ=1 AngleXU=0 Radius=1 StartAngle=1.5708 EndAngle=3.14159
    g41: LineSegment StartX=234.803 StartY=-23.9722 StartZ=0 EndX=310.553 EndY=-23.9722 EndZ=0
    g42: ArcOfCircle CenterX=310.553 CenterY=-24.9722 CenterZ=0 NormalX=0 NormalY=0 NormalZ=1 AngleXU=0 Radius=1 StartAngle=-1.8e-15 EndAngle=1.5708
    g43: LineSegment StartX=311.553 StartY=-24.9722 StartZ=0 EndX=311.553 EndY=-43.5694 EndZ=0
    g44: ArcOfCircle CenterX=310.553 CenterY=-43.5694 CenterZ=0 NormalX=0 NormalY=0 NormalZ=1 AngleXU=0 Radius=1 StartAngle=4.71239 EndAngle=6.28319
    g45: LineSegment StartX=310.553 StartY=-44.5694 StartZ=0 EndX=234.803 EndY=-44.5694 EndZ=0
    g46: ArcOfCircle CenterX=234.803 CenterY=-43.5694 CenterZ=0 NormalX=0 NormalY=0 NormalZ=1 AngleXU=0 Radius=1 StartAngle=3.14159 EndAngle=4.71239
    g47: LineSegment StartX=233.803 StartY=-43.5694 StartZ=0 EndX=233.803 EndY=-24.9722 EndZ=0
    g48: GeomPoint X=233.803 Y=-23.9722 Z=0
    g49: GeomPoint X=311.553 Y=-44.5694 Z=0
    g50: ArcOfCircle CenterX=25.2562 CenterY=-48.7847 CenterZ=0 NormalX=0 NormalY=0 NormalZ=1 AngleXU=0 Radius=1 StartAngle=1.5708 EndAngle=3.14159
    g51: LineSegment StartX=25.2562 StartY=-47.7847 StartZ=0 EndX=310.553 EndY=-47.7847 EndZ=0
    g52: ArcOfCircle CenterX=310.553 CenterY=-48.7847 CenterZ=0 NormalX=0 NormalY=0 NormalZ=1 AngleXU=0 Radius=1 StartAngle=1.8e-15 EndAngle=1.5708
    g53: LineSegment StartX=303.407 StartY=-144.57 StartZ=0 EndX=25.2562 EndY=-144.57 EndZ=0
    g54: ArcOfCircle CenterX=25.2562 CenterY=-143.57 CenterZ=0 NormalX=0 NormalY=0 NormalZ=1 AngleXU=0 Radius=1 StartAngle=3.14159 EndAngle=4.71239
    g55: LineSegment StartX=24.2562 StartY=-143.57 StartZ=0 EndX=24.2562 EndY=-48.7847 EndZ=0
    g56: GeomPoint X=24.2562 Y=-47.7847 Z=0
    g57: ArcOfCircle CenterX=315.769 CenterY=-48.7847 CenterZ=0 NormalX=0 NormalY=0 NormalZ=1 AngleXU=0 Radius=1 StartAngle=1.5708 EndAngle=3.14159
    g58: LineSegment StartX=315.769 StartY=-47.7847 StartZ=0 EndX=334.366 EndY=-47.7847 EndZ=0
    g59: ArcOfCircle CenterX=334.366 CenterY=-48.7847 CenterZ=0 NormalX=0 NormalY=0 NormalZ=1 AngleXU=0 Radius=1 StartAngle=6e-16 EndAngle=1.5708
    g60: LineSegment StartX=335.366 StartY=-48.7847 StartZ=0 EndX=335.366 EndY=-143.57 EndZ=0
    g61: ArcOfCircle CenterX=334.366 CenterY=-143.57 CenterZ=0 NormalX=0 NormalY=0 NormalZ=1 AngleXU=0 Radius=1 StartAngle=4.71239 EndAngle=6.28319
    g62: LineSegment StartX=334.366 StartY=-144.57 StartZ=0 EndX=315.769 EndY=-144.57 EndZ=0
    g63: ArcOfCircle CenterX=315.769 CenterY=-143.57 CenterZ=0 NormalX=0 NormalY=0 NormalZ=1 AngleXU=0 Radius=1 StartAngle=3.14159 EndAngle=4.71239
    g64: LineSegment StartX=314.769 StartY=-143.57 StartZ=0 EndX=314.769 EndY=-48.7847 EndZ=0
    g65: GeomPoint X=314.769 Y=-47.7847 Z=0
    g66: GeomPoint X=335.366 Y=-144.57 Z=0
    g67: ArcOfCircle CenterX=339.581 CenterY=-48.7847 CenterZ=0 NormalX=0 NormalY=0 NormalZ=1 AngleXU=0 Radius=1 StartAngle=1.5708 EndAngle=3.14159
    g68: LineSegment StartX=339.581 StartY=-47.7847 StartZ=0 EndX=415.329 EndY=-47.7847 EndZ=0
    g69: ArcOfCircle CenterX=415.329 CenterY=-48.7847 CenterZ=0 NormalX=0 NormalY=0 NormalZ=1 AngleXU=0 Radius=1 StartAngle=-2.7e-15 EndAngle=1.5708
    g70: LineSegment StartX=416.329 StartY=-48.7847 StartZ=0 EndX=416.329 EndY=-143.57 EndZ=0
    g71: ArcOfCircle CenterX=415.329 CenterY=-143.57 CenterZ=0 NormalX=0 NormalY=0 NormalZ=1 AngleXU=0 Radius=1 StartAngle=4.71239 EndAngle=6.28319
    g72: LineSegment StartX=415.329 StartY=-144.57 StartZ=0 EndX=339.581 EndY=-144.57 EndZ=0
    g73: ArcOfCircle CenterX=339.581 CenterY=-143.57 CenterZ=0 NormalX=0 NormalY=0 NormalZ=1 AngleXU=0 Radius=1 StartAngle=3.14159 EndAngle=4.71239
    g74: LineSegment StartX=338.581 StartY=-143.57 StartZ=0 EndX=338.581 EndY=-48.7847 EndZ=0
    g75: GeomPoint X=338.581 Y=-47.7847 Z=0
    g76: GeomPoint X=416.329 Y=-144.57 Z=0
    g77: LineSegment StartX=311.553 StartY=-48.7847 StartZ=0 EndX=311.553 EndY=-124.527 EndZ=0
    g78: ArcOfCircle CenterX=310.553 CenterY=-124.527 CenterZ=0 NormalX=0 NormalY=0 NormalZ=1 AngleXU=0 Radius=1 StartAngle=4.71239 EndAngle=6.28319
    g79: ArcOfCircle CenterX=305.407 CenterY=-126.527 CenterZ=0 NormalX=0 NormalY=0 NormalZ=1 AngleXU=0 Radius=1 StartAngle=1.5708 EndAngle=3.14159
    g80: LineSegment StartX=310.553 StartY=-125.527 StartZ=0 EndX=305.407 EndY=-125.527 EndZ=0
    g81: ArcOfCircle CenterX=303.407 CenterY=-143.57 CenterZ=0 NormalX=0 NormalY=0 NormalZ=1 AngleXU=0 Radius=1 StartAngle=4.71239 EndAngle=6.28319
    g82: LineSegment StartX=304.407 StartY=-143.57 StartZ=0 EndX=304.407 EndY=-126.527 EndZ=0
  constraints (206):
    c: Tangent(g0,g1) = 1.5708
    c: Tangent(g1,g2) = 1.5708
    c: Tangent(g2,g3) = 1.5708
    c: Tangent(g3,g4) = 1.5708
    c: Tangent(g4,g5) = 1.5708
    c: Tangent(g5,g6) = 1.5708
    c: Tangent(g6,g7) = 1.5708
    c: Tangent(g7,g0) = 1.5708
    c: Horizontal(g1)
    c: Horizontal(g5)
    c: Vertical(g3)
    c: Vertical(g7)
    c: Equal(g0,g2)
    c: Equal(g2,g4)
    c: Equal(g4,g6)
    c: PointOnObject(g8,g1)
    c: PointOnObject(g8,g7)
    c: PointOnObject(g9,g3)
    c: PointOnObject(g9,g5)
    c: Radius(g0) = 10
    c: Tangent(g10,g11) = 1.5708
    c: Tangent(g11,g12) = 1.5708
    c: Tangent(g12,g13) = 1.5708
    c: Tangent(g13,g14) = 1.5708
    c: Tangent(g14,g15) = 1.5708
    c: Tangent(g15,g16) = 1.5708
    c: Tangent(g16,g17) = 1.5708
    c: Tangent(g17,g10) = 1.5708
    c: Horizontal(g11)
    c: Horizontal(g15)
    c: Vertical(g13)
    c: Vertical(g17)
    c: Equal(g10,g12)
    c: Equal(g12,g14)
    c: Equal(g14,g16)
    c: PointOnObject(g18,g11)
    c: PointOnObject(g18,g17)
    c: PointOnObject(g19,g13)
    c: PointOnObject(g19,g15)
    c: Radius(g10) = 1
    c: DistanceY(g-3,g10) = 3.3
    c: DistanceX(g10,g-3) = 3.3
    c: Equal(g11,g17)
    c: DistanceX(g-4,g12) = 3.3
    c: Tangent(g20,g21) = 1.5708
    c: Tangent(g21,g22) = 1.5708
    c: Tangent(g22,g23) = 1.5708
    c: Tangent(g23,g24) = 1.5708
    c: Tangent(g24,g25) = 1.5708
    c: Tangent(g25,g26) = 1.5708
    c: Tangent(g26,g27) = 1.5708
    c: Tangent(g27,g20) = 1.5708
    c: Horizontal(g21)
    c: Horizontal(g25)
    c: Vertical(g23)
    c: Vertical(g27)
    c: Equal(g20,g22)
    c: Equal(g22,g24)
    c: Equal(g24,g26)
    c: PointOnObject(g28,g21)
    c: PointOnObject(g28,g27)
    c: PointOnObject(g29,g23)
    c: PointOnObject(g29,g25)
    c: Equal(g20,g10)
    c: Equal(g27,g17)
    c: Horizontal(g20,g11)
    c: DistanceX(g26,g-6) = 3.3
    c: DistanceX(g-7,g22) = 3.3
    c: Tangent(g30,g31) = 1.5708
    c: Tangent(g31,g32) = 1.5708
    c: Tangent(g32,g33) = 1.5708
    c: Tangent(g33,g34) = 1.5708
    c: Tangent(g34,g35) = 1.5708
    c: Tangent(g35,g36) = 1.5708
    c: Tangent(g36,g37) = 1.5708
    c: Tangent(g37,g30) = 1.5708
    c: Horizontal(g31)
    c: Horizontal(g35)
    c: Vertical(g33)
    c: Vertical(g37)
    c: Equal(g30,g32)
    c: Equal(g32,g34)
    c: Equal(g34,g36)
    c: PointOnObject(g38,g31)
    c: PointOnObject(g38,g37)
    c: PointOnObject(g39,g33)
    c: PointOnObject(g39,g35)
    c: Equal(g31,g21)
    c: Equal(g37,g27)
    c: Equal(g30,g20)
    c: Horizontal(g30,g21)
    c: DistanceX(g30,g-8) = 3.3
    c: Tangent(g40,g41) = 1.5708
    c: Tangent(g41,g42) = 1.5708
    c: Tangent(g42,g43) = 1.5708
    c: Tangent(g43,g44) = 1.5708
    c: Tangent(g44,g45) = 1.5708
    c: Tangent(g45,g46) = 1.5708
    c: Tangent(g46,g47) = 1.5708
    c: Tangent(g47,g40) = 1.5708
    c: Horizontal(g41)
    c: Horizontal(g45)
    c: Vertical(g43)
    c: Vertical(g47)
    c: Equal(g40,g42)
    c: Equal(g42,g44)
    c: Equal(g44,g46)
    c: PointOnObject(g48,g41)
    c: PointOnObject(g48,g47)
    c: PointOnObject(g49,g43)
    c: PointOnObject(g49,g45)
    c: Equal(g30,g40)
    c: Equal(g41,g31)
    c: Equal(g47,g37)
    c: Horizontal(g40,g30)
    c: DistanceX(g46,g-10) = 3.3
    c: Tangent(g50,g51) = 1.5708
    c: Tangent(g51,g52) = 1.5708
    c: Tangent(g53,g54) = 1.5708
    c: Tangent(g54,g55) = 1.5708
    c: Tangent(g55,g50) = 1.5708
    c: Horizontal(g51)
    c: Horizontal(g53)
    c: Vertical(g55)
    c: Equal(g50,g52)
    c: PointOnObject(g56,g51)
    c: PointOnObject(g56,g55)
    c: Equal(g50,g10)
    c: Vertical(g50,g10)
    c: DistanceY(g-19,g50) = 3.3
    c: DistanceY(g53,g-16) = 3.3
    c: Tangent(g57,g58) = 1.5708
    c: Tangent(g58,g59) = 1.5708
    c: Tangent(g59,g60) = 1.5708
    c: Tangent(g60,g61) = 1.5708
    c: Tangent(g61,g62) = 1.5708
    c: Tangent(g62,g63) = 1.5708
    c: Tangent(g63,g64) = 1.5708
    c: Tangent(g64,g57) = 1.5708
    c: Horizontal(g58)
    c: Vertical(g60)
    c: Vertical(g64)
    c: Equal(g57,g59)
    c: Equal(g59,g61)
    c: Equal(g61,g63)
    c: PointOnObject(g65,g58)
    c: PointOnObject(g65,g64)
    c: PointOnObject(g66,g60)
    c: PointOnObject(g66,g62)
    c: Equal(g57,g52)
    c: Equal(g58,g11)
    c: Horizontal(g57,g51)
    c: DistanceX(g57,g-12) = 3.3
    c: Tangent(g67,g68) = 1.5708
    c: Tangent(g68,g69) = 1.5708
    c: Tangent(g69,g70) = 1.5708
    c: Tangent(g70,g71) = 1.5708
    c: Tangent(g71,g72) = 1.5708
    c: Tangent(g72,g73) = 1.5708
    c: Tangent(g73,g74) = 1.5708
    c: Tangent(g74,g67) = 1.5708
    c: Horizontal(g68)
    c: Horizontal(g72)
    c: Vertical(g70)
    c: Vertical(g74)
    c: Equal(g67,g69)
    c: Equal(g69,g71)
    c: Equal(g71,g73)
    c: PointOnObject(g75,g68)
    c: PointOnObject(g75,g74)
    c: PointOnObject(g76,g70)
    c: PointOnObject(g76,g72)
    c: Equal(g67,g57)
    c: Horizontal(g67,g58)
    c: Equal(g74,g60)
    c: DistanceX(g67,g-14) = 3.3
    c: DistanceX(g-13,g69) = 3.3
    c: DistanceX(g-23,g2) = 5
    c: DistanceY(g-20,g1) = 5
    c: Coincident(g77,g52)
    c: Vertical(g77)
    c: Coincident(g78,g77)
    c: Equal(g78,g50)
    c: Horizontal(g78,g77)
    c: Vertical(g78,g78)
    c: DistanceY(g78,g-25) = 3.3
    c: Horizontal(g52,g52)
    c: Vertical(g52,g43)
    c: Vertical(g79,g79)
    c: Horizontal(g79,g79)
    c: Equal(g79,g78)
    c: Coincident(g80,g78)
    c: Coincident(g80,g79)
    c: Horizontal(g80)
    c: DistanceX(g-26,g79) = 3.3
    c: Coincident(g81,g53)
    c: Vertical(g81,g79)
    c: Horizontal(g81,g81)
    c: Vertical(g81,g53)
    c: Coincident(g82,g81)
    c: Coincident(g82,g79)
    c: Horizontal(g53,g62)
    c: Horizontal(g62,g72)
    c: Equal(g52,g81)
    c: Equal(g81,g54)
    c: Coincident(g5,g-24)
FEATURE [PartDesign::Pad] Pad005
  Direction = (0,0,1)
  Length = 1
  Length2 = 10
  Profile = -> Sketch013
  ReferenceAxis = -> Sketch013 [N_Axis]
  Type = 0
FEATURE [Part::Part2DObjectPython] ShapeString  label="Ze::Keyboard"  # Draft 2D object (typed FeaturePython)
  FontFile = <userpath>/Programming/Ze-Keyboard/fontmaking/Revamped.otf
  MakeFace = true
  Placement = pos=(331.966,-34.9679,6.8) rot=(0,0,1;0rad)
  Size = 6
  String = Ze::Keyboard
  Tracking = 0
FEATURE [Part::Part2DObjectPython] ShapeString001  label="Name text"  # Draft 2D object (typed FeaturePython)
  FontFile = <userpath>/Programming/Ze-Keyboard/fontmaking/Revamped.otf
  MakeFace = true
  Placement = pos=(336.995,-40.4963,6.8) rot=(0,0,1;0rad)
  Size = 4
  String =     Roger Vigren
  Tracking = 0
FEATURE [PartDesign::Pocket] Pocket004
  BaseFeature = -> Pad005
  Direction = (0,0,-1)
  Length = 5
  Length2 = 5
  Profile = -> ShapeString
  ReferenceAxis = -> ShapeString [N_Axis]
  Type = 1
FEATURE [PartDesign::Pocket] Pocket005
  BaseFeature = -> Pocket004
  Direction = (0,0,-1)
  Length = 5
  Length2 = 5
  Profile = -> ShapeString001
  ReferenceAxis = -> ShapeString001 [N_Axis]
  Type = 1
FEATURE [PartDesign::SubShapeBinder] Binder006  label="Case binder"
  BindCopyOnChange = 0
  BindMode = 0
  ClaimChildren = false
  Context = -> Body005 [Binder006.]
  Fuse = false
  MakeFace = true
  OffsetFill = false
  OffsetIntersection = false
  OffsetJoinType = 0
  OffsetOpenResult = false
  PartialLoad = false
  Relative = true
  Support = -> [Body002[Pocket003.Face16,Pocket003.Face36,Pocket003.Face37,Pocket003.Face17,Pocket003.Face5,Pocket003.Face12,Pocket003.Face4,Pocket003.Face8]]
  _Version = 2
FEATURE [PartDesign::Plane] DatumPlane002
  AttachmentOffset = pos=(0,0,0) rot=(0,-1,0;0.05236rad)
  Length = 185.214
  MapMode = 45
  Placement = pos=(221.591,-11.9505,-18.8331) rot=(-0.036233,0.036233,0.998686;1.57211rad)
  ResizeMode = 0
  Support = -> [Binder006]
  Width = 495.59
FEATURE [Sketcher::SketchObject] Sketch016
  ExternalGeometry = -> [Binder006]
  FullyConstrained = true
  MapMode = 5
  Placement = pos=(221.591,-11.9505,-18.8331) rot=(-0.036233,0.036233,0.998686;1.57211rad)
  Support = -> [DatumPlane002]
  sketch-geometry (10):
    g0: LineSegment StartX=-4.8862 StartY=206.335 StartZ=0 EndX=-138.735 EndY=206.335 EndZ=0
    g1: LineSegment StartX=-4.8862 StartY=-206.335 StartZ=0 EndX=-138.735 EndY=-206.335 EndZ=0
    g2: LineSegment StartX=0.0671713 StartY=-201.335 StartZ=0 EndX=0.0671713 EndY=201.335 EndZ=0
    g3: ArcOfCircle CenterX=-4.8862 CenterY=201.381 CenterZ=0 NormalX=0 NormalY=0 NormalZ=1 AngleXU=0 Radius=4.95358 StartAngle=6.27382 EndAngle=7.85398
    g4: ArcOfCircle CenterX=-4.8862 CenterY=-201.381 CenterZ=0 NormalX=0 NormalY=0 NormalZ=1 AngleXU=0 Radius=4.95358 StartAngle=4.71239 EndAngle=6.29256
    g5: LineSegment StartX=-138.735 StartY=206.335 StartZ=0 EndX=-4.8862 EndY=207.335 EndZ=0
    g6: LineSegment StartX=-138.735 StartY=-206.335 StartZ=0 EndX=-4.8862 EndY=-207.335 EndZ=0
    g7: ArcOfCircle CenterX=-4.8862 CenterY=-201.381 CenterZ=0 NormalX=0 NormalY=0 NormalZ=1 AngleXU=0 Radius=5.95355 StartAngle=4.71239 EndAngle=6.29099
    g8: ArcOfCircle CenterX=-4.8862 CenterY=201.381 CenterZ=0 NormalX=0 NormalY=0 NormalZ=1 AngleXU=0 Radius=5.95355 StartAngle=6.27538 EndAngle=7.85398
    g9: LineSegment StartX=1.06717 StartY=201.335 StartZ=0 EndX=1.06717 EndY=-201.335 EndZ=0
  constraints (28):
    c: Coincident(g0,g-3)
    c: Coincident(g0,g-6)
    c: Coincident(g1,g-5)
    c: Coincident(g1,g-7)
    c: Coincident(g2,g-5)
    c: Coincident(g2,g-4)
    c: Coincident(g3,g2)
    c: Coincident(g3,g0)
    c: Vertical(g3,g0)
    c: Coincident(g4,g1)
    c: Coincident(g4,g2)
    c: Vertical(g4,g1)
    c: Coincident(g5,g-6)
    c: Coincident(g6,g-7)
    c: Vertical(g5,g6)
    c: Vertical(g6,g1)
    c: DistanceY(g0,g5) = 1
    c: DistanceY(g6,g1) = 1
    c: Coincident(g7,g6)
    c: Coincident(g8,g5)
    c: Horizontal(g8,g2)
    c: Horizontal(g7,g2)
    c: Vertical(g7,g8)
    c: DistanceX(g2,g8) = 1
    c: Coincident(g9,g8)
    c: Coincident(g9,g7)
    c: Equal(g8,g7)
    c: Vertical(g7,g6)
FEATURE [PartDesign::SubShapeBinder] Binder008  label="USB hole binder"
  BindCopyOnChange = 0
  BindMode = 0
  ClaimChildren = false
  Context = -> Body005 [Binder008.]
  Fuse = false
  MakeFace = true
  OffsetFill = false
  OffsetIntersection = false
  OffsetJoinType = 0
  OffsetOpenResult = false
  PartialLoad = false
  Relative = true
  Support = -> [Body002[Pocket003.Edge64,Pocket003.Edge17,Pocket003.Edge16,Pocket003.Edge15,Pocket003.Edge53]]
  _Version = 2
FEATURE [PartDesign::SubShapeBinder] Binder009  label="PCB USB binder"
  BindCopyOnChange = 0
  BindMode = 0
  ClaimChildren = false
  Context = -> Body005 [Binder009.]
  Fuse = false
  MakeFace = true
  OffsetFill = false
  OffsetIntersection = false
  OffsetJoinType = 0
  OffsetOpenResult = false
  PartialLoad = false
  Relative = true
  Support = -> [Body001[Pad001.Edge27,Pad001.Edge30,Pad001.Edge33,Pad001.Edge36,Pad001.Edge39]]
  _Version = 2
FEATURE [PartDesign::SubShapeBinder] Binder010
  BindCopyOnChange = 0
  BindMode = 0
  ClaimChildren = false
  Context = -> Body005 [Binder010.]
  Fuse = false
  MakeFace = true
  OffsetFill = false
  OffsetIntersection = false
  OffsetJoinType = 0
  OffsetOpenResult = false
  PartialLoad = false
  Relative = true
  Support = -> [Body004[Pad005.Face69]]
  _Version = 2
FEATURE [Sketcher::SketchObject] Sketch015
  ExternalGeometry = -> [Binder006,Binder010]
  FullyConstrained = true
  MapMode = 5
  Placement = pos=(0,0,5.8) rot=(1,0,0;3.14159rad)
  sketch-geometry (12):
    g0: LineSegment StartX=20.2562 StartY=9.2502 StartZ=0 EndX=422.926 EndY=9.2502 EndZ=0
    g1: ArcOfCircle CenterX=422.926 CenterY=14.2502 CenterZ=0 NormalX=0 NormalY=0 NormalZ=1 AngleXU=0 Radius=10 StartAngle=4.71239 EndAngle=6.28319
    g2: LineSegment StartX=15.2562 StartY=150.148 StartZ=0 EndX=15.2562 EndY=14.2502 EndZ=0
    g3: LineSegment StartX=427.926 StartY=14.2502 StartZ=0 EndX=427.926 EndY=150.148 EndZ=0
    g4: LineSegment StartX=427.926 StartY=150.148 StartZ=0 EndX=432.926 EndY=135.148 EndZ=0
    g5: LineSegment StartX=432.926 StartY=135.148 StartZ=0 EndX=432.926 EndY=14.2502 EndZ=0
    g6: LineSegment StartX=15.2562 StartY=150.148 StartZ=0 EndX=10.2562 EndY=135.148 EndZ=0
    g7: LineSegment StartX=10.2562 StartY=135.148 StartZ=0 EndX=10.2562 EndY=14.2502 EndZ=0
    g8: ArcOfCircle CenterX=20.2562 CenterY=14.2502 CenterZ=0 NormalX=0 NormalY=0 NormalZ=1 AngleXU=0 Radius=5 StartAngle=3.14159 EndAngle=4.71239
    g9: LineSegment StartX=422.926 StartY=4.2502 StartZ=0 EndX=20.2562 EndY=4.2502 EndZ=0
    g10: ArcOfCircle CenterX=422.926 CenterY=14.2502 CenterZ=0 NormalX=0 NormalY=0 NormalZ=1 AngleXU=0 Radius=5 StartAngle=4.71239 EndAngle=6.28319
    g11: ArcOfCircle CenterX=20.2562 CenterY=14.2502 CenterZ=0 NormalX=0 NormalY=0 NormalZ=1 AngleXU=0 Radius=10 StartAngle=3.14159 EndAngle=4.71239
  constraints (30):
    c: Coincident(g7,g11)
    c: Coincident(g6,g7)
    c: Coincident(g2,g8)
    c: Coincident(g2,g6)
    c: Coincident(g9,g11)
    c: Coincident(g0,g8)
    c: Coincident(g1,g9)
    c: Coincident(g0,g10)
    c: Coincident(g3,g10)
    c: Coincident(g3,g4)
    c: Coincident(g1,g5)
    c: Coincident(g4,g5)
    c: Coincident(g-9,g2)
    c: Coincident(g2,g-6)
    c: Coincident(g0,g-6)
    c: Equal(g-6,g8)
    c: Coincident(g0,g-4)
    c: Coincident(g3,g-8)
    c: Equal(g10,g-3)
    c: Coincident(g3,g-8)
    c: DistanceY(g4,g3) = 15
    c: Horizontal(g4,g6)
    c: Coincident(g1,g-10)
    c: Vertical(g5)
    c: Coincident(g1,g-12)
    c: Equal(g1,g-13)
    c: Coincident(g7,g-11)
    c: Coincident(g9,g-11)
    c: Equal(g11,g-11)
    c: Vertical(g7)
FEATURE [PartDesign::Pad] Pad006
  Direction = (0,0,-1)
  Length = 10
  Length2 = 10
  Placement = pos=(0,0,5.8) rot=(1,0,0;3.14159rad)
  Profile = -> Sketch015
  ReferenceAxis = -> Sketch015 [N_Axis]
  Type = 3
  UpToFace = -> Pad001 [Face21]
FEATURE [Sketcher::SketchObject] Sketch017
  ExternalGeometry = -> [Pad006]
  FullyConstrained = true
  MapMode = 5
  Placement = pos=(0,1.5e-15,-6.4) rot=(1,0,0;3.14159rad)
  Support = -> [Pad006]
  sketch-geometry (12):
    g0: LineSegment StartX=20.2562 StartY=9.2502 StartZ=0 EndX=422.926 EndY=9.2502 EndZ=0
    g1: LineSegment StartX=427.926 StartY=14.2502 StartZ=0 EndX=427.926 EndY=150.148 EndZ=0
    g2: LineSegment StartX=432.926 StartY=135.148 StartZ=0 EndX=427.926 EndY=150.148 EndZ=0
    g3: LineSegment StartX=432.926 StartY=14.2502 StartZ=0 EndX=432.926 EndY=135.148 EndZ=0
    g4: LineSegment StartX=422.926 StartY=4.2502 StartZ=0 EndX=20.2562 EndY=4.2502 EndZ=0
    g5: LineSegment StartX=10.2562 StartY=14.2502 StartZ=0 EndX=10.2562 EndY=135.148 EndZ=0
    g6: LineSegment StartX=10.2562 StartY=135.148 StartZ=0 EndX=15.2562 EndY=150.148 EndZ=0
    g7: LineSegment StartX=15.2562 StartY=14.2502 StartZ=0 EndX=15.2562 EndY=150.148 EndZ=0
    g8: ArcOfCircle CenterX=20.2562 CenterY=14.2502 CenterZ=0 NormalX=0 NormalY=0 NormalZ=1 AngleXU=0 Radius=5 StartAngle=3.14159 EndAngle=4.71239
    g9: ArcOfCircle CenterX=20.2562 CenterY=14.2502 CenterZ=0 NormalX=0 NormalY=0 NormalZ=1 AngleXU=0 Radius=10 StartAngle=3.14159 EndAngle=4.71239
    g10: ArcOfCircle CenterX=422.926 CenterY=14.2502 CenterZ=0 NormalX=0 NormalY=0 NormalZ=1 AngleXU=0 Radius=10 StartAngle=4.71239 EndAngle=6.28319
    g11: ArcOfCircle CenterX=422.926 CenterY=14.2502 CenterZ=0 NormalX=0 NormalY=0 NormalZ=1 AngleXU=0 Radius=5 StartAngle=4.71239 EndAngle=6.28319
  constraints (28):
    c: Coincident(g0,g-8)
    c: Coincident(g0,g-11)
    c: Coincident(g1,g-12)
    c: Coincident(g1,g-14)
    c: Coincident(g2,g-14)
    c: Coincident(g2,g1)
    c: Coincident(g3,g-13)
    c: Coincident(g3,g2)
    c: Coincident(g4,g-10)
    c: Coincident(g4,g-7)
    c: Coincident(g5,g-6)
    c: Coincident(g5,g-9)
    c: Coincident(g6,g5)
    c: Coincident(g6,g-9)
    c: Coincident(g7,g-5)
    c: Coincident(g7,g6)
    c: Coincident(g8,g7)
    c: Coincident(g8,g0)
    c: Tangent(g8,g-5)
    c: Coincident(g9,g5)
    c: Coincident(g9,g4)
    c: Tangent(g9,g-6)
    c: Coincident(g10,g4)
    c: Coincident(g10,g3)
    c: Horizontal(g10,g3)
    c: Coincident(g11,g0)
    c: Coincident(g11,g1)
    c: Horizontal(g11,g1)
FEATURE [Sketcher::SketchObject] Sketch018
  ExternalGeometry = -> [Pad001]
  FullyConstrained = true
  MapMode = 5
  Placement = pos=(0,-9.2102,-6.4) rot=(0,0.707107,0.707107;3.14159rad)
  Support = -> [Pad001]
  sketch-geometry (4):
    g0: ArcOfCircle CenterX=-295.074 CenterY=-1.6 CenterZ=0 NormalX=0 NormalY=0 NormalZ=1 AngleXU=0 Radius=1.6 StartAngle=1.5708 EndAngle=4.71239
    g1: ArcOfCircle CenterX=-289.074 CenterY=-1.6 CenterZ=0 NormalX=0 NormalY=0 NormalZ=1 AngleXU=0 Radius=1.6 StartAngle=4.71239 EndAngle=7.85398
    g2: LineSegment StartX=-295.074 StartY=-3.2 StartZ=0 EndX=-289.074 EndY=-3.2 EndZ=0
    g3: LineSegment StartX=-289.074 StartY=-2.1088e-12 StartZ=0 EndX=-295.074 EndY=-2.1065e-12 EndZ=0
  constraints (10):
    c: Tangent(g0,g2) = -1.5708
    c: Tangent(g2,g1) = -1.5708
    c: Tangent(g1,g3) = -1.5708
    c: Tangent(g3,g0) = -1.5708
    c: Equal(g0,g1)
    c: Horizontal(g2)
    c: Horizontal(g0,g-3)
    c: Diameter(g0) = 3.2
    c: DistanceX(g0,g1) = 6
    c: DistanceX(g-3,g0) = 1.4
FEATURE [PartDesign::Pad] Pad007
  BaseFeature = -> Pad001
  Direction = (0,1,-2e-16)
  Length = 7
  Length2 = 10
  Placement = pos=(0,0,-6.4) rot=(0,0,1;0rad)
  Profile = -> Sketch018
  ReferenceAxis = -> Sketch018 [N_Axis]
  Reversed = true
  Type = 0
FEATURE [PartDesign::Body] Body001  label="PCB"
  Group = -> [Sketch003,Pad001,Sketch018,Pad007]
  Origin = -> Origin001
  Tip = -> Pad007
FEATURE [PartDesign::SubShapeBinder] Binder011  label="USB Recepticle binder"
  BindCopyOnChange = 0
  BindMode = 0
  ClaimChildren = false
  Context = -> Body005 [Binder011.]
  Fuse = false
  MakeFace = true
  OffsetFill = false
  OffsetIntersection = false
  OffsetJoinType = 0
  OffsetOpenResult = false
  PartialLoad = false
  Relative = true
  Support = -> [Body001[Pad007.Face26]]
  _Version = 2
FEATURE [Sketcher::SketchObject] Sketch019
  ExternalGeometry = -> [Binder011]
  FullyConstrained = true
  MapMode = 5
  Placement = pos=(0,-9.2102,0) rot=(0,0.707107,0.707107;3.14159rad)
  Support = -> [Binder011]
  sketch-geometry (4):
    g0: ArcOfCircle CenterX=-295.074 CenterY=-8 CenterZ=0 NormalX=0 NormalY=0 NormalZ=1 AngleXU=0 Radius=2.25 StartAngle=1.5708 EndAngle=4.71239
    g1: ArcOfCircle CenterX=-289.074 CenterY=-8 CenterZ=0 NormalX=0 NormalY=0 NormalZ=1 AngleXU=0 Radius=2.25 StartAngle=4.71239 EndAngle=7.85398
    g2: LineSegment StartX=-295.074 StartY=-10.25 StartZ=0 EndX=-289.074 EndY=-10.25 EndZ=0
    g3: LineSegment StartX=-289.074 StartY=-5.75 StartZ=0 EndX=-295.074 EndY=-5.75 EndZ=0
  constraints (8):
    c: Tangent(g0,g2) = -1.5708
    c: Tangent(g2,g1) = -1.5708
    c: Tangent(g1,g3) = -1.5708
    c: Tangent(g3,g0) = -1.5708
    c: Equal(g0,g1)
    c: Coincident(g0,g-3)
    c: Coincident(g1,g-4)
    c: Diameter(g0) = 4.5
FEATURE [Part::Part2DObjectPython] Rectangle  label="Slicing plane"  # Draft 2D object (typed FeaturePython)
  Area = 33348.2
  ChamferSize = 0
  Columns = 1
  FilletRadius = 0
  Height = 202.201
  Length = 164.926
  MakeFace = true
  Placement = pos=(215.91,-190,85) rot=(0,1,0;1.5708rad)
  Rows = 1
FEATURE [Part::FeaturePython] Slice  # WARN: FeaturePython — macro-defined, semantics opaque (R4)
  Base = -> Pocket
  Mode = 1
  Tolerance = 0
  Tools = -> [Rectangle]
FEATURE [Part::FeaturePython] Slice_child0  label="Slice.0"  # WARN: FeaturePython — macro-defined, semantics opaque (R4)
  Base = -> Slice
  FilterType = 1
  Invert = false
  OverrideMaxVal = 0
  WindowFrom = 80
  WindowTo = 100
  items = 0
FEATURE [Part::FeaturePython] Slice_child1  label="Slice.1"  # WARN: FeaturePython — macro-defined, semantics opaque (R4)
  Base = -> Slice
  FilterType = 1
  Invert = false
  OverrideMaxVal = 0
  WindowFrom = 80
  WindowTo = 100
  items = 1
FEATURE [App::DocumentObjectGroup] GrExplode_Slice  label="Main Plate slices"
  Group = -> [Slice_child0,Slice_child1]
FEATURE [Part::Part2DObjectPython] Rectangle001  # Draft 2D object (typed FeaturePython)
  Area = 99861.9
  ChamferSize = 0
  Columns = 1
  FilletRadius = 0
  Height = 273.88
  Length = 364.62
  MakeFace = true
  Placement = pos=(206.71,-214.48,117.8) rot=(0,1,0;1.5708rad)
  Rows = 1
FEATURE [Part::FeaturePython] Slice001  # WARN: FeaturePython — macro-defined, semantics opaque (R4)
  Base = -> Pocket005
  Mode = 1
  Tolerance = 0
  Tools = -> [Rectangle001]
FEATURE [Part::FeaturePython] Slice001_child0  label="Slice001.0"  # WARN: FeaturePython — macro-defined, semantics opaque (R4)
  Base = -> Slice001
  FilterType = 1
  Invert = false
  OverrideMaxVal = 0
  WindowFrom = 80
  WindowTo = 100
  items = 0
FEATURE [Part::FeaturePython] Slice001_child1  label="Slice001.1"  # WARN: FeaturePython — macro-defined, semantics opaque (R4)
  Base = -> Slice001
  FilterType = 1
  Invert = false
  OverrideMaxVal = 0
  WindowFrom = 80
  WindowTo = 100
  items = 1
FEATURE [App::DocumentObjectGroup] GrExplode_Slice001  label="Top plate slices"
  Group = -> [Slice001_child0,Slice001_child1]
FEATURE [PartDesign::Fillet] Fillet
  Base = -> SubtractiveLoft [Face30]
  BaseFeature = -> SubtractiveLoft
  Radius = 2
  SupportTransform = false
  UseAllEdges = false
FEATURE [Sketcher::SketchObject] Sketch011  label="USB notch"
  ExternalGeometry = -> [Binder]
  FullyConstrained = true
  MapMode = 5
  Placement = pos=(0,0,-6.4) rot=(0,0,1;0rad)
  Support = -> [Fillet]
  sketch-geometry (4):
    g0: LineSegment StartX=284.908 StartY=-9.2102 StartZ=0 EndX=299.014 EndY=-9.2102 EndZ=0
    g1: LineSegment StartX=299.014 StartY=-9.2102 StartZ=0 EndX=299.014 EndY=-16.2102 EndZ=0
    g2: LineSegment StartX=299.014 StartY=-16.2102 StartZ=0 EndX=284.908 EndY=-16.2102 EndZ=0
    g3: LineSegment StartX=284.908 StartY=-16.2102 StartZ=0 EndX=284.908 EndY=-9.2102 EndZ=0
  constraints (12):
    c: Coincident(g0,g1)
    c: Coincident(g1,g2)
    c: Coincident(g2,g3)
    c: Coincident(g3,g0)
    c: Horizontal(g0)
    c: Horizontal(g2)
    c: Vertical(g1)
    c: Vertical(g3)
    c: PointOnObject(g-6,g1)
    c: PointOnObject(g-4,g3)
    c: Horizontal(g0,g-3)
    c: DistanceY(g2,g0) = 7
FEATURE [PartDesign::Pocket] Pocket002
  BaseFeature = -> Fillet
  Direction = (0,0,-1)
  Length = 5
  Length2 = 5
  Profile = -> Sketch011
  ReferenceAxis = -> Sketch011 [N_Axis]
  Type = 0
FEATURE [Sketcher::SketchObject] Sketch012  label="Upper wall"
  ExternalGeometry = -> [Binder003,Pocket002]
  FullyConstrained = true
  MapMode = 5
  Placement = pos=(0,0,-6.4) rot=(0,0,1;0rad)
  Support = -> [Pocket002]
  sketch-geometry (20):
    g0: ArcOfCircle CenterX=22.7562 CenterY=-16.7502 CenterZ=0 NormalX=0 NormalY=0 NormalZ=1 AngleXU=0 Radius=5 StartAngle=1.5708 EndAngle=3.14159
    g1: LineSegment StartX=22.7562 StartY=-11.7502 StartZ=0 EndX=420.426 EndY=-11.7502 EndZ=0
    g2: ArcOfCircle CenterX=420.426 CenterY=-16.7502 CenterZ=0 NormalX=0 NormalY=0 NormalZ=1 AngleXU=0 Radius=5 StartAngle=5e-16 EndAngle=1.5708
    g3: LineSegment StartX=425.426 StartY=-16.7502 StartZ=0 EndX=425.426 EndY=-147.648 EndZ=0
    g4: ArcOfCircle CenterX=420.426 CenterY=-147.648 CenterZ=0 NormalX=0 NormalY=0 NormalZ=1 AngleXU=0 Radius=5 StartAngle=4.71239 EndAngle=6.28319
    g5: LineSegment StartX=420.426 StartY=-152.648 StartZ=0 EndX=22.7562 EndY=-152.648 EndZ=0
    g6: ArcOfCircle CenterX=22.7562 CenterY=-147.648 CenterZ=0 NormalX=0 NormalY=0 NormalZ=1 AngleXU=0 Radius=5 StartAngle=3.14159 EndAngle=4.71239
    g7: LineSegment StartX=17.7562 StartY=-147.648 StartZ=0 EndX=17.7562 EndY=-16.7502 EndZ=0
    g8: GeomPoint X=17.7562 Y=-11.7502 Z=0
    g9: GeomPoint X=425.426 Y=-152.648 Z=0
    g10: ArcOfCircle CenterX=20.2562 CenterY=-14.2502 CenterZ=0 NormalX=0 NormalY=0 NormalZ=1 AngleXU=0 Radius=5 StartAngle=1.5708 EndAngle=3.14159
    g11: LineSegment StartX=20.2562 StartY=-9.2502 StartZ=0 EndX=422.926 EndY=-9.2502 EndZ=0
    g12: ArcOfCircle CenterX=422.926 CenterY=-14.2502 CenterZ=0 NormalX=0 NormalY=0 NormalZ=1 AngleXU=0 Radius=5 StartAngle=0 EndAngle=1.5708
    g13: LineSegment StartX=427.926 StartY=-14.2502 StartZ=0 EndX=427.926 EndY=-150.148 EndZ=0
    g14: ArcOfCircle CenterX=422.926 CenterY=-150.148 CenterZ=0 NormalX=0 NormalY=0 NormalZ=1 AngleXU=0 Radius=5 StartAngle=4.71239 EndAngle=6.28319
    g15: LineSegment StartX=422.926 StartY=-155.148 StartZ=0 EndX=20.2562 EndY=-155.148 EndZ=0
    g16: ArcOfCircle CenterX=20.2562 CenterY=-150.148 CenterZ=0 NormalX=0 NormalY=0 NormalZ=1 AngleXU=0 Radius=5 StartAngle=3.14159 EndAngle=4.71239
    g17: LineSegment StartX=15.2562 StartY=-150.148 StartZ=0 EndX=15.2562 EndY=-14.2502 EndZ=0
    g18: GeomPoint X=15.2562 Y=-9.2502 Z=0
    g19: GeomPoint X=427.926 Y=-155.148 Z=0
  constraints (44):
    c: Tangent(g0,g1) = 1.5708
    c: Tangent(g1,g2) = 1.5708
    c: Tangent(g2,g3) = 1.5708
    c: Tangent(g3,g4) = 1.5708
    c: Tangent(g4,g5) = 1.5708
    c: Tangent(g5,g6) = 1.5708
    c: Tangent(g6,g7) = 1.5708
    c: Tangent(g7,g0) = 1.5708
    c: Horizontal(g1)
    c: Horizontal(g5)
    c: Vertical(g3)
    c: Vertical(g7)
    c: Equal(g0,g2)
    c: Equal(g2,g4)
    c: Equal(g4,g6)
    c: PointOnObject(g8,g1)
    c: PointOnObject(g8,g7)
    c: PointOnObject(g9,g3)
    c: PointOnObject(g9,g5)
    c: Coincident(g3,g-4)
    c: Coincident(g0,g-3)
    c: Horizontal(g0,g-3)
    c: Tangent(g10,g11) = 1.5708
    c: Tangent(g11,g12) = 1.5708
    c: Tangent(g12,g13) = 1.5708
    c: Tangent(g13,g14) = 1.5708
    c: Tangent(g14,g15) = 1.5708
    c: Tangent(g15,g16) = 1.5708
    c: Tangent(g16,g17) = 1.5708
    c: Tangent(g17,g10) = 1.5708
    c: Horizontal(g11)
    c: Horizontal(g15)
    c: Vertical(g13)
    c: Vertical(g17)
    c: Equal(g10,g12)
    c: Equal(g12,g14)
    c: Equal(g14,g16)
    c: PointOnObject(g18,g11)
    c: PointOnObject(g18,g17)
    c: PointOnObject(g19,g13)
    c: PointOnObject(g19,g15)
    c: Coincident(g-6,g13)
    c: Coincident(g10,g-5)
    c: Horizontal(g10,g-5)
FEATURE [PartDesign::Pad] Pad004
  BaseFeature = -> Pocket002
  Direction = (0,0,1)
  Length = 10
  Length2 = 10
  Offset = 5.8
  Profile = -> Sketch012
  ReferenceAxis = -> Sketch012 [N_Axis]
  Type = 3
  UpToFace = -> Binder003 [Face1]
FEATURE [PartDesign::Pocket] Pocket003
  BaseFeature = -> Pad004
  Direction = (0,0,-1)
  Length = 0
  Length2 = 5
  Profile = -> Sketch011
  ReferenceAxis = -> Sketch011 [N_Axis]
  Reversed = true
  Type = 3
  UpToFace = -> Pad004 [Face11]
FEATURE [PartDesign::SubShapeBinder] Binder012  label="CaseHoleFaceBinder"
  BindCopyOnChange = 0
  BindMode = 0
  ClaimChildren = false
  Context = -> Body005 [Binder012.]
  Fuse = false
  MakeFace = true
  OffsetFill = false
  OffsetIntersection = false
  OffsetJoinType = 0
  OffsetOpenResult = false
  PartialLoad = false
  Relative = true
  Support = -> [Body002[Pocket011.Face5]]
  _Version = 2
FEATURE [Part::Part2DObjectPython] Rectangle005  label="top plate support slice plane"  # Draft 2D object (typed FeaturePython)
  Area = 117400
  ChamferSize = 0
  Columns = 1
  FilletRadius = 0
  Height = 344.217
  Length = 341.064
  MakeFace = true
  Placement = pos=(217.93,-276.14,134.8) rot=(0,1,0;1.5708rad)
  Rows = 1
FEATURE [Part::Part2DObjectPython] Rectangle006  label="CaseSlicePlane"  # Draft 2D object (typed FeaturePython)
  Area = 98483.5
  ChamferSize = 0
  Columns = 1
  FilletRadius = 0
  Height = 274.302
  Length = 359.033
  MakeFace = true
  Placement = pos=(180.41,127.11,-152.69) rot=(0.66086,-0.53069,-0.53069;1.98863rad)
  Rows = 1
FEATURE [Sketcher::SketchObject] Sketch029
  FullyConstrained = false
  MapMode = 5
  Placement = pos=(0,0,-6.4) rot=(0,0,1;0rad)
  sketch-geometry (4):
    g0: LineSegment StartX=405.426 StartY=-13.7502 StartZ=0 EndX=414.426 EndY=-13.7502 EndZ=0
    g1: LineSegment StartX=414.426 StartY=-13.7502 StartZ=0 EndX=414.426 EndY=-28.7502 EndZ=0
    g2: LineSegment StartX=414.426 StartY=-28.7502 StartZ=0 EndX=405.426 EndY=-28.7502 EndZ=0
    g3: LineSegment StartX=405.426 StartY=-28.7502 StartZ=0 EndX=405.426 EndY=-13.7502 EndZ=0
  constraints (9):
    c: Coincident(g0,g1)
    c: Coincident(g1,g2)
    c: Coincident(g2,g3)
    c: Coincident(g3,g0)
    c: Horizontal(g0)
    c: Horizontal(g2)
    c: Vertical(g1)
    c: DistanceX(g0,g0) = 9
    c: Vertical(g3)
FEATURE [PartDesign::Pocket] Pocket014
  BaseFeature = -> Pocket003
  Direction = (0,0,-1)
  Length = 10
  Length2 = 5
  Profile = -> Sketch029
  ReferenceAxis = -> Sketch029 [N_Axis]
  Type = 0
FEATURE [Sketcher::SketchObject] Sketch030
  ExternalGeometry = -> [Pocket014]
  FullyConstrained = true
  MapMode = 5
  Placement = pos=(0,0,5.8) rot=(0,0,1;0rad)
  Support = -> [Pocket014]
  sketch-geometry (16):
    g0: LineSegment StartX=425.426 StartY=-16.7502 StartZ=0 EndX=425.426 EndY=-147.648 EndZ=0
    g1: LineSegment StartX=420.426 StartY=-152.648 StartZ=0 EndX=22.7562 EndY=-152.648 EndZ=0
    g2: LineSegment StartX=17.7562 StartY=-147.648 StartZ=0 EndX=17.7562 EndY=-16.7502 EndZ=0
    g3: LineSegment StartX=22.7562 StartY=-11.7502 StartZ=0 EndX=420.426 EndY=-11.7502 EndZ=0
    g4: ArcOfCircle CenterX=420.426 CenterY=-16.7502 CenterZ=0 NormalX=0 NormalY=0 NormalZ=1 AngleXU=0 Radius=5 StartAngle=1.4e-15 EndAngle=1.5708
    g5: ArcOfCircle CenterX=420.426 CenterY=-147.648 CenterZ=0 NormalX=0 NormalY=0 NormalZ=1 AngleXU=0 Radius=5 StartAngle=4.71239 EndAngle=6.28319
    g6: ArcOfCircle CenterX=22.7562 CenterY=-16.7502 CenterZ=0 NormalX=0 NormalY=0 NormalZ=1 AngleXU=0 Radius=5 StartAngle=1.5708 EndAngle=3.14159
    g7: LineSegment StartX=22.7562 StartY=-11.6502 StartZ=0 EndX=420.426 EndY=-11.6502 EndZ=0
    g8: ArcOfCircle CenterX=22.7562 CenterY=-16.7502 CenterZ=0 NormalX=0 NormalY=0 NormalZ=1 AngleXU=0 Radius=5.1 StartAngle=1.5708 EndAngle=3.14159
    g9: ArcOfCircle CenterX=22.7562 CenterY=-147.648 CenterZ=0 NormalX=0 NormalY=0 NormalZ=1 AngleXU=0 Radius=5 StartAngle=3.14159 EndAngle=4.71239
    g10: LineSegment StartX=17.6562 StartY=-16.7502 StartZ=0 EndX=17.6562 EndY=-147.648 EndZ=0
    g11: ArcOfCircle CenterX=22.7562 CenterY=-147.648 CenterZ=0 NormalX=0 NormalY=0 NormalZ=1 AngleXU=0 Radius=5.1 StartAngle=3.14159 EndAngle=4.71239
    g12: LineSegment StartX=22.7562 StartY=-152.748 StartZ=0 EndX=420.426 EndY=-152.748 EndZ=0
    g13: ArcOfCircle CenterX=420.426 CenterY=-147.648 CenterZ=0 NormalX=0 NormalY=0 NormalZ=1 AngleXU=0 Radius=5.1 StartAngle=4.71239 EndAngle=6.28319
    g14: LineSegment StartX=425.526 StartY=-147.648 StartZ=0 EndX=425.526 EndY=-16.7502 EndZ=0
    g15: ArcOfCircle CenterX=420.426 CenterY=-16.7502 CenterZ=0 NormalX=0 NormalY=0 NormalZ=1 AngleXU=0 Radius=5.1 StartAngle=0 EndAngle=1.5708
  constraints (47):
    c: Coincident(g0,g-6)
    c: Coincident(g0,g-5)
    c: Coincident(g1,g-4)
    c: Coincident(g1,g-3)
    c: Coincident(g2,g-11)
    c: Horizontal(g3)
    c: Coincident(g4,g3)
    c: Coincident(g4,g0)
    c: Coincident(g5,g0)
    c: Coincident(g5,g1)
    c: Coincident(g-9,g6)
    c: Coincident(g6,g3)
    c: Coincident(g2,g6)
    c: Coincident(g-9,g3)
    c: Coincident(g4,g-6)
    c: Horizontal(g7)
    c: Vertical(g7,g3)
    c: Vertical(g7,g3)
    c: Coincident(g8,g7)
    c: Coincident(g8,g6)
    c: Horizontal(g8,g2)
    c: Coincident(g9,g2)
    c: Coincident(g9,g1)
    c: Vertical(g9,g-10)
    c: Coincident(g10,g8)
    c: Vertical(g10)
    c: Horizontal(g2,g10)
    c: Coincident(g11,g10)
    c: Horizontal(g11,g10)
    c: Coincident(g12,g11)
    c: Horizontal(g12)
    c: Vertical(g12,g1)
    c: Coincident(g13,g12)
    c: Horizontal(g5,g0)
    c: Horizontal(g13,g13)
    c: Vertical(g13,g12)
    c: Horizontal(g13,g0)
    c: Coincident(g14,g13)
    c: Vertical(g14)
    c: Horizontal(g14,g0)
    c: Coincident(g15,g14)
    c: Coincident(g15,g7)
    c: Horizontal(g15,g14)
    c: Vertical(g7,g15)
    c: DistanceY(g3,g7) = 0.1
    c: Vertical(g2,g-11)
    c: Vertical(g11,g11)
FEATURE [PartDesign::Pocket] Pocket015
  BaseFeature = -> Pocket014
  Direction = (0,0,-1)
  Length = 0
  Length2 = 5
  Profile = -> Sketch030
  ReferenceAxis = -> Sketch030 [N_Axis]
  Type = 3
  UpToFace = -> Pocket014 [Face40]
FEATURE [Sketcher::SketchObject] Sketch014
  ExternalGeometry = -> [Pad005]
  FullyConstrained = true
  MapMode = 5
  Placement = pos=(44.8534,0,0) rot=(0.57735,-0.57735,-0.57735;2.0944rad)
  Support = -> [Pad005]
  sketch-geometry (4):
    g0: LineSegment StartX=144.57 StartY=6.8 StartZ=0 EndX=124.07 EndY=6.8 EndZ=0
    g1: LineSegment StartX=124.07 StartY=6.8 StartZ=0 EndX=124.07 EndY=6.8 EndZ=0
    g2: LineSegment StartX=124.07 StartY=6.8 StartZ=0 EndX=144.57 EndY=6.8 EndZ=0
    g3: LineSegment StartX=144.57 StartY=6.8 StartZ=0 EndX=144.57 EndY=6.8 EndZ=0
  constraints (12):
    c: Coincident(g0,g1)
    c: Coincident(g1,g2)
    c: Coincident(g2,g3)
    c: Coincident(g3,g0)
    c: Horizontal(g0)
    c: Horizontal(g2)
    c: Vertical(g1)
    c: Vertical(g3)
    c: Vertical(g2,g-4)
    c: Horizontal(g2,g-3)
    c: Horizontal(g-3,g0)
    c: DistanceX(g1,g-5) = 19.5
FEATURE [PartDesign::Body] Body004  label="Top Plate"
  Group = -> [Binder004,Sketch013,Binder005,Pad005,Sketch014,ShapeString,ShapeString001,Pocket004,Pocket005]
  Origin = -> Origin004
  Tip = -> Pocket005
FEATURE [PartDesign::Pocket] Pocket016
  BaseFeature = -> Pocket015
  Direction = (0,0,-1)
  Length = 0
  Length2 = 5
  Offset = 1
  Profile = -> Sketch008
  ReferenceAxis = -> Sketch008 [N_Axis]
  Type = 3
  UpToFace = -> Pocket015 [Face64]
FEATURE [PartDesign::AdditiveLoft] AdditiveLoft001
  BaseFeature = -> Pad006
  Closed = false
  Placement = pos=(0,0,5.8) rot=(1,0,0;3.14159rad)
  Profile = -> Sketch016
  Ruled = false
  Sections = -> [Sketch017]
FEATURE [PartDesign::Pocket] Pocket006
  BaseFeature = -> AdditiveLoft001
  Direction = (0,-1,2e-16)
  Length = 5
  Length2 = 2
  Placement = pos=(0,0,5.8) rot=(1,0,0;3.14159rad)
  Profile = -> Sketch019
  ReferenceAxis = -> Sketch019 [N_Axis]
  Reversed = true
  Type = 4
FEATURE [Sketcher::SketchObject] Sketch031
  ExternalGeometry = -> [Pocket016,Sketch006]
  FullyConstrained = true
  MapMode = 5
  Placement = pos=(0,-13.2304,0.9373) rot=(1,0,0;1.50007rad)
  Support = -> [Pocket016]
  sketch-geometry (16):
    g0: LineSegment StartX=92.7562 StartY=-9.35569 StartZ=0 EndX=102.756 EndY=-9.35569 EndZ=0
    g1: LineSegment StartX=102.756 StartY=-9.35569 StartZ=0 EndX=102.756 EndY=-17.3557 EndZ=0
    g2: LineSegment StartX=102.756 StartY=-17.3557 StartZ=0 EndX=92.7562 EndY=-17.3557 EndZ=0
    g3: LineSegment StartX=92.7562 StartY=-17.3557 StartZ=0 EndX=92.7562 EndY=-9.35569 EndZ=0
    g4: LineSegment StartX=167.756 StartY=-9.35569 StartZ=0 EndX=177.756 EndY=-9.35569 EndZ=0
    g5: LineSegment StartX=177.756 StartY=-9.35569 StartZ=0 EndX=177.756 EndY=-17.3557 EndZ=0
    g6: LineSegment StartX=177.756 StartY=-17.3557 StartZ=0 EndX=167.756 EndY=-17.3557 EndZ=0
    g7: LineSegment StartX=167.756 StartY=-17.3557 StartZ=0 EndX=167.756 EndY=-9.35569 EndZ=0
    g8: LineSegment StartX=265.426 StartY=-9.35569 StartZ=0 EndX=275.426 EndY=-9.35569 EndZ=0
    g9: LineSegment StartX=275.426 StartY=-9.35569 StartZ=0 EndX=275.426 EndY=-17.3557 EndZ=0
    g10: LineSegment StartX=275.426 StartY=-17.3557 StartZ=0 EndX=265.426 EndY=-17.3557 EndZ=0
    g11: LineSegment StartX=265.426 StartY=-17.3557 StartZ=0 EndX=265.426 EndY=-9.35569 EndZ=0
    g12: LineSegment StartX=330.426 StartY=-9.35569 StartZ=0 EndX=340.426 EndY=-9.35569 EndZ=0
    g13: LineSegment StartX=340.426 StartY=-9.35569 StartZ=0 EndX=340.426 EndY=-17.3557 EndZ=0
    g14: LineSegment StartX=340.426 StartY=-17.3557 StartZ=0 EndX=330.426 EndY=-17.3557 EndZ=0
    g15: LineSegment StartX=330.426 StartY=-17.3557 StartZ=0 EndX=330.426 EndY=-9.35569 EndZ=0
  constraints (48):
    c: Coincident(g0,g1)
    c: Coincident(g1,g2)
    c: Coincident(g2,g3)
    c: Coincident(g3,g0)
    c: Horizontal(g0)
    c: Horizontal(g2)
    c: Vertical(g1)
    c: Vertical(g3)
    c: Coincident(g4,g5)
    c: Coincident(g5,g6)
    c: Coincident(g6,g7)
    c: Coincident(g7,g4)
    c: Horizontal(g4)
    c: Horizontal(g6)
    c: Vertical(g5)
    c: Vertical(g7)
    c: Coincident(g8,g9)
    c: Coincident(g9,g10)
    c: Coincident(g10,g11)
    c: Coincident(g11,g8)
    c: Horizontal(g8)
    c: Horizontal(g10)
    c: Vertical(g9)
    c: Vertical(g11)
    c: Coincident(g12,g13)
    c: Coincident(g13,g14)
    c: Coincident(g14,g15)
    c: Coincident(g15,g12)
    c: Horizontal(g12)
    c: Horizontal(g14)
    c: Vertical(g13)
    c: Vertical(g15)
    c: Equal(g12,g8)
    c: Equal(g8,g4)
    c: Equal(g4,g0)
    c: DistanceX(g0,g0) = 10
    c: Horizontal(g12,g8)
    c: Horizontal(g8,g4)
    c: Horizontal(g4,g0)
    c: Equal(g13,g9)
    c: Equal(g9,g5)
    c: Equal(g5,g1)
    c: DistanceY(g1,g1) = 8
    c: DistanceY(g0,g-3) = 2
    c: DistanceX(g12,g-8) = 80
    c: DistanceX(g-7,g0) = 70
    c: DistanceX(g0,g4) = 75
    c: DistanceX(g8,g12) = 65
FEATURE [PartDesign::Pad] Pad008
  BaseFeature = -> Pocket016
  Direction = (0,-0.9975,0.0706674)
  Length = 3
  Length2 = 10
  Profile = -> Sketch031
  ReferenceAxis = -> Sketch031 [N_Axis]
  Type = 0
FEATURE [PartDesign::Chamfer] Chamfer
  Angle = 45
  Base = -> Pad008 [Edge233,Edge241,Edge249,Edge257]
  BaseFeature = -> Pad008
  ChamferType = 0
  FlipDirection = false
  Size = 2.9
  Size2 = 1
  SupportTransform = false
  UseAllEdges = false
FEATURE [Sketcher::SketchObject] Sketch032  label="TopPlateSupportScrewHoles"
  ExternalGeometry = -> [Chamfer]
  FullyConstrained = true
  MapMode = 5
  Placement = pos=(0,-16.2229,1.1493) rot=(1,0,0;1.50007rad)
  Support = -> [Chamfer]
  sketch-geometry (4):
    g0: Circle CenterX=335.426 CenterY=-11.3557 CenterZ=0 NormalX=0 NormalY=0 NormalZ=1 AngleXU=0 Radius=1.45
    g1: Circle CenterX=270.426 CenterY=-11.3557 CenterZ=0 NormalX=0 NormalY=0 NormalZ=1 AngleXU=0 Radius=1.45
    g2: Circle CenterX=172.756 CenterY=-11.3557 CenterZ=0 NormalX=0 NormalY=0 NormalZ=1 AngleXU=0 Radius=1.45
    g3: Circle CenterX=97.7562 CenterY=-11.3557 CenterZ=0 NormalX=0 NormalY=0 NormalZ=1 AngleXU=0 Radius=1.45
  constraints (12):
    c: Horizontal(g1,g0)
    c: Horizontal(g0,g3)
    c: Horizontal(g3,g2)
    c: Equal(g3,g2)
    c: Equal(g2,g1)
    c: Equal(g1,g0)
    c: Diameter(g3) = 2.9
    c: DistanceX(g-3,g3) = 5
    c: DistanceY(g3,g-3) = 2
    c: DistanceX(g-4,g2) = 5
    c: DistanceX(g-5,g1) = 5
    c: DistanceX(g-6,g0) = 5
FEATURE [PartDesign::Pocket] Pocket017
  BaseFeature = -> Chamfer
  Direction = (0,0.9975,-0.0706674)
  Length = 5
  Length2 = 5
  Profile = -> Sketch032
  ReferenceAxis = -> Sketch032 [N_Axis]
  Type = 1
FEATURE [Sketcher::SketchObject] Sketch033
  ExternalGeometry = -> [Pocket017]
  FullyConstrained = true
  MapMode = 5
  Placement = pos=(0,-1.34964,-19.3007) rot=(-1,0,0;0.069813rad)
  Support = -> [Pocket017]
  sketch-geometry (4):
    g0: LineSegment StartX=215.026 StartY=-23.2812 StartZ=0 EndX=205.026 EndY=-23.2812 EndZ=0
    g1: LineSegment StartX=205.026 StartY=-23.2812 StartZ=0 EndX=230.575 EndY=-134.324 EndZ=0
    g2: LineSegment StartX=230.575 StartY=-134.324 StartZ=0 EndX=240.575 EndY=-134.324 EndZ=0
    g3: LineSegment StartX=240.575 StartY=-134.324 StartZ=0 EndX=215.026 EndY=-23.2812 EndZ=0
  constraints (12):
    c: Coincident(g0,g1)
    c: Coincident(g1,g2)
    c: Coincident(g2,g3)
    c: Coincident(g3,g0)
    c: Horizontal(g0)
    c: Horizontal(g2)
    c: Vertical(g1,g-4)
    c: Vertical(g0,g-3)
    c: DistanceY(g-4,g1) = 10
    c: DistanceY(g0,g-3) = 10
    c: Equal(g0,g2)
    c: DistanceX(g0,g0) = 10
FEATURE [PartDesign::Plane] DatumPlane005
  AttachmentOffset = pos=(0,0,-2.5) rot=(0,0,1;0rad)
  Length = 504.557
  MapMode = 5
  Placement = pos=(0,0,-8.9) rot=(0,0,1;0rad)
  ResizeMode = 0
  Support = -> [Pocket017]
  Width = 231.778
FEATURE [Sketcher::SketchObject] Sketch034
  ExternalGeometry = -> [Sketch033]
  FullyConstrained = true
  MapMode = 5
  Placement = pos=(0,0,-8.9) rot=(0,0,1;0rad)
  Support = -> [DatumPlane005]
  sketch-geometry (4):
    g0: LineSegment StartX=215.026 StartY=-24.5742 StartZ=0 EndX=240.575 EndY=-135.346 EndZ=0
    g1: LineSegment StartX=240.575 StartY=-135.346 StartZ=0 EndX=230.575 EndY=-135.346 EndZ=0
    g2: LineSegment StartX=230.575 StartY=-135.346 StartZ=0 EndX=205.026 EndY=-24.5742 EndZ=0
    g3: LineSegment StartX=205.026 StartY=-24.5742 StartZ=0 EndX=215.026 EndY=-24.5742 EndZ=0
  constraints (8):
    c: Coincident(g0,g-3)
    c: Coincident(g0,g-4)
    c: Coincident(g1,g0)
    c: Coincident(g1,g-4)
    c: Coincident(g2,g1)
    c: Coincident(g2,g-3)
    c: Coincident(g3,g2)
    c: Coincident(g3,g0)
FEATURE [PartDesign::AdditiveLoft] AdditiveLoft002
  BaseFeature = -> Pocket017
  Closed = false
  Profile = -> Sketch033
  Ruled = false
  Sections = -> [Sketch034]
FEATURE [PartDesign::Plane] DatumPlane006
  Length = 295.258
  MapMode = 13
  Placement = pos=(213.543,-61.4982,-11.8256) rot=(0.664312,-0.528531,-0.528531;1.96885rad)
  ResizeMode = 0
  Support = -> [AdditiveLoft002]
  Width = 73.3211
FEATURE [Sketcher::SketchObject] Sketch035
  ExternalGeometry = -> [AdditiveLoft002]
  FullyConstrained = true
  MapMode = 5
  Placement = pos=(213.543,-61.4982,-11.8256) rot=(0.664312,-0.528531,-0.528531;1.96885rad)
  Support = -> [DatumPlane006]
  sketch-geometry (2):
    g0: Circle CenterX=-31.8935 CenterY=-1.07443 CenterZ=0 NormalX=0 NormalY=0 NormalZ=1 AngleXU=0 Radius=1.55
    g1: Circle CenterX=14.1065 CenterY=0.925575 CenterZ=0 NormalX=0 NormalY=0 NormalZ=1 AngleXU=0 Radius=1.55
  constraints (6):
    c: Equal(g1,g0)
    c: Diameter(g0) = 3.1
    c: DistanceX(g-3,g0) = 6
    c: DistanceY(g0,g-3) = 4
    c: DistanceY(g1,g-3) = 2
    c: DistanceX(g-3,g1) = 52
FEATURE [PartDesign::Pocket] Pocket018
  BaseFeature = -> AdditiveLoft002
  Direction = (0.974417,0.224747,6.5e-15)
  Length = 5
  Length2 = 5
  Profile = -> Sketch035
  ReferenceAxis = -> Sketch035 [N_Axis]
  Type = 2
FEATURE [Sketcher::SketchObject] Sketch036
  ExternalGeometry = -> [Binder011]
  FullyConstrained = true
  MapMode = 5
  Placement = pos=(0,-4.2502,5.8) rot=(-1,0,0;1.5708rad)
  Support = -> [Pocket006]
  sketch-geometry (4):
    g0: ArcOfCircle CenterX=289.074 CenterY=13.8 CenterZ=0 NormalX=0 NormalY=0 NormalZ=1 AngleXU=0 Radius=4.5 StartAngle=1.5708 EndAngle=4.71239
    g1: ArcOfCircle CenterX=295.074 CenterY=13.8 CenterZ=0 NormalX=0 NormalY=0 NormalZ=1 AngleXU=0 Radius=4.5 StartAngle=4.71239 EndAngle=7.85398
    g2: LineSegment StartX=289.074 StartY=9.3 StartZ=0 EndX=295.074 EndY=9.3 EndZ=0
    g3: LineSegment StartX=295.074 StartY=18.3 StartZ=0 EndX=289.074 EndY=18.3 EndZ=0
  constraints (8):
    c: Tangent(g0,g2) = -1.5708
    c: Tangent(g2,g1) = -1.5708
    c: Tangent(g1,g3) = -1.5708
    c: Tangent(g3,g0) = -1.5708
    c: Equal(g0,g1)
    c: Coincident(g0,g-3)
    c: Coincident(g1,g-4)
    c: Diameter(g1) = 9
FEATURE [PartDesign::Pocket] Pocket019
  BaseFeature = -> Pocket006
  Direction = (0,-1,-4e-16)
  Length = 4
  Length2 = 5
  Placement = pos=(0,0,5.8) rot=(1,0,0;3.14159rad)
  Profile = -> Sketch036
  ReferenceAxis = -> Sketch036 [N_Axis]
  Type = 0
FEATURE [PartDesign::SubShapeBinder] Binder013  label="RearScrewHoleBinder"
  BindCopyOnChange = 0
  BindMode = 0
  ClaimChildren = false
  Context = -> Body005 [Binder013.]
  Fuse = false
  MakeFace = true
  OffsetFill = false
  OffsetIntersection = false
  OffsetJoinType = 0
  OffsetOpenResult = false
  PartialLoad = false
  Relative = true
  Support = -> [Body002[Sketch032.Edge1,Pocket018.Edge209,Sketch032.Edge4,Sketch032.Edge3]]
  _Version = 2
FEATURE [PartDesign::Plane] DatumPlane007
  AttachmentOffset = pos=(0,0,9) rot=(0,0,1;0rad)
  Length = 478.848
  MapMode = 5
  Placement = pos=(0,-7.24539,0.513296) rot=(0,0.731665,0.681664;3.14159rad)
  ResizeMode = 0
  Support = -> [Binder013]
  Width = 91.7746
FEATURE [Sketcher::SketchObject] Sketch037
  ExternalGeometry = -> [Binder013]
  FullyConstrained = true
  MapMode = 5
  Placement = pos=(0,-7.24539,0.513296) rot=(0,0.731665,0.681664;3.14159rad)
  Support = -> [DatumPlane007]
  sketch-geometry (4):
    g0: Circle CenterX=-335.426 CenterY=-11.3557 CenterZ=0 NormalX=0 NormalY=0 NormalZ=1 AngleXU=0 Radius=1.55
    g1: Circle CenterX=-270.426 CenterY=-11.3557 CenterZ=0 NormalX=0 NormalY=0 NormalZ=1 AngleXU=0 Radius=1.55
    g2: Circle CenterX=-172.756 CenterY=-11.3557 CenterZ=0 NormalX=0 NormalY=0 NormalZ=1 AngleXU=0 Radius=1.55
    g3: Circle CenterX=-97.7562 CenterY=-11.3557 CenterZ=0 NormalX=0 NormalY=0 NormalZ=1 AngleXU=0 Radius=1.55
  constraints (8):
    c: Coincident(g0,g-3)
    c: Coincident(g1,g-4)
    c: Coincident(g2,g-5)
    c: Coincident(g3,g-6)
    c: Equal(g2,g1)
    c: Equal(g1,g0)
    c: Equal(g0,g3)
    c: Diameter(g3) = 3.1
FEATURE [PartDesign::Pocket] Pocket020
  BaseFeature = -> Pocket019
  Direction = (0,-0.9975,0.0706674)
  Length = 5
  Length2 = 5
  Placement = pos=(0,0,5.8) rot=(1,0,0;3.14159rad)
  Profile = -> Sketch037
  ReferenceAxis = -> Sketch037 [N_Axis]
  Type = 4
FEATURE [Sketcher::SketchObject] Sketch038
  ExternalGeometry = -> [Sketch037]
  FullyConstrained = true
  MapMode = 5
  Placement = pos=(0,-7.24539,0.513296) rot=(0,0.731665,0.681664;3.14159rad)
  Support = -> [DatumPlane007]
  sketch-geometry (4):
    g0: Circle CenterX=-335.426 CenterY=-11.3557 CenterZ=0 NormalX=0 NormalY=0 NormalZ=1 AngleXU=0 Radius=2.95
    g1: Circle CenterX=-270.426 CenterY=-11.3557 CenterZ=0 NormalX=0 NormalY=0 NormalZ=1 AngleXU=0 Radius=2.95
    g2: Circle CenterX=-172.756 CenterY=-11.3557 CenterZ=0 NormalX=0 NormalY=0 NormalZ=1 AngleXU=0 Radius=2.95
    g3: Circle CenterX=-97.7562 CenterY=-11.3557 CenterZ=0 NormalX=0 NormalY=0 NormalZ=1 AngleXU=0 Radius=2.95
  constraints (8):
    c: Coincident(g0,g-3)
    c: Diameter(g0) = 5.9
    c: Coincident(g1,g-4)
    c: Coincident(g2,g-5)
    c: Coincident(g3,g-6)
    c: Equal(g3,g2)
    c: Equal(g2,g1)
    c: Diameter(g3) = 5.9
FEATURE [PartDesign::Pocket] Pocket021
  BaseFeature = -> Pocket020
  Direction = (0,-0.9975,0.0706674)
  Length = 5
  Length2 = 5
  Placement = pos=(0,0,5.8) rot=(1,0,0;3.14159rad)
  Profile = -> Sketch038
  ReferenceAxis = -> Sketch038 [N_Axis]
  Reversed = true
  Type = 1
FEATURE [PartDesign::Plane] DatumPlane008
  Length = 210.349
  MapMode = 13
  Placement = pos=(20.0895,-100.553,-11.3358) rot=(0.539504,0.545655,0.641245;2.01148rad)
  ResizeMode = 0
  Support = -> [Sketch006,Pocket018]
  Width = 151.062
FEATURE [Sketcher::SketchObject] Sketch039
  ExternalGeometry = -> [Pocket018]
  FullyConstrained = true
  MapMode = 5
  Placement = pos=(20.0895,-100.553,-11.3358) rot=(0.539504,0.545655,0.641245;2.01148rad)
  Support = -> [DatumPlane008]
  sketch-geometry (8):
    g0: LineSegment StartX=61.8018 StartY=3.79529 StartZ=0 EndX=56.8018 EndY=3.79529 EndZ=0
    g1: LineSegment StartX=56.8018 StartY=3.79529 StartZ=0 EndX=56.8018 EndY=-1.20471 EndZ=0
    g2: LineSegment StartX=56.8018 StartY=-1.20471 StartZ=0 EndX=61.8018 EndY=-1.20471 EndZ=0
    g3: LineSegment StartX=61.8018 StartY=-1.20471 StartZ=0 EndX=61.8018 EndY=3.79529 EndZ=0
    g4: LineSegment StartX=-8.19816 StartY=3.79529 StartZ=0 EndX=-3.19816 EndY=3.79529 EndZ=0
    g5: LineSegment StartX=-3.19816 StartY=3.79529 StartZ=0 EndX=-3.19816 EndY=-1.20471 EndZ=0
    g6: LineSegment StartX=-3.19816 StartY=-1.20471 StartZ=0 EndX=-8.19816 EndY=-1.20471 EndZ=0
    g7: LineSegment StartX=-8.19816 StartY=-1.20471 StartZ=0 EndX=-8.19816 EndY=3.79529 EndZ=0
  constraints (24):
    c: Coincident(g0,g1)
    c: Coincident(g1,g2)
    c: Coincident(g2,g3)
    c: Coincident(g3,g0)
    c: Horizontal(g0)
    c: Horizontal(g2)
    c: Vertical(g1)
    c: Vertical(g3)
    c: Coincident(g4,g5)
    c: Coincident(g5,g6)
    c: Coincident(g6,g7)
    c: Coincident(g7,g4)
    c: Horizontal(g4)
    c: Horizontal(g6)
    c: Vertical(g5)
    c: Vertical(g7)
    c: Horizontal(g0,g4)
    c: DistanceY(g0,g-3) = 1
    c: Equal(g3,g5)
    c: Equal(g4,g0)
    c: DistanceX(g0,g-3) = 10
    c: DistanceY(g3,g3) = 5
    c: Equal(g3,g0)
    c: DistanceX(g4,g0) = 60
FEATURE [PartDesign::Pad] Pad009  label="LeftSupportStuds"
  BaseFeature = -> Pocket018
  Direction = (0.987048,0.0111909,0.160037)
  Length = 3
  Length2 = 10
  Profile = -> Sketch039
  ReferenceAxis = -> Sketch039 [N_Axis]
  Type = 0
FEATURE [Sketcher::SketchObject] Sketch040
  ExternalGeometry = -> [Pad009]
  FullyConstrained = true
  MapMode = 5
  Placement = pos=(19.6323,0.222585,3.18311) rot=(0.539208,0.546346,0.640906;2.01032rad)
  Support = -> [Pad009]
  sketch-geometry (2):
    g0: Circle CenterX=-41.4533 CenterY=-12.6246 CenterZ=0 NormalX=0 NormalY=0 NormalZ=1 AngleXU=0 Radius=1.45
    g1: Circle CenterX=-106.453 CenterY=-12.6246 CenterZ=0 NormalX=0 NormalY=0 NormalZ=1 AngleXU=0 Radius=1.45
  constraints (6):
    c: Horizontal(g1,g0)
    c: Equal(g0,g1)
    c: DistanceY(g1,g-3) = 2
    c: DistanceX(g-3,g1) = 2.5
    c: DistanceX(g-4,g0) = 2.5
    c: Diameter(g1) = 2.9
FEATURE [PartDesign::Pocket] Pocket022
  BaseFeature = -> Pad009
  Direction = (-0.987048,-0.0111909,-0.160037)
  Length = 5
  Length2 = 5
  Profile = -> Sketch040
  ReferenceAxis = -> Sketch040 [N_Axis]
  Type = 1
FEATURE [PartDesign::Chamfer] Chamfer001
  Angle = 45
  Base = -> Pocket022 [Edge255]
  BaseFeature = -> Pocket022
  ChamferType = 0
  FlipDirection = false
  Size = 1
  Size2 = 1
  SupportTransform = false
  UseAllEdges = false
FEATURE [PartDesign::Plane] DatumPlane009
  Length = 210.349
  MapMode = 13
  Placement = pos=(423.093,-102.5,-11.1997) rot=(0.539504,-0.545655,-0.641245;2.01148rad)
  ResizeMode = 0
  Support = -> [Chamfer001]
  Width = 151.062
FEATURE [Sketcher::SketchObject] Sketch041
  ExternalGeometry = -> [Chamfer001]
  FullyConstrained = true
  MapMode = 5
  Placement = pos=(423.093,-102.5,-11.1997) rot=(0.539504,-0.545655,-0.641245;2.01148rad)
  Support = -> [DatumPlane009]
  sketch-geometry (8):
    g0: LineSegment StartX=-63.7485 StartY=3.65737 StartZ=0 EndX=-58.7485 EndY=3.65737 EndZ=0
    g1: LineSegment StartX=-58.7485 StartY=3.65737 StartZ=0 EndX=-58.7485 EndY=-1.34263 EndZ=0
    g2: LineSegment StartX=-58.7485 StartY=-1.34263 StartZ=0 EndX=-63.7485 EndY=-1.34263 EndZ=0
    g3: LineSegment StartX=-63.7485 StartY=-1.34263 StartZ=0 EndX=-63.7485 EndY=3.65737 EndZ=0
    g4: LineSegment StartX=1.25148 StartY=3.65737 StartZ=0 EndX=6.25148 EndY=3.65737 EndZ=0
    g5: LineSegment StartX=6.25148 StartY=3.65737 StartZ=0 EndX=6.25148 EndY=-1.34263 EndZ=0
    g6: LineSegment StartX=6.25148 StartY=-1.34263 StartZ=0 EndX=1.25148 EndY=-1.34263 EndZ=0
    g7: LineSegment StartX=1.25148 StartY=-1.34263 StartZ=0 EndX=1.25148 EndY=3.65737 EndZ=0
  constraints (24):
    c: Coincident(g0,g1)
    c: Coincident(g1,g2)
    c: Coincident(g2,g3)
    c: Coincident(g3,g0)
    c: Horizontal(g0)
    c: Horizontal(g2)
    c: Vertical(g1)
    c: Vertical(g3)
    c: Coincident(g4,g5)
    c: Coincident(g5,g6)
    c: Coincident(g6,g7)
    c: Coincident(g7,g4)
    c: Horizontal(g4)
    c: Horizontal(g6)
    c: Vertical(g5)
    c: Vertical(g7)
    c: Equal(g0,g3)
    c: Equal(g0,g4)
    c: Equal(g7,g3)
    c: Horizontal(g0,g4)
    c: DistanceY(g0,g-3) = 1
    c: DistanceX(g-3,g0) = 10
    c: DistanceY(g3,g3) = 5
    c: DistanceX(g0,g4) = 60
FEATURE [PartDesign::Pad] Pad010  label="RightSupportStuds"
  BaseFeature = -> Chamfer001
  Direction = (-0.987048,0.0111909,0.160037)
  Length = 3
  Length2 = 10
  Profile = -> Sketch041
  ReferenceAxis = -> Sketch041 [N_Axis]
  Type = 0
FEATURE [Sketcher::SketchObject] Sketch042
  ExternalGeometry = -> [Pad010]
  FullyConstrained = true
  MapMode = 5
  Placement = pos=(412.144,-4.67277,-66.8237) rot=(0.539208,-0.546346,-0.640906;2.01032rad)
  Support = -> [Pad010]
  sketch-geometry (2):
    g0: Circle CenterX=36.5577 CenterY=58.4323 CenterZ=0 NormalX=0 NormalY=0 NormalZ=1 AngleXU=0 Radius=1.45
    g1: Circle CenterX=101.558 CenterY=58.4323 CenterZ=0 NormalX=0 NormalY=0 NormalZ=1 AngleXU=0 Radius=1.45
  constraints (6):
    c: Equal(g1,g0)
    c: Diameter(g0) = 2.9
    c: DistanceY(g0,g-3) = 2
    c: DistanceX(g-3,g0) = 2.5
    c: Horizontal(g0,g1)
    c: DistanceX(g-4,g1) = 2.5
FEATURE [PartDesign::Pocket] Pocket023
  BaseFeature = -> Pad010
  Direction = (0.987048,-0.0111909,-0.160037)
  Length = 5
  Length2 = 5
  Profile = -> Sketch042
  ReferenceAxis = -> Sketch042 [N_Axis]
  Type = 1
FEATURE [PartDesign::Chamfer] Chamfer002
  Angle = 45
  Base = -> Pocket023 [Edge290]
  BaseFeature = -> Pocket023
  ChamferType = 0
  FlipDirection = false
  Size = 1
  Size2 = 1
  SupportTransform = false
  UseAllEdges = false
FEATURE [PartDesign::Body] Body002  label="Case"
  Group = -> [Binder,Sketch004,DatumPlane,Sketch005,DatumPlane001,Sketch006,AdditiveLoft,Sketch007,SubtractiveLoft,Sketch008,Fillet,Sketch011,Pocket002,Binder003,Sketch012,Pad004,Pocket003,Sketch029,Pocket014,Sketch030,Pocket015,Pocket016,Sketch031,Pad008,Chamfer,Sketch032,Pocket017,Sketch033,DatumPlane005,Sketch034,AdditiveLoft002,DatumPlane006,Sketch035,Pocket018,DatumPlane008,Sketch039,Pad009,Sketch040,+8 more]
  Origin = -> Origin002
  Tip = -> Chamfer002
FEATURE [PartDesign::SubShapeBinder] Binder014  label="Side screw holes binder"
  BindCopyOnChange = 0
  BindMode = 0
  ClaimChildren = false
  Context = -> Body005 [Binder014.]
  Fuse = false
  MakeFace = true
  OffsetFill = false
  OffsetIntersection = false
  OffsetJoinType = 0
  OffsetOpenResult = false
  PartialLoad = false
  Relative = true
  Support = -> [Body002[Chamfer002.Edge167,Chamfer002.Edge339,Chamfer002.Edge23,Chamfer002.Edge145]]
  _Version = 2
FEATURE [PartDesign::Plane] DatumPlane010
  AttachmentOffset = pos=(0,0,-8) rot=(0,0,1;0rad)
  Length = 146.58
  MapMode = 45
  Placement = pos=(14.5734,-73.8156,-10.4266) rot=(0.64805,0.004262,0.761586;3.14885rad)
  ResizeMode = 0
  Support = -> [Binder014]
  Width = 163.478
FEATURE [Sketcher::SketchObject] Sketch043
  ExternalGeometry = -> [Binder014]
  FullyConstrained = true
  MapMode = 5
  Placement = pos=(14.5734,-73.8156,-10.4266) rot=(0.64805,0.004262,0.761586;3.14885rad)
  Support = -> [DatumPlane010]
  sketch-geometry (2):
    g0: Circle CenterX=-7.1e-15 CenterY=32.4999 CenterZ=0 NormalX=0 NormalY=0 NormalZ=1 AngleXU=0 Radius=1.55
    g1: Circle CenterX=0 CenterY=-32.4999 CenterZ=0 NormalX=0 NormalY=0 NormalZ=1 AngleXU=0 Radius=1.55
  constraints (4):
    c: Coincident(g0,g-3)
    c: Coincident(g1,g-4)
    c: Equal(g0,g1)
    c: Diameter(g0) = 3.1
FEATURE [PartDesign::Pocket] Pocket024
  BaseFeature = -> Pocket021
  Direction = (-0.987048,-0.0111909,-0.160037)
  Length = 5
  Length2 = 5
  Placement = pos=(0,0,5.8) rot=(1,0,0;3.14159rad)
  Profile = -> Sketch043
  ReferenceAxis = -> Sketch043 [N_Axis]
  Reversed = true
  Type = 1
FEATURE [Sketcher::SketchObject] Sketch044
  ExternalGeometry = -> [Pocket024]
  FullyConstrained = true
  MapMode = 5
  Placement = pos=(10.8197,0.122671,7.55427) rot=(-0.548475,0.541309,-0.637306;1.99814rad)
  Support = -> [Pocket024]
  sketch-geometry (2):
    g0: Circle CenterX=41.4429 CenterY=18.3498 CenterZ=0 NormalX=0 NormalY=0 NormalZ=1 AngleXU=0 Radius=2.95
    g1: Circle CenterX=106.443 CenterY=18.3498 CenterZ=0 NormalX=0 NormalY=0 NormalZ=1 AngleXU=0 Radius=2.95
  constraints (4):
    c: Coincident(g0,g-4)
    c: Coincident(g1,g-3)
    c: Equal(g1,g0)
    c: Diameter(g0) = 5.9
FEATURE [PartDesign::Pocket] Pocket025
  BaseFeature = -> Pocket024
  Direction = (-0.987048,-0.0111909,-0.160037)
  Length = 5
  Length2 = 5
  Placement = pos=(0,0,5.8) rot=(1,0,0;3.14159rad)
  Profile = -> Sketch044
  ReferenceAxis = -> Sketch044 [N_Axis]
  Type = 1
FEATURE [PartDesign::Plane] DatumPlane011
  AttachmentOffset = pos=(0,0,8) rot=(0,0,1;0rad)
  Length = 146.58
  MapMode = 45
  Placement = pos=(428.629,-73.8156,-10.3012) rot=(0.761588,-0.003626,0.648052;3.13307rad)
  ResizeMode = 0
  Support = -> [Binder014]
  Width = 163.478
FEATURE [Sketcher::SketchObject] Sketch045
  ExternalGeometry = -> [Binder014]
  FullyConstrained = true
  MapMode = 5
  Placement = pos=(428.629,-73.8156,-10.3012) rot=(0.761588,-0.003626,0.648052;3.13307rad)
  Support = -> [DatumPlane011]
  sketch-geometry (2):
    g0: Circle CenterX=4.97e-14 CenterY=32.4999 CenterZ=0 NormalX=0 NormalY=0 NormalZ=1 AngleXU=0 Radius=1.55
    g1: Circle CenterX=4.97e-14 CenterY=-32.4999 CenterZ=0 NormalX=0 NormalY=0 NormalZ=1 AngleXU=0 Radius=1.55
  constraints (4):
    c: Coincident(g0,g-3)
    c: Coincident(g1,g-4)
    c: Equal(g1,g0)
    c: Diameter(g1) = 3.1
FEATURE [PartDesign::Pocket] Pocket026
  BaseFeature = -> Pocket025
  Direction = (-0.987048,0.0111909,0.160037)
  Length = 5
  Length2 = 5
  Placement = pos=(0,0,5.8) rot=(1,0,0;3.14159rad)
  Profile = -> Sketch045
  ReferenceAxis = -> Sketch045 [N_Axis]
  Type = 1
FEATURE [Sketcher::SketchObject] Sketch046
  ExternalGeometry = -> [Pocket026]
  FullyConstrained = true
  MapMode = 5
  Placement = pos=(420.957,-4.77268,-62.4525) rot=(-0.548475,-0.541309,0.637306;1.99814rad)
  Support = -> [Pocket026]
  sketch-geometry (2):
    g0: Circle CenterX=-101.547 CenterY=-52.7071 CenterZ=0 NormalX=0 NormalY=0 NormalZ=1 AngleXU=0 Radius=2.95
    g1: Circle CenterX=-36.5473 CenterY=-52.7071 CenterZ=0 NormalX=0 NormalY=0 NormalZ=1 AngleXU=0 Radius=2.95
  constraints (4):
    c: Coincident(g0,g-3)
    c: Coincident(g1,g-4)
    c: Equal(g1,g0)
    c: Diameter(g0) = 5.9
FEATURE [PartDesign::Pocket] Pocket027
  BaseFeature = -> Pocket026
  Direction = (0.987048,-0.0111909,-0.160037)
  Length = 5
  Length2 = 5
  Placement = pos=(0,0,5.8) rot=(1,0,0;3.14159rad)
  Profile = -> Sketch046
  ReferenceAxis = -> Sketch046 [N_Axis]
  Type = 1
FEATURE [PartDesign::Body] Body005  label="Top Plate support"
  Group = -> [Binder010,Binder006,Sketch015,Pad006,DatumPlane002,Sketch016,Sketch017,Binder008,Binder009,Binder011,AdditiveLoft001,Sketch019,Pocket006,Binder012,Sketch036,Pocket019,Binder013,DatumPlane007,Sketch037,Pocket020,Sketch038,Pocket021,Binder014,DatumPlane010,Sketch043,Pocket024,Sketch044,Pocket025,DatumPlane011,Sketch045,Pocket026,Sketch046,Pocket027]
  Origin = -> Origin005
  Tip = -> Pocket027
FEATURE [Part::FeaturePython] Slice002  # WARN: FeaturePython — macro-defined, semantics opaque (R4)
  Base = -> Pocket027
  Mode = 1
  Tolerance = 0
  Tools = -> [Rectangle005]
FEATURE [Part::FeaturePython] Slice002_child0  label="Slice002.0"  # WARN: FeaturePython — macro-defined, semantics opaque (R4)
  Base = -> Slice002
  FilterType = 1
  Invert = false
  OverrideMaxVal = 0
  WindowFrom = 80
  WindowTo = 100
  items = 0
FEATURE [Part::FeaturePython] Slice002_child1  label="Slice002.1"  # WARN: FeaturePython — macro-defined, semantics opaque (R4)
  Base = -> Slice002
  FilterType = 1
  Invert = false
  OverrideMaxVal = 0
  WindowFrom = 80
  WindowTo = 100
  items = 1
FEATURE [App::DocumentObjectGroup] GrExplode_Slice002  label="Top plate support slices"
  Group = -> [Slice002_child0,Slice002_child1]
FEATURE [Part::FeaturePython] Slice003  # WARN: FeaturePython — macro-defined, semantics opaque (R4)
  Base = -> Chamfer002
  Mode = 1
  Tolerance = 0
  Tools = -> [Rectangle006]
FEATURE [Part::FeaturePython] Slice003_child0  label="Slice003.0"  # WARN: FeaturePython — macro-defined, semantics opaque (R4)
  Base = -> Slice003
  FilterType = 1
  Invert = false
  OverrideMaxVal = 0
  WindowFrom = 80
  WindowTo = 100
  items = 0
FEATURE [Part::FeaturePython] Slice003_child1  label="Slice003.1"  # WARN: FeaturePython — macro-defined, semantics opaque (R4)
  Base = -> Slice003
  FilterType = 1
  Invert = false
  OverrideMaxVal = 0
  WindowFrom = 80
  WindowTo = 100
  items = 1
FEATURE [App::DocumentObjectGroup] GrExplode_Slice003  label="Case slices"
  Group = -> [Slice003_child0,Slice003_child1]
